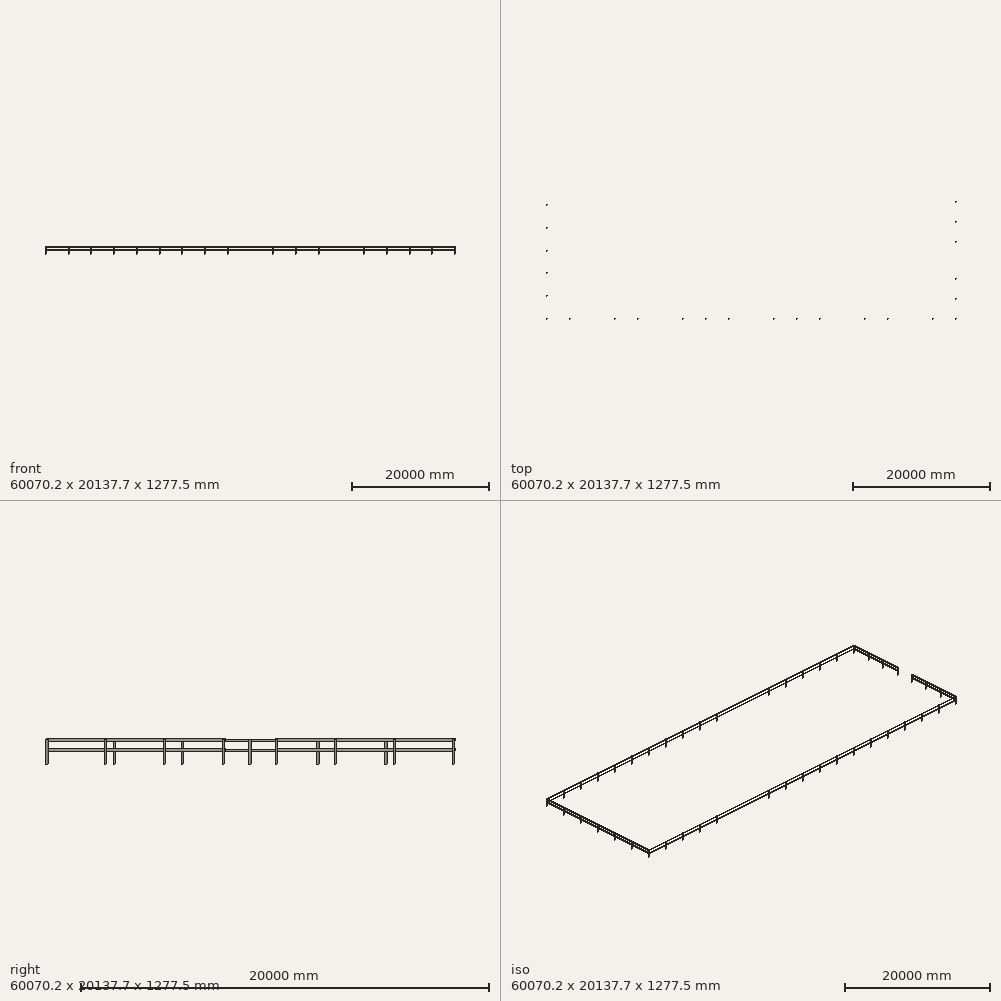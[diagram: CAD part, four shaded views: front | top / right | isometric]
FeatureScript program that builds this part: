
annotation { "Feature Type Name" : "Feature", "Feature Type Description" : "" }
export const myFeature = defineFeature(function(context is Context, id is Id, definition is map)
    precondition{}
    {
        {
            var Q0;
            Q0=qCreatedBy(makeId("Top.planeOp"),FACE);
            var sketch = newSketch(context, id + "F0", { "sketchPlane" : qUnion([Q0])});
            skCircle(sketch, "E0", {"center": v(5.25, 29.78) * mm, "radius": 62.5 * mm});
            skPoint(sketch, "E0.first.point", {"position": v(-49.7, 0) * mm});
            skPoint(sketch, "E0.second.point", {"position": v(41.75, 80.52) * mm});
            skPoint(sketch, "E0.third.point", {"position": v(-50.7, 57.65) * mm});
            skSolve(sketch);
        }
        {
            var Q0;
            Q0=makeQuery(id+"F0.imprint","IMPRINT",FACE,{"disambiguationData":[TD([[makeQuery(id+"F0.imprint","IMPRINT",EDGE,{"derivedFrom":sQuery(id+"F0.wireOp",EDGE,"E0")}),1.0]])]});
            extrude(context, id + "F1", {"entities" : qUnion([Q0]), "depth" : 1250 * mm});
        }
        {
            var Q0;
            Q0=makeQuery(id+"F1.opExtrude","SWEPT_BODY",BODY,{"disambiguationData":[OSD([sQuery(id+"F0.wireOp",EDGE,"E0")])]});
            transform(context, id + "F2", {"entities" : qUnion([Q0]), "transformType" : TransformType.TRANSLATION_3D, "dx" : 3330 * mm, "dy" : 0 * mm, "dz" : 0 * mm, "makeCopy" : true});
        }
        {
            var Q0;
            Q0=makeQuery(id+"F2.opPattern","COPY",BODY,{"derivedFrom":makeQuery(id+"F1.opExtrude","SWEPT_BODY",BODY,{"disambiguationData":[OSD([sQuery(id+"F0.wireOp",EDGE,"E0")])]}),"instanceName":"1"});
            transform(context, id + "F3", {"entities" : qUnion([Q0]), "transformType" : TransformType.TRANSLATION_3D, "dx" : 3330 * mm, "dy" : 0 * mm, "dz" : 0 * mm, "makeCopy" : true});
        }
        {
            var Q0;
            Q0=makeQuery(id+"F3.opPattern","COPY",BODY,{"derivedFrom":makeQuery(id+"F2.opPattern","COPY",BODY,{"derivedFrom":makeQuery(id+"F1.opExtrude","SWEPT_BODY",BODY,{"disambiguationData":[OSD([sQuery(id+"F0.wireOp",EDGE,"E0")])]}),"instanceName":"1"}),"instanceName":"1"});
            transform(context, id + "F4", {"entities" : qUnion([Q0]), "transformType" : TransformType.TRANSLATION_3D, "dx" : 3330 * mm, "dy" : 0 * mm, "dz" : 0 * mm, "makeCopy" : true});
        }
        {
            var Q0;
            Q0=makeQuery(id+"F4.opPattern","COPY",BODY,{"derivedFrom":makeQuery(id+"F3.opPattern","COPY",BODY,{"derivedFrom":makeQuery(id+"F2.opPattern","COPY",BODY,{"derivedFrom":makeQuery(id+"F1.opExtrude","SWEPT_BODY",BODY,{"disambiguationData":[OSD([sQuery(id+"F0.wireOp",EDGE,"E0")])]}),"instanceName":"1"}),"instanceName":"1"}),"instanceName":"1"});
            transform(context, id + "F5", {"entities" : qUnion([Q0]), "transformType" : TransformType.TRANSLATION_3D, "dx" : 3330 * mm, "dy" : 0 * mm, "dz" : 0 * mm, "makeCopy" : true});
        }
        {
            var Q0;
            Q0=makeQuery(id+"F5.opPattern","COPY",BODY,{"derivedFrom":makeQuery(id+"F4.opPattern","COPY",BODY,{"derivedFrom":makeQuery(id+"F3.opPattern","COPY",BODY,{"derivedFrom":makeQuery(id+"F2.opPattern","COPY",BODY,{"derivedFrom":makeQuery(id+"F1.opExtrude","SWEPT_BODY",BODY,{"disambiguationData":[OSD([sQuery(id+"F0.wireOp",EDGE,"E0")])]}),"instanceName":"1"}),"instanceName":"1"}),"instanceName":"1"}),"instanceName":"1"});
            transform(context, id + "F6", {"entities" : qUnion([Q0]), "transformType" : TransformType.TRANSLATION_3D, "dx" : 3330 * mm, "dy" : 0 * mm, "dz" : 0 * mm, "makeCopy" : true});
        }
        {
            var Q0;
            Q0=makeQuery(id+"F6.opPattern","COPY",BODY,{"derivedFrom":makeQuery(id+"F5.opPattern","COPY",BODY,{"derivedFrom":makeQuery(id+"F4.opPattern","COPY",BODY,{"derivedFrom":makeQuery(id+"F3.opPattern","COPY",BODY,{"derivedFrom":makeQuery(id+"F2.opPattern","COPY",BODY,{"derivedFrom":makeQuery(id+"F1.opExtrude","SWEPT_BODY",BODY,{"disambiguationData":[OSD([sQuery(id+"F0.wireOp",EDGE,"E0")])]}),"instanceName":"1"}),"instanceName":"1"}),"instanceName":"1"}),"instanceName":"1"}),"instanceName":"1"});
            transform(context, id + "F7", {"entities" : qUnion([Q0]), "transformType" : TransformType.TRANSLATION_3D, "dx" : 3330 * mm, "dy" : 0 * mm, "dz" : 0 * mm, "makeCopy" : true});
        }
        {
            var Q0;
            Q0=makeQuery(id+"F7.opPattern","COPY",BODY,{"derivedFrom":makeQuery(id+"F6.opPattern","COPY",BODY,{"derivedFrom":makeQuery(id+"F5.opPattern","COPY",BODY,{"derivedFrom":makeQuery(id+"F4.opPattern","COPY",BODY,{"derivedFrom":makeQuery(id+"F3.opPattern","COPY",BODY,{"derivedFrom":makeQuery(id+"F2.opPattern","COPY",BODY,{"derivedFrom":makeQuery(id+"F1.opExtrude","SWEPT_BODY",BODY,{"disambiguationData":[OSD([sQuery(id+"F0.wireOp",EDGE,"E0")])]}),"instanceName":"1"}),"instanceName":"1"}),"instanceName":"1"}),"instanceName":"1"}),"instanceName":"1"}),"instanceName":"1"});
            transform(context, id + "F8", {"entities" : qUnion([Q0]), "transformType" : TransformType.TRANSLATION_3D, "dx" : 3330 * mm, "dy" : 0 * mm, "dz" : 0 * mm, "makeCopy" : true});
        }
        {
            var Q0;
            Q0=makeQuery(id+"F8.opPattern","COPY",BODY,{"derivedFrom":makeQuery(id+"F7.opPattern","COPY",BODY,{"derivedFrom":makeQuery(id+"F6.opPattern","COPY",BODY,{"derivedFrom":makeQuery(id+"F5.opPattern","COPY",BODY,{"derivedFrom":makeQuery(id+"F4.opPattern","COPY",BODY,{"derivedFrom":makeQuery(id+"F3.opPattern","COPY",BODY,{"derivedFrom":makeQuery(id+"F2.opPattern","COPY",BODY,{"derivedFrom":makeQuery(id+"F1.opExtrude","SWEPT_BODY",BODY,{"disambiguationData":[OSD([sQuery(id+"F0.wireOp",EDGE,"E0")])]}),"instanceName":"1"}),"instanceName":"1"}),"instanceName":"1"}),"instanceName":"1"}),"instanceName":"1"}),"instanceName":"1"}),"instanceName":"1"});
            transform(context, id + "F9", {"entities" : qUnion([Q0]), "transformType" : TransformType.TRANSLATION_3D, "dx" : 3330 * mm, "dy" : 0 * mm, "dz" : 0 * mm, "makeCopy" : true});
        }
        {
            var Q0;
            Q0=makeQuery(id+"F9.opPattern","COPY",BODY,{"derivedFrom":makeQuery(id+"F8.opPattern","COPY",BODY,{"derivedFrom":makeQuery(id+"F7.opPattern","COPY",BODY,{"derivedFrom":makeQuery(id+"F6.opPattern","COPY",BODY,{"derivedFrom":makeQuery(id+"F5.opPattern","COPY",BODY,{"derivedFrom":makeQuery(id+"F4.opPattern","COPY",BODY,{"derivedFrom":makeQuery(id+"F3.opPattern","COPY",BODY,{"derivedFrom":makeQuery(id+"F2.opPattern","COPY",BODY,{"derivedFrom":makeQuery(id+"F1.opExtrude","SWEPT_BODY",BODY,{"disambiguationData":[OSD([sQuery(id+"F0.wireOp",EDGE,"E0")])]}),"instanceName":"1"}),"instanceName":"1"}),"instanceName":"1"}),"instanceName":"1"}),"instanceName":"1"}),"instanceName":"1"}),"instanceName":"1"}),"instanceName":"1"});
            transform(context, id + "F10", {"entities" : qUnion([Q0]), "transformType" : TransformType.TRANSLATION_3D, "dx" : 3330 * mm, "dy" : 0 * mm, "dz" : 0 * mm, "makeCopy" : true});
        }
        {
            var Q0;
            Q0=makeQuery(id+"F10.opPattern","COPY",BODY,{"derivedFrom":makeQuery(id+"F9.opPattern","COPY",BODY,{"derivedFrom":makeQuery(id+"F8.opPattern","COPY",BODY,{"derivedFrom":makeQuery(id+"F7.opPattern","COPY",BODY,{"derivedFrom":makeQuery(id+"F6.opPattern","COPY",BODY,{"derivedFrom":makeQuery(id+"F5.opPattern","COPY",BODY,{"derivedFrom":makeQuery(id+"F4.opPattern","COPY",BODY,{"derivedFrom":makeQuery(id+"F3.opPattern","COPY",BODY,{"derivedFrom":makeQuery(id+"F2.opPattern","COPY",BODY,{"derivedFrom":makeQuery(id+"F1.opExtrude","SWEPT_BODY",BODY,{"disambiguationData":[OSD([sQuery(id+"F0.wireOp",EDGE,"E0")])]}),"instanceName":"1"}),"instanceName":"1"}),"instanceName":"1"}),"instanceName":"1"}),"instanceName":"1"}),"instanceName":"1"}),"instanceName":"1"}),"instanceName":"1"}),"instanceName":"1"});
            transform(context, id + "F11", {"entities" : qUnion([Q0]), "transformType" : TransformType.TRANSLATION_3D, "dx" : 3330 * mm, "dy" : 0 * mm, "dz" : 0 * mm, "makeCopy" : true});
        }
        {
            var Q0;
            Q0=makeQuery(id+"F11.opPattern","COPY",BODY,{"derivedFrom":makeQuery(id+"F10.opPattern","COPY",BODY,{"derivedFrom":makeQuery(id+"F9.opPattern","COPY",BODY,{"derivedFrom":makeQuery(id+"F8.opPattern","COPY",BODY,{"derivedFrom":makeQuery(id+"F7.opPattern","COPY",BODY,{"derivedFrom":makeQuery(id+"F6.opPattern","COPY",BODY,{"derivedFrom":makeQuery(id+"F5.opPattern","COPY",BODY,{"derivedFrom":makeQuery(id+"F4.opPattern","COPY",BODY,{"derivedFrom":makeQuery(id+"F3.opPattern","COPY",BODY,{"derivedFrom":makeQuery(id+"F2.opPattern","COPY",BODY,{"derivedFrom":makeQuery(id+"F1.opExtrude","SWEPT_BODY",BODY,{"disambiguationData":[OSD([sQuery(id+"F0.wireOp",EDGE,"E0")])]}),"instanceName":"1"}),"instanceName":"1"}),"instanceName":"1"}),"instanceName":"1"}),"instanceName":"1"}),"instanceName":"1"}),"instanceName":"1"}),"instanceName":"1"}),"instanceName":"1"}),"instanceName":"1"});
            transform(context, id + "F12", {"entities" : qUnion([Q0]), "transformType" : TransformType.TRANSLATION_3D, "dx" : 3330 * mm, "dy" : 0 * mm, "dz" : 0 * mm, "makeCopy" : true});
        }
        {
            var Q0;
            Q0=makeQuery(id+"F12.opPattern","COPY",BODY,{"derivedFrom":makeQuery(id+"F11.opPattern","COPY",BODY,{"derivedFrom":makeQuery(id+"F10.opPattern","COPY",BODY,{"derivedFrom":makeQuery(id+"F9.opPattern","COPY",BODY,{"derivedFrom":makeQuery(id+"F8.opPattern","COPY",BODY,{"derivedFrom":makeQuery(id+"F7.opPattern","COPY",BODY,{"derivedFrom":makeQuery(id+"F6.opPattern","COPY",BODY,{"derivedFrom":makeQuery(id+"F5.opPattern","COPY",BODY,{"derivedFrom":makeQuery(id+"F4.opPattern","COPY",BODY,{"derivedFrom":makeQuery(id+"F3.opPattern","COPY",BODY,{"derivedFrom":makeQuery(id+"F2.opPattern","COPY",BODY,{"derivedFrom":makeQuery(id+"F1.opExtrude","SWEPT_BODY",BODY,{"disambiguationData":[OSD([sQuery(id+"F0.wireOp",EDGE,"E0")])]}),"instanceName":"1"}),"instanceName":"1"}),"instanceName":"1"}),"instanceName":"1"}),"instanceName":"1"}),"instanceName":"1"}),"instanceName":"1"}),"instanceName":"1"}),"instanceName":"1"}),"instanceName":"1"}),"instanceName":"1"});
            transform(context, id + "F13", {"entities" : qUnion([Q0]), "transformType" : TransformType.TRANSLATION_3D, "dx" : 3330 * mm, "dy" : 0 * mm, "dz" : 0 * mm, "makeCopy" : true});
        }
        {
            var Q0;
            Q0=makeQuery(id+"F13.opPattern","COPY",BODY,{"derivedFrom":makeQuery(id+"F12.opPattern","COPY",BODY,{"derivedFrom":makeQuery(id+"F11.opPattern","COPY",BODY,{"derivedFrom":makeQuery(id+"F10.opPattern","COPY",BODY,{"derivedFrom":makeQuery(id+"F9.opPattern","COPY",BODY,{"derivedFrom":makeQuery(id+"F8.opPattern","COPY",BODY,{"derivedFrom":makeQuery(id+"F7.opPattern","COPY",BODY,{"derivedFrom":makeQuery(id+"F6.opPattern","COPY",BODY,{"derivedFrom":makeQuery(id+"F5.opPattern","COPY",BODY,{"derivedFrom":makeQuery(id+"F4.opPattern","COPY",BODY,{"derivedFrom":makeQuery(id+"F3.opPattern","COPY",BODY,{"derivedFrom":makeQuery(id+"F2.opPattern","COPY",BODY,{"derivedFrom":makeQuery(id+"F1.opExtrude","SWEPT_BODY",BODY,{"disambiguationData":[OSD([sQuery(id+"F0.wireOp",EDGE,"E0")])]}),"instanceName":"1"}),"instanceName":"1"}),"instanceName":"1"}),"instanceName":"1"}),"instanceName":"1"}),"instanceName":"1"}),"instanceName":"1"}),"instanceName":"1"}),"instanceName":"1"}),"instanceName":"1"}),"instanceName":"1"}),"instanceName":"1"});
            transform(context, id + "F14", {"entities" : qUnion([Q0]), "transformType" : TransformType.TRANSLATION_3D, "dx" : 3330 * mm, "dy" : 0 * mm, "dz" : 0 * mm, "makeCopy" : true});
        }
        {
            var Q0;
            Q0=makeQuery(id+"F14.opPattern","COPY",BODY,{"derivedFrom":makeQuery(id+"F13.opPattern","COPY",BODY,{"derivedFrom":makeQuery(id+"F12.opPattern","COPY",BODY,{"derivedFrom":makeQuery(id+"F11.opPattern","COPY",BODY,{"derivedFrom":makeQuery(id+"F10.opPattern","COPY",BODY,{"derivedFrom":makeQuery(id+"F9.opPattern","COPY",BODY,{"derivedFrom":makeQuery(id+"F8.opPattern","COPY",BODY,{"derivedFrom":makeQuery(id+"F7.opPattern","COPY",BODY,{"derivedFrom":makeQuery(id+"F6.opPattern","COPY",BODY,{"derivedFrom":makeQuery(id+"F5.opPattern","COPY",BODY,{"derivedFrom":makeQuery(id+"F4.opPattern","COPY",BODY,{"derivedFrom":makeQuery(id+"F3.opPattern","COPY",BODY,{"derivedFrom":makeQuery(id+"F2.opPattern","COPY",BODY,{"derivedFrom":makeQuery(id+"F1.opExtrude","SWEPT_BODY",BODY,{"disambiguationData":[OSD([sQuery(id+"F0.wireOp",EDGE,"E0")])]}),"instanceName":"1"}),"instanceName":"1"}),"instanceName":"1"}),"instanceName":"1"}),"instanceName":"1"}),"instanceName":"1"}),"instanceName":"1"}),"instanceName":"1"}),"instanceName":"1"}),"instanceName":"1"}),"instanceName":"1"}),"instanceName":"1"}),"instanceName":"1"});
            transform(context, id + "F15", {"entities" : qUnion([Q0]), "transformType" : TransformType.TRANSLATION_3D, "dx" : 3330 * mm, "dy" : 0 * mm, "dz" : 0 * mm, "makeCopy" : true});
        }
        {
            var Q0;
            Q0=makeQuery(id+"F15.opPattern","COPY",BODY,{"derivedFrom":makeQuery(id+"F14.opPattern","COPY",BODY,{"derivedFrom":makeQuery(id+"F13.opPattern","COPY",BODY,{"derivedFrom":makeQuery(id+"F12.opPattern","COPY",BODY,{"derivedFrom":makeQuery(id+"F11.opPattern","COPY",BODY,{"derivedFrom":makeQuery(id+"F10.opPattern","COPY",BODY,{"derivedFrom":makeQuery(id+"F9.opPattern","COPY",BODY,{"derivedFrom":makeQuery(id+"F8.opPattern","COPY",BODY,{"derivedFrom":makeQuery(id+"F7.opPattern","COPY",BODY,{"derivedFrom":makeQuery(id+"F6.opPattern","COPY",BODY,{"derivedFrom":makeQuery(id+"F5.opPattern","COPY",BODY,{"derivedFrom":makeQuery(id+"F4.opPattern","COPY",BODY,{"derivedFrom":makeQuery(id+"F3.opPattern","COPY",BODY,{"derivedFrom":makeQuery(id+"F2.opPattern","COPY",BODY,{"derivedFrom":makeQuery(id+"F1.opExtrude","SWEPT_BODY",BODY,{"disambiguationData":[OSD([sQuery(id+"F0.wireOp",EDGE,"E0")])]}),"instanceName":"1"}),"instanceName":"1"}),"instanceName":"1"}),"instanceName":"1"}),"instanceName":"1"}),"instanceName":"1"}),"instanceName":"1"}),"instanceName":"1"}),"instanceName":"1"}),"instanceName":"1"}),"instanceName":"1"}),"instanceName":"1"}),"instanceName":"1"}),"instanceName":"1"});
            transform(context, id + "F16", {"entities" : qUnion([Q0]), "transformType" : TransformType.TRANSLATION_3D, "dx" : 3330 * mm, "dy" : 0 * mm, "dz" : 0 * mm, "makeCopy" : true});
        }
        {
            var Q0;
            Q0=makeQuery(id+"F16.opPattern","COPY",BODY,{"derivedFrom":makeQuery(id+"F15.opPattern","COPY",BODY,{"derivedFrom":makeQuery(id+"F14.opPattern","COPY",BODY,{"derivedFrom":makeQuery(id+"F13.opPattern","COPY",BODY,{"derivedFrom":makeQuery(id+"F12.opPattern","COPY",BODY,{"derivedFrom":makeQuery(id+"F11.opPattern","COPY",BODY,{"derivedFrom":makeQuery(id+"F10.opPattern","COPY",BODY,{"derivedFrom":makeQuery(id+"F9.opPattern","COPY",BODY,{"derivedFrom":makeQuery(id+"F8.opPattern","COPY",BODY,{"derivedFrom":makeQuery(id+"F7.opPattern","COPY",BODY,{"derivedFrom":makeQuery(id+"F6.opPattern","COPY",BODY,{"derivedFrom":makeQuery(id+"F5.opPattern","COPY",BODY,{"derivedFrom":makeQuery(id+"F4.opPattern","COPY",BODY,{"derivedFrom":makeQuery(id+"F3.opPattern","COPY",BODY,{"derivedFrom":makeQuery(id+"F2.opPattern","COPY",BODY,{"derivedFrom":makeQuery(id+"F1.opExtrude","SWEPT_BODY",BODY,{"disambiguationData":[OSD([sQuery(id+"F0.wireOp",EDGE,"E0")])]}),"instanceName":"1"}),"instanceName":"1"}),"instanceName":"1"}),"instanceName":"1"}),"instanceName":"1"}),"instanceName":"1"}),"instanceName":"1"}),"instanceName":"1"}),"instanceName":"1"}),"instanceName":"1"}),"instanceName":"1"}),"instanceName":"1"}),"instanceName":"1"}),"instanceName":"1"}),"instanceName":"1"});
            transform(context, id + "F17", {"entities" : qUnion([Q0]), "transformType" : TransformType.TRANSLATION_3D, "dx" : 3330 * mm, "dy" : 0 * mm, "dz" : 0 * mm, "makeCopy" : true});
        }
        {
            var Q0;
            Q0=makeQuery(id+"F1.opExtrude","SWEPT_BODY",BODY,{"disambiguationData":[OSD([sQuery(id+"F0.wireOp",EDGE,"E0")])]});
            transform(context, id + "F18", {"entities" : qUnion([Q0]), "transformType" : TransformType.TRANSLATION_3D, "dx" : 0 * mm, "dy" : 3330 * mm, "dz" : 0 * mm, "makeCopy" : true});
        }
        {
            var Q0;
            Q0=makeQuery(id+"F18.opPattern","COPY",BODY,{"derivedFrom":makeQuery(id+"F1.opExtrude","SWEPT_BODY",BODY,{"disambiguationData":[OSD([sQuery(id+"F0.wireOp",EDGE,"E0")])]}),"instanceName":"1"});
            transform(context, id + "F19", {"entities" : qUnion([Q0]), "transformType" : TransformType.TRANSLATION_3D, "dx" : 0 * mm, "dy" : 3330 * mm, "dz" : 0 * mm, "makeCopy" : true});
        }
        {
            var Q0;
            Q0=makeQuery(id+"F19.opPattern","COPY",BODY,{"derivedFrom":makeQuery(id+"F18.opPattern","COPY",BODY,{"derivedFrom":makeQuery(id+"F1.opExtrude","SWEPT_BODY",BODY,{"disambiguationData":[OSD([sQuery(id+"F0.wireOp",EDGE,"E0")])]}),"instanceName":"1"}),"instanceName":"1"});
            transform(context, id + "F20", {"entities" : qUnion([Q0]), "transformType" : TransformType.TRANSLATION_3D, "dx" : 0 * mm, "dy" : 3330 * mm, "dz" : 0 * mm, "makeCopy" : true});
        }
        {
            var Q0;
            Q0=makeQuery(id+"F20.opPattern","COPY",BODY,{"derivedFrom":makeQuery(id+"F19.opPattern","COPY",BODY,{"derivedFrom":makeQuery(id+"F18.opPattern","COPY",BODY,{"derivedFrom":makeQuery(id+"F1.opExtrude","SWEPT_BODY",BODY,{"disambiguationData":[OSD([sQuery(id+"F0.wireOp",EDGE,"E0")])]}),"instanceName":"1"}),"instanceName":"1"}),"instanceName":"1"});
            transform(context, id + "F21", {"entities" : qUnion([Q0]), "transformType" : TransformType.TRANSLATION_3D, "dx" : 0 * mm, "dy" : 3330 * mm, "dz" : 0 * mm, "makeCopy" : true});
        }
        {
            var Q0;
            Q0=makeQuery(id+"F21.opPattern","COPY",BODY,{"derivedFrom":makeQuery(id+"F20.opPattern","COPY",BODY,{"derivedFrom":makeQuery(id+"F19.opPattern","COPY",BODY,{"derivedFrom":makeQuery(id+"F18.opPattern","COPY",BODY,{"derivedFrom":makeQuery(id+"F1.opExtrude","SWEPT_BODY",BODY,{"disambiguationData":[OSD([sQuery(id+"F0.wireOp",EDGE,"E0")])]}),"instanceName":"1"}),"instanceName":"1"}),"instanceName":"1"}),"instanceName":"1"});
            transform(context, id + "F22", {"entities" : qUnion([Q0]), "transformType" : TransformType.TRANSLATION_3D, "dx" : 0 * mm, "dy" : 3330 * mm, "dz" : 0 * mm, "makeCopy" : true});
        }
        {
            var Q0;
            Q0=makeQuery(id+"F22.opPattern","COPY",BODY,{"derivedFrom":makeQuery(id+"F21.opPattern","COPY",BODY,{"derivedFrom":makeQuery(id+"F20.opPattern","COPY",BODY,{"derivedFrom":makeQuery(id+"F19.opPattern","COPY",BODY,{"derivedFrom":makeQuery(id+"F18.opPattern","COPY",BODY,{"derivedFrom":makeQuery(id+"F1.opExtrude","SWEPT_BODY",BODY,{"disambiguationData":[OSD([sQuery(id+"F0.wireOp",EDGE,"E0")])]}),"instanceName":"1"}),"instanceName":"1"}),"instanceName":"1"}),"instanceName":"1"}),"instanceName":"1"});
            transform(context, id + "F23", {"entities" : qUnion([Q0]), "transformType" : TransformType.TRANSLATION_3D, "dx" : 0 * mm, "dy" : 3330 * mm, "dz" : 0 * mm, "makeCopy" : true});
        }
        {
            var Q0;
            Q0=makeQuery(id+"F23.opPattern","COPY",BODY,{"derivedFrom":makeQuery(id+"F22.opPattern","COPY",BODY,{"derivedFrom":makeQuery(id+"F21.opPattern","COPY",BODY,{"derivedFrom":makeQuery(id+"F20.opPattern","COPY",BODY,{"derivedFrom":makeQuery(id+"F19.opPattern","COPY",BODY,{"derivedFrom":makeQuery(id+"F18.opPattern","COPY",BODY,{"derivedFrom":makeQuery(id+"F1.opExtrude","SWEPT_BODY",BODY,{"disambiguationData":[OSD([sQuery(id+"F0.wireOp",EDGE,"E0")])]}),"instanceName":"1"}),"instanceName":"1"}),"instanceName":"1"}),"instanceName":"1"}),"instanceName":"1"}),"instanceName":"1"});
            transform(context, id + "F24", {"entities" : qUnion([Q0]), "transformType" : TransformType.TRANSLATION_3D, "dx" : 3330 * mm, "dy" : 0 * mm, "dz" : 0 * mm, "makeCopy" : true});
        }
        {
            var Q0;
            Q0=makeQuery(id+"F24.opPattern","COPY",BODY,{"derivedFrom":makeQuery(id+"F23.opPattern","COPY",BODY,{"derivedFrom":makeQuery(id+"F22.opPattern","COPY",BODY,{"derivedFrom":makeQuery(id+"F21.opPattern","COPY",BODY,{"derivedFrom":makeQuery(id+"F20.opPattern","COPY",BODY,{"derivedFrom":makeQuery(id+"F19.opPattern","COPY",BODY,{"derivedFrom":makeQuery(id+"F18.opPattern","COPY",BODY,{"derivedFrom":makeQuery(id+"F1.opExtrude","SWEPT_BODY",BODY,{"disambiguationData":[OSD([sQuery(id+"F0.wireOp",EDGE,"E0")])]}),"instanceName":"1"}),"instanceName":"1"}),"instanceName":"1"}),"instanceName":"1"}),"instanceName":"1"}),"instanceName":"1"}),"instanceName":"1"});
            transform(context, id + "F25", {"entities" : qUnion([Q0]), "transformType" : TransformType.TRANSLATION_3D, "dx" : 3330 * mm, "dy" : 0 * mm, "dz" : 0 * mm, "makeCopy" : true});
        }
        {
            var Q0;
            Q0=makeQuery(id+"F25.opPattern","COPY",BODY,{"derivedFrom":makeQuery(id+"F24.opPattern","COPY",BODY,{"derivedFrom":makeQuery(id+"F23.opPattern","COPY",BODY,{"derivedFrom":makeQuery(id+"F22.opPattern","COPY",BODY,{"derivedFrom":makeQuery(id+"F21.opPattern","COPY",BODY,{"derivedFrom":makeQuery(id+"F20.opPattern","COPY",BODY,{"derivedFrom":makeQuery(id+"F19.opPattern","COPY",BODY,{"derivedFrom":makeQuery(id+"F18.opPattern","COPY",BODY,{"derivedFrom":makeQuery(id+"F1.opExtrude","SWEPT_BODY",BODY,{"disambiguationData":[OSD([sQuery(id+"F0.wireOp",EDGE,"E0")])]}),"instanceName":"1"}),"instanceName":"1"}),"instanceName":"1"}),"instanceName":"1"}),"instanceName":"1"}),"instanceName":"1"}),"instanceName":"1"}),"instanceName":"1"});
            transform(context, id + "F26", {"entities" : qUnion([Q0]), "transformType" : TransformType.TRANSLATION_3D, "dx" : 3330 * mm, "dy" : 0 * mm, "dz" : 0 * mm, "makeCopy" : true});
        }
        {
            var Q0;
            Q0=makeQuery(id+"F26.opPattern","COPY",BODY,{"derivedFrom":makeQuery(id+"F25.opPattern","COPY",BODY,{"derivedFrom":makeQuery(id+"F24.opPattern","COPY",BODY,{"derivedFrom":makeQuery(id+"F23.opPattern","COPY",BODY,{"derivedFrom":makeQuery(id+"F22.opPattern","COPY",BODY,{"derivedFrom":makeQuery(id+"F21.opPattern","COPY",BODY,{"derivedFrom":makeQuery(id+"F20.opPattern","COPY",BODY,{"derivedFrom":makeQuery(id+"F19.opPattern","COPY",BODY,{"derivedFrom":makeQuery(id+"F18.opPattern","COPY",BODY,{"derivedFrom":makeQuery(id+"F1.opExtrude","SWEPT_BODY",BODY,{"disambiguationData":[OSD([sQuery(id+"F0.wireOp",EDGE,"E0")])]}),"instanceName":"1"}),"instanceName":"1"}),"instanceName":"1"}),"instanceName":"1"}),"instanceName":"1"}),"instanceName":"1"}),"instanceName":"1"}),"instanceName":"1"}),"instanceName":"1"});
            transform(context, id + "F27", {"entities" : qUnion([Q0]), "transformType" : TransformType.TRANSLATION_3D, "dx" : 3330 * mm, "dy" : 0 * mm, "dz" : 0 * mm, "makeCopy" : true});
        }
        {
            var Q0;
            Q0=makeQuery(id+"F27.opPattern","COPY",BODY,{"derivedFrom":makeQuery(id+"F26.opPattern","COPY",BODY,{"derivedFrom":makeQuery(id+"F25.opPattern","COPY",BODY,{"derivedFrom":makeQuery(id+"F24.opPattern","COPY",BODY,{"derivedFrom":makeQuery(id+"F23.opPattern","COPY",BODY,{"derivedFrom":makeQuery(id+"F22.opPattern","COPY",BODY,{"derivedFrom":makeQuery(id+"F21.opPattern","COPY",BODY,{"derivedFrom":makeQuery(id+"F20.opPattern","COPY",BODY,{"derivedFrom":makeQuery(id+"F19.opPattern","COPY",BODY,{"derivedFrom":makeQuery(id+"F18.opPattern","COPY",BODY,{"derivedFrom":makeQuery(id+"F1.opExtrude","SWEPT_BODY",BODY,{"disambiguationData":[OSD([sQuery(id+"F0.wireOp",EDGE,"E0")])]}),"instanceName":"1"}),"instanceName":"1"}),"instanceName":"1"}),"instanceName":"1"}),"instanceName":"1"}),"instanceName":"1"}),"instanceName":"1"}),"instanceName":"1"}),"instanceName":"1"}),"instanceName":"1"});
            transform(context, id + "F28", {"entities" : qUnion([Q0]), "transformType" : TransformType.TRANSLATION_3D, "dx" : 3330 * mm, "dy" : 0 * mm, "dz" : 0 * mm, "makeCopy" : true});
        }
        {
            var Q0;
            Q0=makeQuery(id+"F28.opPattern","COPY",BODY,{"derivedFrom":makeQuery(id+"F27.opPattern","COPY",BODY,{"derivedFrom":makeQuery(id+"F26.opPattern","COPY",BODY,{"derivedFrom":makeQuery(id+"F25.opPattern","COPY",BODY,{"derivedFrom":makeQuery(id+"F24.opPattern","COPY",BODY,{"derivedFrom":makeQuery(id+"F23.opPattern","COPY",BODY,{"derivedFrom":makeQuery(id+"F22.opPattern","COPY",BODY,{"derivedFrom":makeQuery(id+"F21.opPattern","COPY",BODY,{"derivedFrom":makeQuery(id+"F20.opPattern","COPY",BODY,{"derivedFrom":makeQuery(id+"F19.opPattern","COPY",BODY,{"derivedFrom":makeQuery(id+"F18.opPattern","COPY",BODY,{"derivedFrom":makeQuery(id+"F1.opExtrude","SWEPT_BODY",BODY,{"disambiguationData":[OSD([sQuery(id+"F0.wireOp",EDGE,"E0")])]}),"instanceName":"1"}),"instanceName":"1"}),"instanceName":"1"}),"instanceName":"1"}),"instanceName":"1"}),"instanceName":"1"}),"instanceName":"1"}),"instanceName":"1"}),"instanceName":"1"}),"instanceName":"1"}),"instanceName":"1"});
            transform(context, id + "F29", {"entities" : qUnion([Q0]), "transformType" : TransformType.TRANSLATION_3D, "dx" : 3330 * mm, "dy" : 0 * mm, "dz" : 0 * mm, "makeCopy" : true});
        }
        {
            var Q0;
            Q0=makeQuery(id+"F29.opPattern","COPY",BODY,{"derivedFrom":makeQuery(id+"F28.opPattern","COPY",BODY,{"derivedFrom":makeQuery(id+"F27.opPattern","COPY",BODY,{"derivedFrom":makeQuery(id+"F26.opPattern","COPY",BODY,{"derivedFrom":makeQuery(id+"F25.opPattern","COPY",BODY,{"derivedFrom":makeQuery(id+"F24.opPattern","COPY",BODY,{"derivedFrom":makeQuery(id+"F23.opPattern","COPY",BODY,{"derivedFrom":makeQuery(id+"F22.opPattern","COPY",BODY,{"derivedFrom":makeQuery(id+"F21.opPattern","COPY",BODY,{"derivedFrom":makeQuery(id+"F20.opPattern","COPY",BODY,{"derivedFrom":makeQuery(id+"F19.opPattern","COPY",BODY,{"derivedFrom":makeQuery(id+"F18.opPattern","COPY",BODY,{"derivedFrom":makeQuery(id+"F1.opExtrude","SWEPT_BODY",BODY,{"disambiguationData":[OSD([sQuery(id+"F0.wireOp",EDGE,"E0")])]}),"instanceName":"1"}),"instanceName":"1"}),"instanceName":"1"}),"instanceName":"1"}),"instanceName":"1"}),"instanceName":"1"}),"instanceName":"1"}),"instanceName":"1"}),"instanceName":"1"}),"instanceName":"1"}),"instanceName":"1"}),"instanceName":"1"});
            transform(context, id + "F30", {"entities" : qUnion([Q0]), "transformType" : TransformType.TRANSLATION_3D, "dx" : 3330 * mm, "dy" : 0 * mm, "dz" : 0 * mm, "makeCopy" : true});
        }
        {
            var Q0;
            Q0=makeQuery(id+"F30.opPattern","COPY",BODY,{"derivedFrom":makeQuery(id+"F29.opPattern","COPY",BODY,{"derivedFrom":makeQuery(id+"F28.opPattern","COPY",BODY,{"derivedFrom":makeQuery(id+"F27.opPattern","COPY",BODY,{"derivedFrom":makeQuery(id+"F26.opPattern","COPY",BODY,{"derivedFrom":makeQuery(id+"F25.opPattern","COPY",BODY,{"derivedFrom":makeQuery(id+"F24.opPattern","COPY",BODY,{"derivedFrom":makeQuery(id+"F23.opPattern","COPY",BODY,{"derivedFrom":makeQuery(id+"F22.opPattern","COPY",BODY,{"derivedFrom":makeQuery(id+"F21.opPattern","COPY",BODY,{"derivedFrom":makeQuery(id+"F20.opPattern","COPY",BODY,{"derivedFrom":makeQuery(id+"F19.opPattern","COPY",BODY,{"derivedFrom":makeQuery(id+"F18.opPattern","COPY",BODY,{"derivedFrom":makeQuery(id+"F1.opExtrude","SWEPT_BODY",BODY,{"disambiguationData":[OSD([sQuery(id+"F0.wireOp",EDGE,"E0")])]}),"instanceName":"1"}),"instanceName":"1"}),"instanceName":"1"}),"instanceName":"1"}),"instanceName":"1"}),"instanceName":"1"}),"instanceName":"1"}),"instanceName":"1"}),"instanceName":"1"}),"instanceName":"1"}),"instanceName":"1"}),"instanceName":"1"}),"instanceName":"1"});
            transform(context, id + "F31", {"entities" : qUnion([Q0]), "transformType" : TransformType.TRANSLATION_3D, "dx" : 3330 * mm, "dy" : 0 * mm, "dz" : 0 * mm, "makeCopy" : true});
        }
        {
            var Q0;
            Q0=makeQuery(id+"F31.opPattern","COPY",BODY,{"derivedFrom":makeQuery(id+"F30.opPattern","COPY",BODY,{"derivedFrom":makeQuery(id+"F29.opPattern","COPY",BODY,{"derivedFrom":makeQuery(id+"F28.opPattern","COPY",BODY,{"derivedFrom":makeQuery(id+"F27.opPattern","COPY",BODY,{"derivedFrom":makeQuery(id+"F26.opPattern","COPY",BODY,{"derivedFrom":makeQuery(id+"F25.opPattern","COPY",BODY,{"derivedFrom":makeQuery(id+"F24.opPattern","COPY",BODY,{"derivedFrom":makeQuery(id+"F23.opPattern","COPY",BODY,{"derivedFrom":makeQuery(id+"F22.opPattern","COPY",BODY,{"derivedFrom":makeQuery(id+"F21.opPattern","COPY",BODY,{"derivedFrom":makeQuery(id+"F20.opPattern","COPY",BODY,{"derivedFrom":makeQuery(id+"F19.opPattern","COPY",BODY,{"derivedFrom":makeQuery(id+"F18.opPattern","COPY",BODY,{"derivedFrom":makeQuery(id+"F1.opExtrude","SWEPT_BODY",BODY,{"disambiguationData":[OSD([sQuery(id+"F0.wireOp",EDGE,"E0")])]}),"instanceName":"1"}),"instanceName":"1"}),"instanceName":"1"}),"instanceName":"1"}),"instanceName":"1"}),"instanceName":"1"}),"instanceName":"1"}),"instanceName":"1"}),"instanceName":"1"}),"instanceName":"1"}),"instanceName":"1"}),"instanceName":"1"}),"instanceName":"1"}),"instanceName":"1"});
            transform(context, id + "F32", {"entities" : qUnion([Q0]), "transformType" : TransformType.TRANSLATION_3D, "dx" : 3330 * mm, "dy" : 0 * mm, "dz" : 0 * mm, "makeCopy" : true});
        }
        {
            var Q0;
            Q0=makeQuery(id+"F32.opPattern","COPY",BODY,{"derivedFrom":makeQuery(id+"F31.opPattern","COPY",BODY,{"derivedFrom":makeQuery(id+"F30.opPattern","COPY",BODY,{"derivedFrom":makeQuery(id+"F29.opPattern","COPY",BODY,{"derivedFrom":makeQuery(id+"F28.opPattern","COPY",BODY,{"derivedFrom":makeQuery(id+"F27.opPattern","COPY",BODY,{"derivedFrom":makeQuery(id+"F26.opPattern","COPY",BODY,{"derivedFrom":makeQuery(id+"F25.opPattern","COPY",BODY,{"derivedFrom":makeQuery(id+"F24.opPattern","COPY",BODY,{"derivedFrom":makeQuery(id+"F23.opPattern","COPY",BODY,{"derivedFrom":makeQuery(id+"F22.opPattern","COPY",BODY,{"derivedFrom":makeQuery(id+"F21.opPattern","COPY",BODY,{"derivedFrom":makeQuery(id+"F20.opPattern","COPY",BODY,{"derivedFrom":makeQuery(id+"F19.opPattern","COPY",BODY,{"derivedFrom":makeQuery(id+"F18.opPattern","COPY",BODY,{"derivedFrom":makeQuery(id+"F1.opExtrude","SWEPT_BODY",BODY,{"disambiguationData":[OSD([sQuery(id+"F0.wireOp",EDGE,"E0")])]}),"instanceName":"1"}),"instanceName":"1"}),"instanceName":"1"}),"instanceName":"1"}),"instanceName":"1"}),"instanceName":"1"}),"instanceName":"1"}),"instanceName":"1"}),"instanceName":"1"}),"instanceName":"1"}),"instanceName":"1"}),"instanceName":"1"}),"instanceName":"1"}),"instanceName":"1"}),"instanceName":"1"});
            transform(context, id + "F33", {"entities" : qUnion([Q0]), "transformType" : TransformType.TRANSLATION_3D, "dx" : 3330 * mm, "dy" : 0 * mm, "dz" : 0 * mm, "makeCopy" : true});
        }
        {
            var Q0;
            Q0=makeQuery(id+"F33.opPattern","COPY",BODY,{"derivedFrom":makeQuery(id+"F32.opPattern","COPY",BODY,{"derivedFrom":makeQuery(id+"F31.opPattern","COPY",BODY,{"derivedFrom":makeQuery(id+"F30.opPattern","COPY",BODY,{"derivedFrom":makeQuery(id+"F29.opPattern","COPY",BODY,{"derivedFrom":makeQuery(id+"F28.opPattern","COPY",BODY,{"derivedFrom":makeQuery(id+"F27.opPattern","COPY",BODY,{"derivedFrom":makeQuery(id+"F26.opPattern","COPY",BODY,{"derivedFrom":makeQuery(id+"F25.opPattern","COPY",BODY,{"derivedFrom":makeQuery(id+"F24.opPattern","COPY",BODY,{"derivedFrom":makeQuery(id+"F23.opPattern","COPY",BODY,{"derivedFrom":makeQuery(id+"F22.opPattern","COPY",BODY,{"derivedFrom":makeQuery(id+"F21.opPattern","COPY",BODY,{"derivedFrom":makeQuery(id+"F20.opPattern","COPY",BODY,{"derivedFrom":makeQuery(id+"F19.opPattern","COPY",BODY,{"derivedFrom":makeQuery(id+"F18.opPattern","COPY",BODY,{"derivedFrom":makeQuery(id+"F1.opExtrude","SWEPT_BODY",BODY,{"disambiguationData":[OSD([sQuery(id+"F0.wireOp",EDGE,"E0")])]}),"instanceName":"1"}),"instanceName":"1"}),"instanceName":"1"}),"instanceName":"1"}),"instanceName":"1"}),"instanceName":"1"}),"instanceName":"1"}),"instanceName":"1"}),"instanceName":"1"}),"instanceName":"1"}),"instanceName":"1"}),"instanceName":"1"}),"instanceName":"1"}),"instanceName":"1"}),"instanceName":"1"}),"instanceName":"1"});
            transform(context, id + "F34", {"entities" : qUnion([Q0]), "transformType" : TransformType.TRANSLATION_3D, "dx" : 3330 * mm, "dy" : 0 * mm, "dz" : 0 * mm, "makeCopy" : true});
        }
        {
            var Q0;
            Q0=makeQuery(id+"F34.opPattern","COPY",BODY,{"derivedFrom":makeQuery(id+"F33.opPattern","COPY",BODY,{"derivedFrom":makeQuery(id+"F32.opPattern","COPY",BODY,{"derivedFrom":makeQuery(id+"F31.opPattern","COPY",BODY,{"derivedFrom":makeQuery(id+"F30.opPattern","COPY",BODY,{"derivedFrom":makeQuery(id+"F29.opPattern","COPY",BODY,{"derivedFrom":makeQuery(id+"F28.opPattern","COPY",BODY,{"derivedFrom":makeQuery(id+"F27.opPattern","COPY",BODY,{"derivedFrom":makeQuery(id+"F26.opPattern","COPY",BODY,{"derivedFrom":makeQuery(id+"F25.opPattern","COPY",BODY,{"derivedFrom":makeQuery(id+"F24.opPattern","COPY",BODY,{"derivedFrom":makeQuery(id+"F23.opPattern","COPY",BODY,{"derivedFrom":makeQuery(id+"F22.opPattern","COPY",BODY,{"derivedFrom":makeQuery(id+"F21.opPattern","COPY",BODY,{"derivedFrom":makeQuery(id+"F20.opPattern","COPY",BODY,{"derivedFrom":makeQuery(id+"F19.opPattern","COPY",BODY,{"derivedFrom":makeQuery(id+"F18.opPattern","COPY",BODY,{"derivedFrom":makeQuery(id+"F1.opExtrude","SWEPT_BODY",BODY,{"disambiguationData":[OSD([sQuery(id+"F0.wireOp",EDGE,"E0")])]}),"instanceName":"1"}),"instanceName":"1"}),"instanceName":"1"}),"instanceName":"1"}),"instanceName":"1"}),"instanceName":"1"}),"instanceName":"1"}),"instanceName":"1"}),"instanceName":"1"}),"instanceName":"1"}),"instanceName":"1"}),"instanceName":"1"}),"instanceName":"1"}),"instanceName":"1"}),"instanceName":"1"}),"instanceName":"1"}),"instanceName":"1"});
            transform(context, id + "F35", {"entities" : qUnion([Q0]), "transformType" : TransformType.TRANSLATION_3D, "dx" : 3330 * mm, "dy" : 0 * mm, "dz" : 0 * mm, "makeCopy" : true});
        }
        {
            var Q0;
            Q0=makeQuery(id+"F35.opPattern","COPY",BODY,{"derivedFrom":makeQuery(id+"F34.opPattern","COPY",BODY,{"derivedFrom":makeQuery(id+"F33.opPattern","COPY",BODY,{"derivedFrom":makeQuery(id+"F32.opPattern","COPY",BODY,{"derivedFrom":makeQuery(id+"F31.opPattern","COPY",BODY,{"derivedFrom":makeQuery(id+"F30.opPattern","COPY",BODY,{"derivedFrom":makeQuery(id+"F29.opPattern","COPY",BODY,{"derivedFrom":makeQuery(id+"F28.opPattern","COPY",BODY,{"derivedFrom":makeQuery(id+"F27.opPattern","COPY",BODY,{"derivedFrom":makeQuery(id+"F26.opPattern","COPY",BODY,{"derivedFrom":makeQuery(id+"F25.opPattern","COPY",BODY,{"derivedFrom":makeQuery(id+"F24.opPattern","COPY",BODY,{"derivedFrom":makeQuery(id+"F23.opPattern","COPY",BODY,{"derivedFrom":makeQuery(id+"F22.opPattern","COPY",BODY,{"derivedFrom":makeQuery(id+"F21.opPattern","COPY",BODY,{"derivedFrom":makeQuery(id+"F20.opPattern","COPY",BODY,{"derivedFrom":makeQuery(id+"F19.opPattern","COPY",BODY,{"derivedFrom":makeQuery(id+"F18.opPattern","COPY",BODY,{"derivedFrom":makeQuery(id+"F1.opExtrude","SWEPT_BODY",BODY,{"disambiguationData":[OSD([sQuery(id+"F0.wireOp",EDGE,"E0")])]}),"instanceName":"1"}),"instanceName":"1"}),"instanceName":"1"}),"instanceName":"1"}),"instanceName":"1"}),"instanceName":"1"}),"instanceName":"1"}),"instanceName":"1"}),"instanceName":"1"}),"instanceName":"1"}),"instanceName":"1"}),"instanceName":"1"}),"instanceName":"1"}),"instanceName":"1"}),"instanceName":"1"}),"instanceName":"1"}),"instanceName":"1"}),"instanceName":"1"});
            transform(context, id + "F36", {"entities" : qUnion([Q0]), "transformType" : TransformType.TRANSLATION_3D, "dx" : 3330 * mm, "dy" : 0 * mm, "dz" : 0 * mm, "makeCopy" : true});
        }
        {
            var Q0;
            Q0=makeQuery(id+"F36.opPattern","COPY",BODY,{"derivedFrom":makeQuery(id+"F35.opPattern","COPY",BODY,{"derivedFrom":makeQuery(id+"F34.opPattern","COPY",BODY,{"derivedFrom":makeQuery(id+"F33.opPattern","COPY",BODY,{"derivedFrom":makeQuery(id+"F32.opPattern","COPY",BODY,{"derivedFrom":makeQuery(id+"F31.opPattern","COPY",BODY,{"derivedFrom":makeQuery(id+"F30.opPattern","COPY",BODY,{"derivedFrom":makeQuery(id+"F29.opPattern","COPY",BODY,{"derivedFrom":makeQuery(id+"F28.opPattern","COPY",BODY,{"derivedFrom":makeQuery(id+"F27.opPattern","COPY",BODY,{"derivedFrom":makeQuery(id+"F26.opPattern","COPY",BODY,{"derivedFrom":makeQuery(id+"F25.opPattern","COPY",BODY,{"derivedFrom":makeQuery(id+"F24.opPattern","COPY",BODY,{"derivedFrom":makeQuery(id+"F23.opPattern","COPY",BODY,{"derivedFrom":makeQuery(id+"F22.opPattern","COPY",BODY,{"derivedFrom":makeQuery(id+"F21.opPattern","COPY",BODY,{"derivedFrom":makeQuery(id+"F20.opPattern","COPY",BODY,{"derivedFrom":makeQuery(id+"F19.opPattern","COPY",BODY,{"derivedFrom":makeQuery(id+"F18.opPattern","COPY",BODY,{"derivedFrom":makeQuery(id+"F1.opExtrude","SWEPT_BODY",BODY,{"disambiguationData":[OSD([sQuery(id+"F0.wireOp",EDGE,"E0")])]}),"instanceName":"1"}),"instanceName":"1"}),"instanceName":"1"}),"instanceName":"1"}),"instanceName":"1"}),"instanceName":"1"}),"instanceName":"1"}),"instanceName":"1"}),"instanceName":"1"}),"instanceName":"1"}),"instanceName":"1"}),"instanceName":"1"}),"instanceName":"1"}),"instanceName":"1"}),"instanceName":"1"}),"instanceName":"1"}),"instanceName":"1"}),"instanceName":"1"}),"instanceName":"1"});
            transform(context, id + "F37", {"entities" : qUnion([Q0]), "transformType" : TransformType.TRANSLATION_3D, "dx" : 3330 * mm, "dy" : 0 * mm, "dz" : 0 * mm, "makeCopy" : true});
        }
        {
            var Q0;
            Q0=makeQuery(id+"F37.opPattern","COPY",BODY,{"derivedFrom":makeQuery(id+"F36.opPattern","COPY",BODY,{"derivedFrom":makeQuery(id+"F35.opPattern","COPY",BODY,{"derivedFrom":makeQuery(id+"F34.opPattern","COPY",BODY,{"derivedFrom":makeQuery(id+"F33.opPattern","COPY",BODY,{"derivedFrom":makeQuery(id+"F32.opPattern","COPY",BODY,{"derivedFrom":makeQuery(id+"F31.opPattern","COPY",BODY,{"derivedFrom":makeQuery(id+"F30.opPattern","COPY",BODY,{"derivedFrom":makeQuery(id+"F29.opPattern","COPY",BODY,{"derivedFrom":makeQuery(id+"F28.opPattern","COPY",BODY,{"derivedFrom":makeQuery(id+"F27.opPattern","COPY",BODY,{"derivedFrom":makeQuery(id+"F26.opPattern","COPY",BODY,{"derivedFrom":makeQuery(id+"F25.opPattern","COPY",BODY,{"derivedFrom":makeQuery(id+"F24.opPattern","COPY",BODY,{"derivedFrom":makeQuery(id+"F23.opPattern","COPY",BODY,{"derivedFrom":makeQuery(id+"F22.opPattern","COPY",BODY,{"derivedFrom":makeQuery(id+"F21.opPattern","COPY",BODY,{"derivedFrom":makeQuery(id+"F20.opPattern","COPY",BODY,{"derivedFrom":makeQuery(id+"F19.opPattern","COPY",BODY,{"derivedFrom":makeQuery(id+"F18.opPattern","COPY",BODY,{"derivedFrom":makeQuery(id+"F1.opExtrude","SWEPT_BODY",BODY,{"disambiguationData":[OSD([sQuery(id+"F0.wireOp",EDGE,"E0")])]}),"instanceName":"1"}),"instanceName":"1"}),"instanceName":"1"}),"instanceName":"1"}),"instanceName":"1"}),"instanceName":"1"}),"instanceName":"1"}),"instanceName":"1"}),"instanceName":"1"}),"instanceName":"1"}),"instanceName":"1"}),"instanceName":"1"}),"instanceName":"1"}),"instanceName":"1"}),"instanceName":"1"}),"instanceName":"1"}),"instanceName":"1"}),"instanceName":"1"}),"instanceName":"1"}),"instanceName":"1"});
            transform(context, id + "F38", {"entities" : qUnion([Q0]), "transformType" : TransformType.TRANSLATION_3D, "dx" : 3330 * mm, "dy" : 0 * mm, "dz" : 0 * mm, "makeCopy" : true});
        }
        {
            var Q0;
            Q0=makeQuery(id+"F38.opPattern","COPY",BODY,{"derivedFrom":makeQuery(id+"F37.opPattern","COPY",BODY,{"derivedFrom":makeQuery(id+"F36.opPattern","COPY",BODY,{"derivedFrom":makeQuery(id+"F35.opPattern","COPY",BODY,{"derivedFrom":makeQuery(id+"F34.opPattern","COPY",BODY,{"derivedFrom":makeQuery(id+"F33.opPattern","COPY",BODY,{"derivedFrom":makeQuery(id+"F32.opPattern","COPY",BODY,{"derivedFrom":makeQuery(id+"F31.opPattern","COPY",BODY,{"derivedFrom":makeQuery(id+"F30.opPattern","COPY",BODY,{"derivedFrom":makeQuery(id+"F29.opPattern","COPY",BODY,{"derivedFrom":makeQuery(id+"F28.opPattern","COPY",BODY,{"derivedFrom":makeQuery(id+"F27.opPattern","COPY",BODY,{"derivedFrom":makeQuery(id+"F26.opPattern","COPY",BODY,{"derivedFrom":makeQuery(id+"F25.opPattern","COPY",BODY,{"derivedFrom":makeQuery(id+"F24.opPattern","COPY",BODY,{"derivedFrom":makeQuery(id+"F23.opPattern","COPY",BODY,{"derivedFrom":makeQuery(id+"F22.opPattern","COPY",BODY,{"derivedFrom":makeQuery(id+"F21.opPattern","COPY",BODY,{"derivedFrom":makeQuery(id+"F20.opPattern","COPY",BODY,{"derivedFrom":makeQuery(id+"F19.opPattern","COPY",BODY,{"derivedFrom":makeQuery(id+"F18.opPattern","COPY",BODY,{"derivedFrom":makeQuery(id+"F1.opExtrude","SWEPT_BODY",BODY,{"disambiguationData":[OSD([sQuery(id+"F0.wireOp",EDGE,"E0")])]}),"instanceName":"1"}),"instanceName":"1"}),"instanceName":"1"}),"instanceName":"1"}),"instanceName":"1"}),"instanceName":"1"}),"instanceName":"1"}),"instanceName":"1"}),"instanceName":"1"}),"instanceName":"1"}),"instanceName":"1"}),"instanceName":"1"}),"instanceName":"1"}),"instanceName":"1"}),"instanceName":"1"}),"instanceName":"1"}),"instanceName":"1"}),"instanceName":"1"}),"instanceName":"1"}),"instanceName":"1"}),"instanceName":"1"});
            transform(context, id + "F39", {"entities" : qUnion([Q0]), "transformType" : TransformType.TRANSLATION_3D, "dx" : 0 * mm, "dy" : -3330 * mm, "dz" : 0 * mm, "makeCopy" : true});
        }
        {
            var Q0;
            Q0=makeQuery(id+"F39.opPattern","COPY",BODY,{"derivedFrom":makeQuery(id+"F38.opPattern","COPY",BODY,{"derivedFrom":makeQuery(id+"F37.opPattern","COPY",BODY,{"derivedFrom":makeQuery(id+"F36.opPattern","COPY",BODY,{"derivedFrom":makeQuery(id+"F35.opPattern","COPY",BODY,{"derivedFrom":makeQuery(id+"F34.opPattern","COPY",BODY,{"derivedFrom":makeQuery(id+"F33.opPattern","COPY",BODY,{"derivedFrom":makeQuery(id+"F32.opPattern","COPY",BODY,{"derivedFrom":makeQuery(id+"F31.opPattern","COPY",BODY,{"derivedFrom":makeQuery(id+"F30.opPattern","COPY",BODY,{"derivedFrom":makeQuery(id+"F29.opPattern","COPY",BODY,{"derivedFrom":makeQuery(id+"F28.opPattern","COPY",BODY,{"derivedFrom":makeQuery(id+"F27.opPattern","COPY",BODY,{"derivedFrom":makeQuery(id+"F26.opPattern","COPY",BODY,{"derivedFrom":makeQuery(id+"F25.opPattern","COPY",BODY,{"derivedFrom":makeQuery(id+"F24.opPattern","COPY",BODY,{"derivedFrom":makeQuery(id+"F23.opPattern","COPY",BODY,{"derivedFrom":makeQuery(id+"F22.opPattern","COPY",BODY,{"derivedFrom":makeQuery(id+"F21.opPattern","COPY",BODY,{"derivedFrom":makeQuery(id+"F20.opPattern","COPY",BODY,{"derivedFrom":makeQuery(id+"F19.opPattern","COPY",BODY,{"derivedFrom":makeQuery(id+"F18.opPattern","COPY",BODY,{"derivedFrom":makeQuery(id+"F1.opExtrude","SWEPT_BODY",BODY,{"disambiguationData":[OSD([sQuery(id+"F0.wireOp",EDGE,"E0")])]}),"instanceName":"1"}),"instanceName":"1"}),"instanceName":"1"}),"instanceName":"1"}),"instanceName":"1"}),"instanceName":"1"}),"instanceName":"1"}),"instanceName":"1"}),"instanceName":"1"}),"instanceName":"1"}),"instanceName":"1"}),"instanceName":"1"}),"instanceName":"1"}),"instanceName":"1"}),"instanceName":"1"}),"instanceName":"1"}),"instanceName":"1"}),"instanceName":"1"}),"instanceName":"1"}),"instanceName":"1"}),"instanceName":"1"}),"instanceName":"1"});
            deleteBodies(context, id + "F40", {"entities" : qUnion([Q0])});
        }
        {
            var Q0;
            Q0=makeQuery(id+"F38.opPattern","COPY",BODY,{"derivedFrom":makeQuery(id+"F37.opPattern","COPY",BODY,{"derivedFrom":makeQuery(id+"F36.opPattern","COPY",BODY,{"derivedFrom":makeQuery(id+"F35.opPattern","COPY",BODY,{"derivedFrom":makeQuery(id+"F34.opPattern","COPY",BODY,{"derivedFrom":makeQuery(id+"F33.opPattern","COPY",BODY,{"derivedFrom":makeQuery(id+"F32.opPattern","COPY",BODY,{"derivedFrom":makeQuery(id+"F31.opPattern","COPY",BODY,{"derivedFrom":makeQuery(id+"F30.opPattern","COPY",BODY,{"derivedFrom":makeQuery(id+"F29.opPattern","COPY",BODY,{"derivedFrom":makeQuery(id+"F28.opPattern","COPY",BODY,{"derivedFrom":makeQuery(id+"F27.opPattern","COPY",BODY,{"derivedFrom":makeQuery(id+"F26.opPattern","COPY",BODY,{"derivedFrom":makeQuery(id+"F25.opPattern","COPY",BODY,{"derivedFrom":makeQuery(id+"F24.opPattern","COPY",BODY,{"derivedFrom":makeQuery(id+"F23.opPattern","COPY",BODY,{"derivedFrom":makeQuery(id+"F22.opPattern","COPY",BODY,{"derivedFrom":makeQuery(id+"F21.opPattern","COPY",BODY,{"derivedFrom":makeQuery(id+"F20.opPattern","COPY",BODY,{"derivedFrom":makeQuery(id+"F19.opPattern","COPY",BODY,{"derivedFrom":makeQuery(id+"F18.opPattern","COPY",BODY,{"derivedFrom":makeQuery(id+"F1.opExtrude","SWEPT_BODY",BODY,{"disambiguationData":[OSD([sQuery(id+"F0.wireOp",EDGE,"E0")])]}),"instanceName":"1"}),"instanceName":"1"}),"instanceName":"1"}),"instanceName":"1"}),"instanceName":"1"}),"instanceName":"1"}),"instanceName":"1"}),"instanceName":"1"}),"instanceName":"1"}),"instanceName":"1"}),"instanceName":"1"}),"instanceName":"1"}),"instanceName":"1"}),"instanceName":"1"}),"instanceName":"1"}),"instanceName":"1"}),"instanceName":"1"}),"instanceName":"1"}),"instanceName":"1"}),"instanceName":"1"}),"instanceName":"1"});
            transform(context, id + "F41", {"entities" : qUnion([Q0]), "transformType" : TransformType.TRANSLATION_3D, "dx" : 3330 * mm, "dy" : 0 * mm, "dz" : 0 * mm, "makeCopy" : true});
        }
        {
            var Q0;
            Q0=makeQuery(id+"F41.opPattern","COPY",BODY,{"derivedFrom":makeQuery(id+"F38.opPattern","COPY",BODY,{"derivedFrom":makeQuery(id+"F37.opPattern","COPY",BODY,{"derivedFrom":makeQuery(id+"F36.opPattern","COPY",BODY,{"derivedFrom":makeQuery(id+"F35.opPattern","COPY",BODY,{"derivedFrom":makeQuery(id+"F34.opPattern","COPY",BODY,{"derivedFrom":makeQuery(id+"F33.opPattern","COPY",BODY,{"derivedFrom":makeQuery(id+"F32.opPattern","COPY",BODY,{"derivedFrom":makeQuery(id+"F31.opPattern","COPY",BODY,{"derivedFrom":makeQuery(id+"F30.opPattern","COPY",BODY,{"derivedFrom":makeQuery(id+"F29.opPattern","COPY",BODY,{"derivedFrom":makeQuery(id+"F28.opPattern","COPY",BODY,{"derivedFrom":makeQuery(id+"F27.opPattern","COPY",BODY,{"derivedFrom":makeQuery(id+"F26.opPattern","COPY",BODY,{"derivedFrom":makeQuery(id+"F25.opPattern","COPY",BODY,{"derivedFrom":makeQuery(id+"F24.opPattern","COPY",BODY,{"derivedFrom":makeQuery(id+"F23.opPattern","COPY",BODY,{"derivedFrom":makeQuery(id+"F22.opPattern","COPY",BODY,{"derivedFrom":makeQuery(id+"F21.opPattern","COPY",BODY,{"derivedFrom":makeQuery(id+"F20.opPattern","COPY",BODY,{"derivedFrom":makeQuery(id+"F19.opPattern","COPY",BODY,{"derivedFrom":makeQuery(id+"F18.opPattern","COPY",BODY,{"derivedFrom":makeQuery(id+"F1.opExtrude","SWEPT_BODY",BODY,{"disambiguationData":[OSD([sQuery(id+"F0.wireOp",EDGE,"E0")])]}),"instanceName":"1"}),"instanceName":"1"}),"instanceName":"1"}),"instanceName":"1"}),"instanceName":"1"}),"instanceName":"1"}),"instanceName":"1"}),"instanceName":"1"}),"instanceName":"1"}),"instanceName":"1"}),"instanceName":"1"}),"instanceName":"1"}),"instanceName":"1"}),"instanceName":"1"}),"instanceName":"1"}),"instanceName":"1"}),"instanceName":"1"}),"instanceName":"1"}),"instanceName":"1"}),"instanceName":"1"}),"instanceName":"1"}),"instanceName":"1"});
            transform(context, id + "F42", {"entities" : qUnion([Q0]), "transformType" : TransformType.TRANSLATION_3D, "dx" : 0 * mm, "dy" : -3330 * mm, "dz" : 0 * mm, "makeCopy" : true});
        }
        {
            var Q0;
            Q0=makeQuery(id+"F42.opPattern","COPY",BODY,{"derivedFrom":makeQuery(id+"F41.opPattern","COPY",BODY,{"derivedFrom":makeQuery(id+"F38.opPattern","COPY",BODY,{"derivedFrom":makeQuery(id+"F37.opPattern","COPY",BODY,{"derivedFrom":makeQuery(id+"F36.opPattern","COPY",BODY,{"derivedFrom":makeQuery(id+"F35.opPattern","COPY",BODY,{"derivedFrom":makeQuery(id+"F34.opPattern","COPY",BODY,{"derivedFrom":makeQuery(id+"F33.opPattern","COPY",BODY,{"derivedFrom":makeQuery(id+"F32.opPattern","COPY",BODY,{"derivedFrom":makeQuery(id+"F31.opPattern","COPY",BODY,{"derivedFrom":makeQuery(id+"F30.opPattern","COPY",BODY,{"derivedFrom":makeQuery(id+"F29.opPattern","COPY",BODY,{"derivedFrom":makeQuery(id+"F28.opPattern","COPY",BODY,{"derivedFrom":makeQuery(id+"F27.opPattern","COPY",BODY,{"derivedFrom":makeQuery(id+"F26.opPattern","COPY",BODY,{"derivedFrom":makeQuery(id+"F25.opPattern","COPY",BODY,{"derivedFrom":makeQuery(id+"F24.opPattern","COPY",BODY,{"derivedFrom":makeQuery(id+"F23.opPattern","COPY",BODY,{"derivedFrom":makeQuery(id+"F22.opPattern","COPY",BODY,{"derivedFrom":makeQuery(id+"F21.opPattern","COPY",BODY,{"derivedFrom":makeQuery(id+"F20.opPattern","COPY",BODY,{"derivedFrom":makeQuery(id+"F19.opPattern","COPY",BODY,{"derivedFrom":makeQuery(id+"F18.opPattern","COPY",BODY,{"derivedFrom":makeQuery(id+"F1.opExtrude","SWEPT_BODY",BODY,{"disambiguationData":[OSD([sQuery(id+"F0.wireOp",EDGE,"E0")])]}),"instanceName":"1"}),"instanceName":"1"}),"instanceName":"1"}),"instanceName":"1"}),"instanceName":"1"}),"instanceName":"1"}),"instanceName":"1"}),"instanceName":"1"}),"instanceName":"1"}),"instanceName":"1"}),"instanceName":"1"}),"instanceName":"1"}),"instanceName":"1"}),"instanceName":"1"}),"instanceName":"1"}),"instanceName":"1"}),"instanceName":"1"}),"instanceName":"1"}),"instanceName":"1"}),"instanceName":"1"}),"instanceName":"1"}),"instanceName":"1"}),"instanceName":"1"});
            transform(context, id + "F43", {"entities" : qUnion([Q0]), "transformType" : TransformType.TRANSLATION_3D, "dx" : 0 * mm, "dy" : -3330 * mm, "dz" : 0 * mm, "makeCopy" : true});
        }
        {
            var Q0;
            Q0=makeQuery(id+"F43.opPattern","COPY",BODY,{"derivedFrom":makeQuery(id+"F42.opPattern","COPY",BODY,{"derivedFrom":makeQuery(id+"F41.opPattern","COPY",BODY,{"derivedFrom":makeQuery(id+"F38.opPattern","COPY",BODY,{"derivedFrom":makeQuery(id+"F37.opPattern","COPY",BODY,{"derivedFrom":makeQuery(id+"F36.opPattern","COPY",BODY,{"derivedFrom":makeQuery(id+"F35.opPattern","COPY",BODY,{"derivedFrom":makeQuery(id+"F34.opPattern","COPY",BODY,{"derivedFrom":makeQuery(id+"F33.opPattern","COPY",BODY,{"derivedFrom":makeQuery(id+"F32.opPattern","COPY",BODY,{"derivedFrom":makeQuery(id+"F31.opPattern","COPY",BODY,{"derivedFrom":makeQuery(id+"F30.opPattern","COPY",BODY,{"derivedFrom":makeQuery(id+"F29.opPattern","COPY",BODY,{"derivedFrom":makeQuery(id+"F28.opPattern","COPY",BODY,{"derivedFrom":makeQuery(id+"F27.opPattern","COPY",BODY,{"derivedFrom":makeQuery(id+"F26.opPattern","COPY",BODY,{"derivedFrom":makeQuery(id+"F25.opPattern","COPY",BODY,{"derivedFrom":makeQuery(id+"F24.opPattern","COPY",BODY,{"derivedFrom":makeQuery(id+"F23.opPattern","COPY",BODY,{"derivedFrom":makeQuery(id+"F22.opPattern","COPY",BODY,{"derivedFrom":makeQuery(id+"F21.opPattern","COPY",BODY,{"derivedFrom":makeQuery(id+"F20.opPattern","COPY",BODY,{"derivedFrom":makeQuery(id+"F19.opPattern","COPY",BODY,{"derivedFrom":makeQuery(id+"F18.opPattern","COPY",BODY,{"derivedFrom":makeQuery(id+"F1.opExtrude","SWEPT_BODY",BODY,{"disambiguationData":[OSD([sQuery(id+"F0.wireOp",EDGE,"E0")])]}),"instanceName":"1"}),"instanceName":"1"}),"instanceName":"1"}),"instanceName":"1"}),"instanceName":"1"}),"instanceName":"1"}),"instanceName":"1"}),"instanceName":"1"}),"instanceName":"1"}),"instanceName":"1"}),"instanceName":"1"}),"instanceName":"1"}),"instanceName":"1"}),"instanceName":"1"}),"instanceName":"1"}),"instanceName":"1"}),"instanceName":"1"}),"instanceName":"1"}),"instanceName":"1"}),"instanceName":"1"}),"instanceName":"1"}),"instanceName":"1"}),"instanceName":"1"}),"instanceName":"1"});
            transform(context, id + "F44", {"entities" : qUnion([Q0]), "transformType" : TransformType.TRANSLATION_3D, "dx" : 0 * mm, "dy" : -3330 * mm, "dz" : 0 * mm, "makeCopy" : true});
        }
        {
            var Q0;
            Q0=makeQuery(id+"F44.opPattern","COPY",BODY,{"derivedFrom":makeQuery(id+"F43.opPattern","COPY",BODY,{"derivedFrom":makeQuery(id+"F42.opPattern","COPY",BODY,{"derivedFrom":makeQuery(id+"F41.opPattern","COPY",BODY,{"derivedFrom":makeQuery(id+"F38.opPattern","COPY",BODY,{"derivedFrom":makeQuery(id+"F37.opPattern","COPY",BODY,{"derivedFrom":makeQuery(id+"F36.opPattern","COPY",BODY,{"derivedFrom":makeQuery(id+"F35.opPattern","COPY",BODY,{"derivedFrom":makeQuery(id+"F34.opPattern","COPY",BODY,{"derivedFrom":makeQuery(id+"F33.opPattern","COPY",BODY,{"derivedFrom":makeQuery(id+"F32.opPattern","COPY",BODY,{"derivedFrom":makeQuery(id+"F31.opPattern","COPY",BODY,{"derivedFrom":makeQuery(id+"F30.opPattern","COPY",BODY,{"derivedFrom":makeQuery(id+"F29.opPattern","COPY",BODY,{"derivedFrom":makeQuery(id+"F28.opPattern","COPY",BODY,{"derivedFrom":makeQuery(id+"F27.opPattern","COPY",BODY,{"derivedFrom":makeQuery(id+"F26.opPattern","COPY",BODY,{"derivedFrom":makeQuery(id+"F25.opPattern","COPY",BODY,{"derivedFrom":makeQuery(id+"F24.opPattern","COPY",BODY,{"derivedFrom":makeQuery(id+"F23.opPattern","COPY",BODY,{"derivedFrom":makeQuery(id+"F22.opPattern","COPY",BODY,{"derivedFrom":makeQuery(id+"F21.opPattern","COPY",BODY,{"derivedFrom":makeQuery(id+"F20.opPattern","COPY",BODY,{"derivedFrom":makeQuery(id+"F19.opPattern","COPY",BODY,{"derivedFrom":makeQuery(id+"F18.opPattern","COPY",BODY,{"derivedFrom":makeQuery(id+"F1.opExtrude","SWEPT_BODY",BODY,{"disambiguationData":[OSD([sQuery(id+"F0.wireOp",EDGE,"E0")])]}),"instanceName":"1"}),"instanceName":"1"}),"instanceName":"1"}),"instanceName":"1"}),"instanceName":"1"}),"instanceName":"1"}),"instanceName":"1"}),"instanceName":"1"}),"instanceName":"1"}),"instanceName":"1"}),"instanceName":"1"}),"instanceName":"1"}),"instanceName":"1"}),"instanceName":"1"}),"instanceName":"1"}),"instanceName":"1"}),"instanceName":"1"}),"instanceName":"1"}),"instanceName":"1"}),"instanceName":"1"}),"instanceName":"1"}),"instanceName":"1"}),"instanceName":"1"}),"instanceName":"1"}),"instanceName":"1"});
            transform(context, id + "F45", {"entities" : qUnion([Q0]), "transformType" : TransformType.TRANSLATION_3D, "dx" : 0 * mm, "dy" : -3330 * mm, "dz" : 0 * mm, "makeCopy" : true});
        }
        {
            var Q0;
            Q0=makeQuery(id+"F45.opPattern","COPY",BODY,{"derivedFrom":makeQuery(id+"F44.opPattern","COPY",BODY,{"derivedFrom":makeQuery(id+"F43.opPattern","COPY",BODY,{"derivedFrom":makeQuery(id+"F42.opPattern","COPY",BODY,{"derivedFrom":makeQuery(id+"F41.opPattern","COPY",BODY,{"derivedFrom":makeQuery(id+"F38.opPattern","COPY",BODY,{"derivedFrom":makeQuery(id+"F37.opPattern","COPY",BODY,{"derivedFrom":makeQuery(id+"F36.opPattern","COPY",BODY,{"derivedFrom":makeQuery(id+"F35.opPattern","COPY",BODY,{"derivedFrom":makeQuery(id+"F34.opPattern","COPY",BODY,{"derivedFrom":makeQuery(id+"F33.opPattern","COPY",BODY,{"derivedFrom":makeQuery(id+"F32.opPattern","COPY",BODY,{"derivedFrom":makeQuery(id+"F31.opPattern","COPY",BODY,{"derivedFrom":makeQuery(id+"F30.opPattern","COPY",BODY,{"derivedFrom":makeQuery(id+"F29.opPattern","COPY",BODY,{"derivedFrom":makeQuery(id+"F28.opPattern","COPY",BODY,{"derivedFrom":makeQuery(id+"F27.opPattern","COPY",BODY,{"derivedFrom":makeQuery(id+"F26.opPattern","COPY",BODY,{"derivedFrom":makeQuery(id+"F25.opPattern","COPY",BODY,{"derivedFrom":makeQuery(id+"F24.opPattern","COPY",BODY,{"derivedFrom":makeQuery(id+"F23.opPattern","COPY",BODY,{"derivedFrom":makeQuery(id+"F22.opPattern","COPY",BODY,{"derivedFrom":makeQuery(id+"F21.opPattern","COPY",BODY,{"derivedFrom":makeQuery(id+"F20.opPattern","COPY",BODY,{"derivedFrom":makeQuery(id+"F19.opPattern","COPY",BODY,{"derivedFrom":makeQuery(id+"F18.opPattern","COPY",BODY,{"derivedFrom":makeQuery(id+"F1.opExtrude","SWEPT_BODY",BODY,{"disambiguationData":[OSD([sQuery(id+"F0.wireOp",EDGE,"E0")])]}),"instanceName":"1"}),"instanceName":"1"}),"instanceName":"1"}),"instanceName":"1"}),"instanceName":"1"}),"instanceName":"1"}),"instanceName":"1"}),"instanceName":"1"}),"instanceName":"1"}),"instanceName":"1"}),"instanceName":"1"}),"instanceName":"1"}),"instanceName":"1"}),"instanceName":"1"}),"instanceName":"1"}),"instanceName":"1"}),"instanceName":"1"}),"instanceName":"1"}),"instanceName":"1"}),"instanceName":"1"}),"instanceName":"1"}),"instanceName":"1"}),"instanceName":"1"}),"instanceName":"1"}),"instanceName":"1"}),"instanceName":"1"});
            transform(context, id + "F46", {"entities" : qUnion([Q0]), "transformType" : TransformType.TRANSLATION_3D, "dx" : 0 * mm, "dy" : -3330 * mm, "dz" : 0 * mm, "makeCopy" : true});
        }
        {
            var Q0;
            Q0=makeQuery(id+"F46.opPattern","COPY",BODY,{"derivedFrom":makeQuery(id+"F45.opPattern","COPY",BODY,{"derivedFrom":makeQuery(id+"F44.opPattern","COPY",BODY,{"derivedFrom":makeQuery(id+"F43.opPattern","COPY",BODY,{"derivedFrom":makeQuery(id+"F42.opPattern","COPY",BODY,{"derivedFrom":makeQuery(id+"F41.opPattern","COPY",BODY,{"derivedFrom":makeQuery(id+"F38.opPattern","COPY",BODY,{"derivedFrom":makeQuery(id+"F37.opPattern","COPY",BODY,{"derivedFrom":makeQuery(id+"F36.opPattern","COPY",BODY,{"derivedFrom":makeQuery(id+"F35.opPattern","COPY",BODY,{"derivedFrom":makeQuery(id+"F34.opPattern","COPY",BODY,{"derivedFrom":makeQuery(id+"F33.opPattern","COPY",BODY,{"derivedFrom":makeQuery(id+"F32.opPattern","COPY",BODY,{"derivedFrom":makeQuery(id+"F31.opPattern","COPY",BODY,{"derivedFrom":makeQuery(id+"F30.opPattern","COPY",BODY,{"derivedFrom":makeQuery(id+"F29.opPattern","COPY",BODY,{"derivedFrom":makeQuery(id+"F28.opPattern","COPY",BODY,{"derivedFrom":makeQuery(id+"F27.opPattern","COPY",BODY,{"derivedFrom":makeQuery(id+"F26.opPattern","COPY",BODY,{"derivedFrom":makeQuery(id+"F25.opPattern","COPY",BODY,{"derivedFrom":makeQuery(id+"F24.opPattern","COPY",BODY,{"derivedFrom":makeQuery(id+"F23.opPattern","COPY",BODY,{"derivedFrom":makeQuery(id+"F22.opPattern","COPY",BODY,{"derivedFrom":makeQuery(id+"F21.opPattern","COPY",BODY,{"derivedFrom":makeQuery(id+"F20.opPattern","COPY",BODY,{"derivedFrom":makeQuery(id+"F19.opPattern","COPY",BODY,{"derivedFrom":makeQuery(id+"F18.opPattern","COPY",BODY,{"derivedFrom":makeQuery(id+"F1.opExtrude","SWEPT_BODY",BODY,{"disambiguationData":[OSD([sQuery(id+"F0.wireOp",EDGE,"E0")])]}),"instanceName":"1"}),"instanceName":"1"}),"instanceName":"1"}),"instanceName":"1"}),"instanceName":"1"}),"instanceName":"1"}),"instanceName":"1"}),"instanceName":"1"}),"instanceName":"1"}),"instanceName":"1"}),"instanceName":"1"}),"instanceName":"1"}),"instanceName":"1"}),"instanceName":"1"}),"instanceName":"1"}),"instanceName":"1"}),"instanceName":"1"}),"instanceName":"1"}),"instanceName":"1"}),"instanceName":"1"}),"instanceName":"1"}),"instanceName":"1"}),"instanceName":"1"}),"instanceName":"1"}),"instanceName":"1"}),"instanceName":"1"}),"instanceName":"1"});
            deleteBodies(context, id + "F47", {"entities" : qUnion([Q0])});
        }
        {
            var Q0;
            Q0=makeQuery(id+"F45.opPattern","COPY",BODY,{"derivedFrom":makeQuery(id+"F44.opPattern","COPY",BODY,{"derivedFrom":makeQuery(id+"F43.opPattern","COPY",BODY,{"derivedFrom":makeQuery(id+"F42.opPattern","COPY",BODY,{"derivedFrom":makeQuery(id+"F41.opPattern","COPY",BODY,{"derivedFrom":makeQuery(id+"F38.opPattern","COPY",BODY,{"derivedFrom":makeQuery(id+"F37.opPattern","COPY",BODY,{"derivedFrom":makeQuery(id+"F36.opPattern","COPY",BODY,{"derivedFrom":makeQuery(id+"F35.opPattern","COPY",BODY,{"derivedFrom":makeQuery(id+"F34.opPattern","COPY",BODY,{"derivedFrom":makeQuery(id+"F33.opPattern","COPY",BODY,{"derivedFrom":makeQuery(id+"F32.opPattern","COPY",BODY,{"derivedFrom":makeQuery(id+"F31.opPattern","COPY",BODY,{"derivedFrom":makeQuery(id+"F30.opPattern","COPY",BODY,{"derivedFrom":makeQuery(id+"F29.opPattern","COPY",BODY,{"derivedFrom":makeQuery(id+"F28.opPattern","COPY",BODY,{"derivedFrom":makeQuery(id+"F27.opPattern","COPY",BODY,{"derivedFrom":makeQuery(id+"F26.opPattern","COPY",BODY,{"derivedFrom":makeQuery(id+"F25.opPattern","COPY",BODY,{"derivedFrom":makeQuery(id+"F24.opPattern","COPY",BODY,{"derivedFrom":makeQuery(id+"F23.opPattern","COPY",BODY,{"derivedFrom":makeQuery(id+"F22.opPattern","COPY",BODY,{"derivedFrom":makeQuery(id+"F21.opPattern","COPY",BODY,{"derivedFrom":makeQuery(id+"F20.opPattern","COPY",BODY,{"derivedFrom":makeQuery(id+"F19.opPattern","COPY",BODY,{"derivedFrom":makeQuery(id+"F18.opPattern","COPY",BODY,{"derivedFrom":makeQuery(id+"F1.opExtrude","SWEPT_BODY",BODY,{"disambiguationData":[OSD([sQuery(id+"F0.wireOp",EDGE,"E0")])]}),"instanceName":"1"}),"instanceName":"1"}),"instanceName":"1"}),"instanceName":"1"}),"instanceName":"1"}),"instanceName":"1"}),"instanceName":"1"}),"instanceName":"1"}),"instanceName":"1"}),"instanceName":"1"}),"instanceName":"1"}),"instanceName":"1"}),"instanceName":"1"}),"instanceName":"1"}),"instanceName":"1"}),"instanceName":"1"}),"instanceName":"1"}),"instanceName":"1"}),"instanceName":"1"}),"instanceName":"1"}),"instanceName":"1"}),"instanceName":"1"}),"instanceName":"1"}),"instanceName":"1"}),"instanceName":"1"}),"instanceName":"1"});
            deleteBodies(context, id + "F48", {"entities" : qUnion([Q0])});
        }
        {
            var Q0;
            Q0=makeQuery(id+"F42.opPattern","COPY",BODY,{"derivedFrom":makeQuery(id+"F41.opPattern","COPY",BODY,{"derivedFrom":makeQuery(id+"F38.opPattern","COPY",BODY,{"derivedFrom":makeQuery(id+"F37.opPattern","COPY",BODY,{"derivedFrom":makeQuery(id+"F36.opPattern","COPY",BODY,{"derivedFrom":makeQuery(id+"F35.opPattern","COPY",BODY,{"derivedFrom":makeQuery(id+"F34.opPattern","COPY",BODY,{"derivedFrom":makeQuery(id+"F33.opPattern","COPY",BODY,{"derivedFrom":makeQuery(id+"F32.opPattern","COPY",BODY,{"derivedFrom":makeQuery(id+"F31.opPattern","COPY",BODY,{"derivedFrom":makeQuery(id+"F30.opPattern","COPY",BODY,{"derivedFrom":makeQuery(id+"F29.opPattern","COPY",BODY,{"derivedFrom":makeQuery(id+"F28.opPattern","COPY",BODY,{"derivedFrom":makeQuery(id+"F27.opPattern","COPY",BODY,{"derivedFrom":makeQuery(id+"F26.opPattern","COPY",BODY,{"derivedFrom":makeQuery(id+"F25.opPattern","COPY",BODY,{"derivedFrom":makeQuery(id+"F24.opPattern","COPY",BODY,{"derivedFrom":makeQuery(id+"F23.opPattern","COPY",BODY,{"derivedFrom":makeQuery(id+"F22.opPattern","COPY",BODY,{"derivedFrom":makeQuery(id+"F21.opPattern","COPY",BODY,{"derivedFrom":makeQuery(id+"F20.opPattern","COPY",BODY,{"derivedFrom":makeQuery(id+"F19.opPattern","COPY",BODY,{"derivedFrom":makeQuery(id+"F18.opPattern","COPY",BODY,{"derivedFrom":makeQuery(id+"F1.opExtrude","SWEPT_BODY",BODY,{"disambiguationData":[OSD([sQuery(id+"F0.wireOp",EDGE,"E0")])]}),"instanceName":"1"}),"instanceName":"1"}),"instanceName":"1"}),"instanceName":"1"}),"instanceName":"1"}),"instanceName":"1"}),"instanceName":"1"}),"instanceName":"1"}),"instanceName":"1"}),"instanceName":"1"}),"instanceName":"1"}),"instanceName":"1"}),"instanceName":"1"}),"instanceName":"1"}),"instanceName":"1"}),"instanceName":"1"}),"instanceName":"1"}),"instanceName":"1"}),"instanceName":"1"}),"instanceName":"1"}),"instanceName":"1"}),"instanceName":"1"}),"instanceName":"1"});
            var Q1;
            Q1=makeQuery(id+"F43.opPattern","COPY",BODY,{"derivedFrom":makeQuery(id+"F42.opPattern","COPY",BODY,{"derivedFrom":makeQuery(id+"F41.opPattern","COPY",BODY,{"derivedFrom":makeQuery(id+"F38.opPattern","COPY",BODY,{"derivedFrom":makeQuery(id+"F37.opPattern","COPY",BODY,{"derivedFrom":makeQuery(id+"F36.opPattern","COPY",BODY,{"derivedFrom":makeQuery(id+"F35.opPattern","COPY",BODY,{"derivedFrom":makeQuery(id+"F34.opPattern","COPY",BODY,{"derivedFrom":makeQuery(id+"F33.opPattern","COPY",BODY,{"derivedFrom":makeQuery(id+"F32.opPattern","COPY",BODY,{"derivedFrom":makeQuery(id+"F31.opPattern","COPY",BODY,{"derivedFrom":makeQuery(id+"F30.opPattern","COPY",BODY,{"derivedFrom":makeQuery(id+"F29.opPattern","COPY",BODY,{"derivedFrom":makeQuery(id+"F28.opPattern","COPY",BODY,{"derivedFrom":makeQuery(id+"F27.opPattern","COPY",BODY,{"derivedFrom":makeQuery(id+"F26.opPattern","COPY",BODY,{"derivedFrom":makeQuery(id+"F25.opPattern","COPY",BODY,{"derivedFrom":makeQuery(id+"F24.opPattern","COPY",BODY,{"derivedFrom":makeQuery(id+"F23.opPattern","COPY",BODY,{"derivedFrom":makeQuery(id+"F22.opPattern","COPY",BODY,{"derivedFrom":makeQuery(id+"F21.opPattern","COPY",BODY,{"derivedFrom":makeQuery(id+"F20.opPattern","COPY",BODY,{"derivedFrom":makeQuery(id+"F19.opPattern","COPY",BODY,{"derivedFrom":makeQuery(id+"F18.opPattern","COPY",BODY,{"derivedFrom":makeQuery(id+"F1.opExtrude","SWEPT_BODY",BODY,{"disambiguationData":[OSD([sQuery(id+"F0.wireOp",EDGE,"E0")])]}),"instanceName":"1"}),"instanceName":"1"}),"instanceName":"1"}),"instanceName":"1"}),"instanceName":"1"}),"instanceName":"1"}),"instanceName":"1"}),"instanceName":"1"}),"instanceName":"1"}),"instanceName":"1"}),"instanceName":"1"}),"instanceName":"1"}),"instanceName":"1"}),"instanceName":"1"}),"instanceName":"1"}),"instanceName":"1"}),"instanceName":"1"}),"instanceName":"1"}),"instanceName":"1"}),"instanceName":"1"}),"instanceName":"1"}),"instanceName":"1"}),"instanceName":"1"}),"instanceName":"1"});
            var Q2;
            Q2=makeQuery(id+"F44.opPattern","COPY",BODY,{"derivedFrom":makeQuery(id+"F43.opPattern","COPY",BODY,{"derivedFrom":makeQuery(id+"F42.opPattern","COPY",BODY,{"derivedFrom":makeQuery(id+"F41.opPattern","COPY",BODY,{"derivedFrom":makeQuery(id+"F38.opPattern","COPY",BODY,{"derivedFrom":makeQuery(id+"F37.opPattern","COPY",BODY,{"derivedFrom":makeQuery(id+"F36.opPattern","COPY",BODY,{"derivedFrom":makeQuery(id+"F35.opPattern","COPY",BODY,{"derivedFrom":makeQuery(id+"F34.opPattern","COPY",BODY,{"derivedFrom":makeQuery(id+"F33.opPattern","COPY",BODY,{"derivedFrom":makeQuery(id+"F32.opPattern","COPY",BODY,{"derivedFrom":makeQuery(id+"F31.opPattern","COPY",BODY,{"derivedFrom":makeQuery(id+"F30.opPattern","COPY",BODY,{"derivedFrom":makeQuery(id+"F29.opPattern","COPY",BODY,{"derivedFrom":makeQuery(id+"F28.opPattern","COPY",BODY,{"derivedFrom":makeQuery(id+"F27.opPattern","COPY",BODY,{"derivedFrom":makeQuery(id+"F26.opPattern","COPY",BODY,{"derivedFrom":makeQuery(id+"F25.opPattern","COPY",BODY,{"derivedFrom":makeQuery(id+"F24.opPattern","COPY",BODY,{"derivedFrom":makeQuery(id+"F23.opPattern","COPY",BODY,{"derivedFrom":makeQuery(id+"F22.opPattern","COPY",BODY,{"derivedFrom":makeQuery(id+"F21.opPattern","COPY",BODY,{"derivedFrom":makeQuery(id+"F20.opPattern","COPY",BODY,{"derivedFrom":makeQuery(id+"F19.opPattern","COPY",BODY,{"derivedFrom":makeQuery(id+"F18.opPattern","COPY",BODY,{"derivedFrom":makeQuery(id+"F1.opExtrude","SWEPT_BODY",BODY,{"disambiguationData":[OSD([sQuery(id+"F0.wireOp",EDGE,"E0")])]}),"instanceName":"1"}),"instanceName":"1"}),"instanceName":"1"}),"instanceName":"1"}),"instanceName":"1"}),"instanceName":"1"}),"instanceName":"1"}),"instanceName":"1"}),"instanceName":"1"}),"instanceName":"1"}),"instanceName":"1"}),"instanceName":"1"}),"instanceName":"1"}),"instanceName":"1"}),"instanceName":"1"}),"instanceName":"1"}),"instanceName":"1"}),"instanceName":"1"}),"instanceName":"1"}),"instanceName":"1"}),"instanceName":"1"}),"instanceName":"1"}),"instanceName":"1"}),"instanceName":"1"}),"instanceName":"1"});
            deleteBodies(context, id + "F49", {"entities" : qUnion([Q0, Q1, Q2])});
        }
        {
            var Q0;
            Q0=makeQuery(id+"F41.opPattern","COPY",BODY,{"derivedFrom":makeQuery(id+"F38.opPattern","COPY",BODY,{"derivedFrom":makeQuery(id+"F37.opPattern","COPY",BODY,{"derivedFrom":makeQuery(id+"F36.opPattern","COPY",BODY,{"derivedFrom":makeQuery(id+"F35.opPattern","COPY",BODY,{"derivedFrom":makeQuery(id+"F34.opPattern","COPY",BODY,{"derivedFrom":makeQuery(id+"F33.opPattern","COPY",BODY,{"derivedFrom":makeQuery(id+"F32.opPattern","COPY",BODY,{"derivedFrom":makeQuery(id+"F31.opPattern","COPY",BODY,{"derivedFrom":makeQuery(id+"F30.opPattern","COPY",BODY,{"derivedFrom":makeQuery(id+"F29.opPattern","COPY",BODY,{"derivedFrom":makeQuery(id+"F28.opPattern","COPY",BODY,{"derivedFrom":makeQuery(id+"F27.opPattern","COPY",BODY,{"derivedFrom":makeQuery(id+"F26.opPattern","COPY",BODY,{"derivedFrom":makeQuery(id+"F25.opPattern","COPY",BODY,{"derivedFrom":makeQuery(id+"F24.opPattern","COPY",BODY,{"derivedFrom":makeQuery(id+"F23.opPattern","COPY",BODY,{"derivedFrom":makeQuery(id+"F22.opPattern","COPY",BODY,{"derivedFrom":makeQuery(id+"F21.opPattern","COPY",BODY,{"derivedFrom":makeQuery(id+"F20.opPattern","COPY",BODY,{"derivedFrom":makeQuery(id+"F19.opPattern","COPY",BODY,{"derivedFrom":makeQuery(id+"F18.opPattern","COPY",BODY,{"derivedFrom":makeQuery(id+"F1.opExtrude","SWEPT_BODY",BODY,{"disambiguationData":[OSD([sQuery(id+"F0.wireOp",EDGE,"E0")])]}),"instanceName":"1"}),"instanceName":"1"}),"instanceName":"1"}),"instanceName":"1"}),"instanceName":"1"}),"instanceName":"1"}),"instanceName":"1"}),"instanceName":"1"}),"instanceName":"1"}),"instanceName":"1"}),"instanceName":"1"}),"instanceName":"1"}),"instanceName":"1"}),"instanceName":"1"}),"instanceName":"1"}),"instanceName":"1"}),"instanceName":"1"}),"instanceName":"1"}),"instanceName":"1"}),"instanceName":"1"}),"instanceName":"1"}),"instanceName":"1"});
            transform(context, id + "F50", {"entities" : qUnion([Q0]), "transformType" : TransformType.TRANSLATION_3D, "dx" : 0 * mm, "dy" : -3500 * mm, "dz" : 0 * mm, "makeCopy" : true});
        }
        {
            var Q0;
            Q0=makeQuery(id+"F50.opPattern","COPY",BODY,{"derivedFrom":makeQuery(id+"F41.opPattern","COPY",BODY,{"derivedFrom":makeQuery(id+"F38.opPattern","COPY",BODY,{"derivedFrom":makeQuery(id+"F37.opPattern","COPY",BODY,{"derivedFrom":makeQuery(id+"F36.opPattern","COPY",BODY,{"derivedFrom":makeQuery(id+"F35.opPattern","COPY",BODY,{"derivedFrom":makeQuery(id+"F34.opPattern","COPY",BODY,{"derivedFrom":makeQuery(id+"F33.opPattern","COPY",BODY,{"derivedFrom":makeQuery(id+"F32.opPattern","COPY",BODY,{"derivedFrom":makeQuery(id+"F31.opPattern","COPY",BODY,{"derivedFrom":makeQuery(id+"F30.opPattern","COPY",BODY,{"derivedFrom":makeQuery(id+"F29.opPattern","COPY",BODY,{"derivedFrom":makeQuery(id+"F28.opPattern","COPY",BODY,{"derivedFrom":makeQuery(id+"F27.opPattern","COPY",BODY,{"derivedFrom":makeQuery(id+"F26.opPattern","COPY",BODY,{"derivedFrom":makeQuery(id+"F25.opPattern","COPY",BODY,{"derivedFrom":makeQuery(id+"F24.opPattern","COPY",BODY,{"derivedFrom":makeQuery(id+"F23.opPattern","COPY",BODY,{"derivedFrom":makeQuery(id+"F22.opPattern","COPY",BODY,{"derivedFrom":makeQuery(id+"F21.opPattern","COPY",BODY,{"derivedFrom":makeQuery(id+"F20.opPattern","COPY",BODY,{"derivedFrom":makeQuery(id+"F19.opPattern","COPY",BODY,{"derivedFrom":makeQuery(id+"F18.opPattern","COPY",BODY,{"derivedFrom":makeQuery(id+"F1.opExtrude","SWEPT_BODY",BODY,{"disambiguationData":[OSD([sQuery(id+"F0.wireOp",EDGE,"E0")])]}),"instanceName":"1"}),"instanceName":"1"}),"instanceName":"1"}),"instanceName":"1"}),"instanceName":"1"}),"instanceName":"1"}),"instanceName":"1"}),"instanceName":"1"}),"instanceName":"1"}),"instanceName":"1"}),"instanceName":"1"}),"instanceName":"1"}),"instanceName":"1"}),"instanceName":"1"}),"instanceName":"1"}),"instanceName":"1"}),"instanceName":"1"}),"instanceName":"1"}),"instanceName":"1"}),"instanceName":"1"}),"instanceName":"1"}),"instanceName":"1"}),"instanceName":"1"});
            transform(context, id + "F51", {"entities" : qUnion([Q0]), "transformType" : TransformType.TRANSLATION_3D, "dx" : 0 * mm, "dy" : -3500 * mm, "dz" : 0 * mm, "makeCopy" : true});
        }
        {
            var Q0;
            Q0=makeQuery(id+"F51.opPattern","COPY",BODY,{"derivedFrom":makeQuery(id+"F50.opPattern","COPY",BODY,{"derivedFrom":makeQuery(id+"F41.opPattern","COPY",BODY,{"derivedFrom":makeQuery(id+"F38.opPattern","COPY",BODY,{"derivedFrom":makeQuery(id+"F37.opPattern","COPY",BODY,{"derivedFrom":makeQuery(id+"F36.opPattern","COPY",BODY,{"derivedFrom":makeQuery(id+"F35.opPattern","COPY",BODY,{"derivedFrom":makeQuery(id+"F34.opPattern","COPY",BODY,{"derivedFrom":makeQuery(id+"F33.opPattern","COPY",BODY,{"derivedFrom":makeQuery(id+"F32.opPattern","COPY",BODY,{"derivedFrom":makeQuery(id+"F31.opPattern","COPY",BODY,{"derivedFrom":makeQuery(id+"F30.opPattern","COPY",BODY,{"derivedFrom":makeQuery(id+"F29.opPattern","COPY",BODY,{"derivedFrom":makeQuery(id+"F28.opPattern","COPY",BODY,{"derivedFrom":makeQuery(id+"F27.opPattern","COPY",BODY,{"derivedFrom":makeQuery(id+"F26.opPattern","COPY",BODY,{"derivedFrom":makeQuery(id+"F25.opPattern","COPY",BODY,{"derivedFrom":makeQuery(id+"F24.opPattern","COPY",BODY,{"derivedFrom":makeQuery(id+"F23.opPattern","COPY",BODY,{"derivedFrom":makeQuery(id+"F22.opPattern","COPY",BODY,{"derivedFrom":makeQuery(id+"F21.opPattern","COPY",BODY,{"derivedFrom":makeQuery(id+"F20.opPattern","COPY",BODY,{"derivedFrom":makeQuery(id+"F19.opPattern","COPY",BODY,{"derivedFrom":makeQuery(id+"F18.opPattern","COPY",BODY,{"derivedFrom":makeQuery(id+"F1.opExtrude","SWEPT_BODY",BODY,{"disambiguationData":[OSD([sQuery(id+"F0.wireOp",EDGE,"E0")])]}),"instanceName":"1"}),"instanceName":"1"}),"instanceName":"1"}),"instanceName":"1"}),"instanceName":"1"}),"instanceName":"1"}),"instanceName":"1"}),"instanceName":"1"}),"instanceName":"1"}),"instanceName":"1"}),"instanceName":"1"}),"instanceName":"1"}),"instanceName":"1"}),"instanceName":"1"}),"instanceName":"1"}),"instanceName":"1"}),"instanceName":"1"}),"instanceName":"1"}),"instanceName":"1"}),"instanceName":"1"}),"instanceName":"1"}),"instanceName":"1"}),"instanceName":"1"}),"instanceName":"1"});
            transform(context, id + "F52", {"entities" : qUnion([Q0]), "transformType" : TransformType.TRANSLATION_3D, "dx" : 0 * mm, "dy" : -3000 * mm, "dz" : 0 * mm, "makeCopy" : true});
        }
        {
            var Q0;
            Q0=makeQuery(id+"F52.opPattern","COPY",BODY,{"derivedFrom":makeQuery(id+"F51.opPattern","COPY",BODY,{"derivedFrom":makeQuery(id+"F50.opPattern","COPY",BODY,{"derivedFrom":makeQuery(id+"F41.opPattern","COPY",BODY,{"derivedFrom":makeQuery(id+"F38.opPattern","COPY",BODY,{"derivedFrom":makeQuery(id+"F37.opPattern","COPY",BODY,{"derivedFrom":makeQuery(id+"F36.opPattern","COPY",BODY,{"derivedFrom":makeQuery(id+"F35.opPattern","COPY",BODY,{"derivedFrom":makeQuery(id+"F34.opPattern","COPY",BODY,{"derivedFrom":makeQuery(id+"F33.opPattern","COPY",BODY,{"derivedFrom":makeQuery(id+"F32.opPattern","COPY",BODY,{"derivedFrom":makeQuery(id+"F31.opPattern","COPY",BODY,{"derivedFrom":makeQuery(id+"F30.opPattern","COPY",BODY,{"derivedFrom":makeQuery(id+"F29.opPattern","COPY",BODY,{"derivedFrom":makeQuery(id+"F28.opPattern","COPY",BODY,{"derivedFrom":makeQuery(id+"F27.opPattern","COPY",BODY,{"derivedFrom":makeQuery(id+"F26.opPattern","COPY",BODY,{"derivedFrom":makeQuery(id+"F25.opPattern","COPY",BODY,{"derivedFrom":makeQuery(id+"F24.opPattern","COPY",BODY,{"derivedFrom":makeQuery(id+"F23.opPattern","COPY",BODY,{"derivedFrom":makeQuery(id+"F22.opPattern","COPY",BODY,{"derivedFrom":makeQuery(id+"F21.opPattern","COPY",BODY,{"derivedFrom":makeQuery(id+"F20.opPattern","COPY",BODY,{"derivedFrom":makeQuery(id+"F19.opPattern","COPY",BODY,{"derivedFrom":makeQuery(id+"F18.opPattern","COPY",BODY,{"derivedFrom":makeQuery(id+"F1.opExtrude","SWEPT_BODY",BODY,{"disambiguationData":[OSD([sQuery(id+"F0.wireOp",EDGE,"E0")])]}),"instanceName":"1"}),"instanceName":"1"}),"instanceName":"1"}),"instanceName":"1"}),"instanceName":"1"}),"instanceName":"1"}),"instanceName":"1"}),"instanceName":"1"}),"instanceName":"1"}),"instanceName":"1"}),"instanceName":"1"}),"instanceName":"1"}),"instanceName":"1"}),"instanceName":"1"}),"instanceName":"1"}),"instanceName":"1"}),"instanceName":"1"}),"instanceName":"1"}),"instanceName":"1"}),"instanceName":"1"}),"instanceName":"1"}),"instanceName":"1"}),"instanceName":"1"}),"instanceName":"1"}),"instanceName":"1"});
            transform(context, id + "F53", {"entities" : qUnion([Q0]), "transformType" : TransformType.TRANSLATION_3D, "dx" : 0 * mm, "dy" : -3500 * mm, "dz" : 0 * mm, "makeCopy" : true});
        }
        {
            var Q0;
            Q0=makeQuery(id+"F53.opPattern","COPY",BODY,{"derivedFrom":makeQuery(id+"F52.opPattern","COPY",BODY,{"derivedFrom":makeQuery(id+"F51.opPattern","COPY",BODY,{"derivedFrom":makeQuery(id+"F50.opPattern","COPY",BODY,{"derivedFrom":makeQuery(id+"F41.opPattern","COPY",BODY,{"derivedFrom":makeQuery(id+"F38.opPattern","COPY",BODY,{"derivedFrom":makeQuery(id+"F37.opPattern","COPY",BODY,{"derivedFrom":makeQuery(id+"F36.opPattern","COPY",BODY,{"derivedFrom":makeQuery(id+"F35.opPattern","COPY",BODY,{"derivedFrom":makeQuery(id+"F34.opPattern","COPY",BODY,{"derivedFrom":makeQuery(id+"F33.opPattern","COPY",BODY,{"derivedFrom":makeQuery(id+"F32.opPattern","COPY",BODY,{"derivedFrom":makeQuery(id+"F31.opPattern","COPY",BODY,{"derivedFrom":makeQuery(id+"F30.opPattern","COPY",BODY,{"derivedFrom":makeQuery(id+"F29.opPattern","COPY",BODY,{"derivedFrom":makeQuery(id+"F28.opPattern","COPY",BODY,{"derivedFrom":makeQuery(id+"F27.opPattern","COPY",BODY,{"derivedFrom":makeQuery(id+"F26.opPattern","COPY",BODY,{"derivedFrom":makeQuery(id+"F25.opPattern","COPY",BODY,{"derivedFrom":makeQuery(id+"F24.opPattern","COPY",BODY,{"derivedFrom":makeQuery(id+"F23.opPattern","COPY",BODY,{"derivedFrom":makeQuery(id+"F22.opPattern","COPY",BODY,{"derivedFrom":makeQuery(id+"F21.opPattern","COPY",BODY,{"derivedFrom":makeQuery(id+"F20.opPattern","COPY",BODY,{"derivedFrom":makeQuery(id+"F19.opPattern","COPY",BODY,{"derivedFrom":makeQuery(id+"F18.opPattern","COPY",BODY,{"derivedFrom":makeQuery(id+"F1.opExtrude","SWEPT_BODY",BODY,{"disambiguationData":[OSD([sQuery(id+"F0.wireOp",EDGE,"E0")])]}),"instanceName":"1"}),"instanceName":"1"}),"instanceName":"1"}),"instanceName":"1"}),"instanceName":"1"}),"instanceName":"1"}),"instanceName":"1"}),"instanceName":"1"}),"instanceName":"1"}),"instanceName":"1"}),"instanceName":"1"}),"instanceName":"1"}),"instanceName":"1"}),"instanceName":"1"}),"instanceName":"1"}),"instanceName":"1"}),"instanceName":"1"}),"instanceName":"1"}),"instanceName":"1"}),"instanceName":"1"}),"instanceName":"1"}),"instanceName":"1"}),"instanceName":"1"}),"instanceName":"1"}),"instanceName":"1"}),"instanceName":"1"});
            transform(context, id + "F54", {"entities" : qUnion([Q0]), "transformType" : TransformType.TRANSLATION_3D, "dx" : 0 * mm, "dy" : -3500 * mm, "dz" : 0 * mm, "makeCopy" : true});
        }
        {
            var Q0;
            Q0=makeQuery(id+"F54.opPattern","COPY",BODY,{"derivedFrom":makeQuery(id+"F53.opPattern","COPY",BODY,{"derivedFrom":makeQuery(id+"F52.opPattern","COPY",BODY,{"derivedFrom":makeQuery(id+"F51.opPattern","COPY",BODY,{"derivedFrom":makeQuery(id+"F50.opPattern","COPY",BODY,{"derivedFrom":makeQuery(id+"F41.opPattern","COPY",BODY,{"derivedFrom":makeQuery(id+"F38.opPattern","COPY",BODY,{"derivedFrom":makeQuery(id+"F37.opPattern","COPY",BODY,{"derivedFrom":makeQuery(id+"F36.opPattern","COPY",BODY,{"derivedFrom":makeQuery(id+"F35.opPattern","COPY",BODY,{"derivedFrom":makeQuery(id+"F34.opPattern","COPY",BODY,{"derivedFrom":makeQuery(id+"F33.opPattern","COPY",BODY,{"derivedFrom":makeQuery(id+"F32.opPattern","COPY",BODY,{"derivedFrom":makeQuery(id+"F31.opPattern","COPY",BODY,{"derivedFrom":makeQuery(id+"F30.opPattern","COPY",BODY,{"derivedFrom":makeQuery(id+"F29.opPattern","COPY",BODY,{"derivedFrom":makeQuery(id+"F28.opPattern","COPY",BODY,{"derivedFrom":makeQuery(id+"F27.opPattern","COPY",BODY,{"derivedFrom":makeQuery(id+"F26.opPattern","COPY",BODY,{"derivedFrom":makeQuery(id+"F25.opPattern","COPY",BODY,{"derivedFrom":makeQuery(id+"F24.opPattern","COPY",BODY,{"derivedFrom":makeQuery(id+"F23.opPattern","COPY",BODY,{"derivedFrom":makeQuery(id+"F22.opPattern","COPY",BODY,{"derivedFrom":makeQuery(id+"F21.opPattern","COPY",BODY,{"derivedFrom":makeQuery(id+"F20.opPattern","COPY",BODY,{"derivedFrom":makeQuery(id+"F19.opPattern","COPY",BODY,{"derivedFrom":makeQuery(id+"F18.opPattern","COPY",BODY,{"derivedFrom":makeQuery(id+"F1.opExtrude","SWEPT_BODY",BODY,{"disambiguationData":[OSD([sQuery(id+"F0.wireOp",EDGE,"E0")])]}),"instanceName":"1"}),"instanceName":"1"}),"instanceName":"1"}),"instanceName":"1"}),"instanceName":"1"}),"instanceName":"1"}),"instanceName":"1"}),"instanceName":"1"}),"instanceName":"1"}),"instanceName":"1"}),"instanceName":"1"}),"instanceName":"1"}),"instanceName":"1"}),"instanceName":"1"}),"instanceName":"1"}),"instanceName":"1"}),"instanceName":"1"}),"instanceName":"1"}),"instanceName":"1"}),"instanceName":"1"}),"instanceName":"1"}),"instanceName":"1"}),"instanceName":"1"}),"instanceName":"1"}),"instanceName":"1"}),"instanceName":"1"}),"instanceName":"1"});
            var Q1;
            Q1=makeQuery(id+"F50.opPattern","COPY",BODY,{"derivedFrom":makeQuery(id+"F41.opPattern","COPY",BODY,{"derivedFrom":makeQuery(id+"F38.opPattern","COPY",BODY,{"derivedFrom":makeQuery(id+"F37.opPattern","COPY",BODY,{"derivedFrom":makeQuery(id+"F36.opPattern","COPY",BODY,{"derivedFrom":makeQuery(id+"F35.opPattern","COPY",BODY,{"derivedFrom":makeQuery(id+"F34.opPattern","COPY",BODY,{"derivedFrom":makeQuery(id+"F33.opPattern","COPY",BODY,{"derivedFrom":makeQuery(id+"F32.opPattern","COPY",BODY,{"derivedFrom":makeQuery(id+"F31.opPattern","COPY",BODY,{"derivedFrom":makeQuery(id+"F30.opPattern","COPY",BODY,{"derivedFrom":makeQuery(id+"F29.opPattern","COPY",BODY,{"derivedFrom":makeQuery(id+"F28.opPattern","COPY",BODY,{"derivedFrom":makeQuery(id+"F27.opPattern","COPY",BODY,{"derivedFrom":makeQuery(id+"F26.opPattern","COPY",BODY,{"derivedFrom":makeQuery(id+"F25.opPattern","COPY",BODY,{"derivedFrom":makeQuery(id+"F24.opPattern","COPY",BODY,{"derivedFrom":makeQuery(id+"F23.opPattern","COPY",BODY,{"derivedFrom":makeQuery(id+"F22.opPattern","COPY",BODY,{"derivedFrom":makeQuery(id+"F21.opPattern","COPY",BODY,{"derivedFrom":makeQuery(id+"F20.opPattern","COPY",BODY,{"derivedFrom":makeQuery(id+"F19.opPattern","COPY",BODY,{"derivedFrom":makeQuery(id+"F18.opPattern","COPY",BODY,{"derivedFrom":makeQuery(id+"F1.opExtrude","SWEPT_BODY",BODY,{"disambiguationData":[OSD([sQuery(id+"F0.wireOp",EDGE,"E0")])]}),"instanceName":"1"}),"instanceName":"1"}),"instanceName":"1"}),"instanceName":"1"}),"instanceName":"1"}),"instanceName":"1"}),"instanceName":"1"}),"instanceName":"1"}),"instanceName":"1"}),"instanceName":"1"}),"instanceName":"1"}),"instanceName":"1"}),"instanceName":"1"}),"instanceName":"1"}),"instanceName":"1"}),"instanceName":"1"}),"instanceName":"1"}),"instanceName":"1"}),"instanceName":"1"}),"instanceName":"1"}),"instanceName":"1"}),"instanceName":"1"}),"instanceName":"1"});
            var Q2;
            Q2=makeQuery(id+"F51.opPattern","COPY",BODY,{"derivedFrom":makeQuery(id+"F50.opPattern","COPY",BODY,{"derivedFrom":makeQuery(id+"F41.opPattern","COPY",BODY,{"derivedFrom":makeQuery(id+"F38.opPattern","COPY",BODY,{"derivedFrom":makeQuery(id+"F37.opPattern","COPY",BODY,{"derivedFrom":makeQuery(id+"F36.opPattern","COPY",BODY,{"derivedFrom":makeQuery(id+"F35.opPattern","COPY",BODY,{"derivedFrom":makeQuery(id+"F34.opPattern","COPY",BODY,{"derivedFrom":makeQuery(id+"F33.opPattern","COPY",BODY,{"derivedFrom":makeQuery(id+"F32.opPattern","COPY",BODY,{"derivedFrom":makeQuery(id+"F31.opPattern","COPY",BODY,{"derivedFrom":makeQuery(id+"F30.opPattern","COPY",BODY,{"derivedFrom":makeQuery(id+"F29.opPattern","COPY",BODY,{"derivedFrom":makeQuery(id+"F28.opPattern","COPY",BODY,{"derivedFrom":makeQuery(id+"F27.opPattern","COPY",BODY,{"derivedFrom":makeQuery(id+"F26.opPattern","COPY",BODY,{"derivedFrom":makeQuery(id+"F25.opPattern","COPY",BODY,{"derivedFrom":makeQuery(id+"F24.opPattern","COPY",BODY,{"derivedFrom":makeQuery(id+"F23.opPattern","COPY",BODY,{"derivedFrom":makeQuery(id+"F22.opPattern","COPY",BODY,{"derivedFrom":makeQuery(id+"F21.opPattern","COPY",BODY,{"derivedFrom":makeQuery(id+"F20.opPattern","COPY",BODY,{"derivedFrom":makeQuery(id+"F19.opPattern","COPY",BODY,{"derivedFrom":makeQuery(id+"F18.opPattern","COPY",BODY,{"derivedFrom":makeQuery(id+"F1.opExtrude","SWEPT_BODY",BODY,{"disambiguationData":[OSD([sQuery(id+"F0.wireOp",EDGE,"E0")])]}),"instanceName":"1"}),"instanceName":"1"}),"instanceName":"1"}),"instanceName":"1"}),"instanceName":"1"}),"instanceName":"1"}),"instanceName":"1"}),"instanceName":"1"}),"instanceName":"1"}),"instanceName":"1"}),"instanceName":"1"}),"instanceName":"1"}),"instanceName":"1"}),"instanceName":"1"}),"instanceName":"1"}),"instanceName":"1"}),"instanceName":"1"}),"instanceName":"1"}),"instanceName":"1"}),"instanceName":"1"}),"instanceName":"1"}),"instanceName":"1"}),"instanceName":"1"}),"instanceName":"1"});
            var Q3;
            Q3=makeQuery(id+"F52.opPattern","COPY",BODY,{"derivedFrom":makeQuery(id+"F51.opPattern","COPY",BODY,{"derivedFrom":makeQuery(id+"F50.opPattern","COPY",BODY,{"derivedFrom":makeQuery(id+"F41.opPattern","COPY",BODY,{"derivedFrom":makeQuery(id+"F38.opPattern","COPY",BODY,{"derivedFrom":makeQuery(id+"F37.opPattern","COPY",BODY,{"derivedFrom":makeQuery(id+"F36.opPattern","COPY",BODY,{"derivedFrom":makeQuery(id+"F35.opPattern","COPY",BODY,{"derivedFrom":makeQuery(id+"F34.opPattern","COPY",BODY,{"derivedFrom":makeQuery(id+"F33.opPattern","COPY",BODY,{"derivedFrom":makeQuery(id+"F32.opPattern","COPY",BODY,{"derivedFrom":makeQuery(id+"F31.opPattern","COPY",BODY,{"derivedFrom":makeQuery(id+"F30.opPattern","COPY",BODY,{"derivedFrom":makeQuery(id+"F29.opPattern","COPY",BODY,{"derivedFrom":makeQuery(id+"F28.opPattern","COPY",BODY,{"derivedFrom":makeQuery(id+"F27.opPattern","COPY",BODY,{"derivedFrom":makeQuery(id+"F26.opPattern","COPY",BODY,{"derivedFrom":makeQuery(id+"F25.opPattern","COPY",BODY,{"derivedFrom":makeQuery(id+"F24.opPattern","COPY",BODY,{"derivedFrom":makeQuery(id+"F23.opPattern","COPY",BODY,{"derivedFrom":makeQuery(id+"F22.opPattern","COPY",BODY,{"derivedFrom":makeQuery(id+"F21.opPattern","COPY",BODY,{"derivedFrom":makeQuery(id+"F20.opPattern","COPY",BODY,{"derivedFrom":makeQuery(id+"F19.opPattern","COPY",BODY,{"derivedFrom":makeQuery(id+"F18.opPattern","COPY",BODY,{"derivedFrom":makeQuery(id+"F1.opExtrude","SWEPT_BODY",BODY,{"disambiguationData":[OSD([sQuery(id+"F0.wireOp",EDGE,"E0")])]}),"instanceName":"1"}),"instanceName":"1"}),"instanceName":"1"}),"instanceName":"1"}),"instanceName":"1"}),"instanceName":"1"}),"instanceName":"1"}),"instanceName":"1"}),"instanceName":"1"}),"instanceName":"1"}),"instanceName":"1"}),"instanceName":"1"}),"instanceName":"1"}),"instanceName":"1"}),"instanceName":"1"}),"instanceName":"1"}),"instanceName":"1"}),"instanceName":"1"}),"instanceName":"1"}),"instanceName":"1"}),"instanceName":"1"}),"instanceName":"1"}),"instanceName":"1"}),"instanceName":"1"}),"instanceName":"1"});
            var Q4;
            Q4=makeQuery(id+"F53.opPattern","COPY",BODY,{"derivedFrom":makeQuery(id+"F52.opPattern","COPY",BODY,{"derivedFrom":makeQuery(id+"F51.opPattern","COPY",BODY,{"derivedFrom":makeQuery(id+"F50.opPattern","COPY",BODY,{"derivedFrom":makeQuery(id+"F41.opPattern","COPY",BODY,{"derivedFrom":makeQuery(id+"F38.opPattern","COPY",BODY,{"derivedFrom":makeQuery(id+"F37.opPattern","COPY",BODY,{"derivedFrom":makeQuery(id+"F36.opPattern","COPY",BODY,{"derivedFrom":makeQuery(id+"F35.opPattern","COPY",BODY,{"derivedFrom":makeQuery(id+"F34.opPattern","COPY",BODY,{"derivedFrom":makeQuery(id+"F33.opPattern","COPY",BODY,{"derivedFrom":makeQuery(id+"F32.opPattern","COPY",BODY,{"derivedFrom":makeQuery(id+"F31.opPattern","COPY",BODY,{"derivedFrom":makeQuery(id+"F30.opPattern","COPY",BODY,{"derivedFrom":makeQuery(id+"F29.opPattern","COPY",BODY,{"derivedFrom":makeQuery(id+"F28.opPattern","COPY",BODY,{"derivedFrom":makeQuery(id+"F27.opPattern","COPY",BODY,{"derivedFrom":makeQuery(id+"F26.opPattern","COPY",BODY,{"derivedFrom":makeQuery(id+"F25.opPattern","COPY",BODY,{"derivedFrom":makeQuery(id+"F24.opPattern","COPY",BODY,{"derivedFrom":makeQuery(id+"F23.opPattern","COPY",BODY,{"derivedFrom":makeQuery(id+"F22.opPattern","COPY",BODY,{"derivedFrom":makeQuery(id+"F21.opPattern","COPY",BODY,{"derivedFrom":makeQuery(id+"F20.opPattern","COPY",BODY,{"derivedFrom":makeQuery(id+"F19.opPattern","COPY",BODY,{"derivedFrom":makeQuery(id+"F18.opPattern","COPY",BODY,{"derivedFrom":makeQuery(id+"F1.opExtrude","SWEPT_BODY",BODY,{"disambiguationData":[OSD([sQuery(id+"F0.wireOp",EDGE,"E0")])]}),"instanceName":"1"}),"instanceName":"1"}),"instanceName":"1"}),"instanceName":"1"}),"instanceName":"1"}),"instanceName":"1"}),"instanceName":"1"}),"instanceName":"1"}),"instanceName":"1"}),"instanceName":"1"}),"instanceName":"1"}),"instanceName":"1"}),"instanceName":"1"}),"instanceName":"1"}),"instanceName":"1"}),"instanceName":"1"}),"instanceName":"1"}),"instanceName":"1"}),"instanceName":"1"}),"instanceName":"1"}),"instanceName":"1"}),"instanceName":"1"}),"instanceName":"1"}),"instanceName":"1"}),"instanceName":"1"}),"instanceName":"1"});
            deleteBodies(context, id + "F55", {"entities" : qUnion([Q0, Q1, Q2, Q3, Q4])});
        }
        {
            var Q0;
            Q0=makeQuery(id+"F41.opPattern","COPY",BODY,{"derivedFrom":makeQuery(id+"F38.opPattern","COPY",BODY,{"derivedFrom":makeQuery(id+"F37.opPattern","COPY",BODY,{"derivedFrom":makeQuery(id+"F36.opPattern","COPY",BODY,{"derivedFrom":makeQuery(id+"F35.opPattern","COPY",BODY,{"derivedFrom":makeQuery(id+"F34.opPattern","COPY",BODY,{"derivedFrom":makeQuery(id+"F33.opPattern","COPY",BODY,{"derivedFrom":makeQuery(id+"F32.opPattern","COPY",BODY,{"derivedFrom":makeQuery(id+"F31.opPattern","COPY",BODY,{"derivedFrom":makeQuery(id+"F30.opPattern","COPY",BODY,{"derivedFrom":makeQuery(id+"F29.opPattern","COPY",BODY,{"derivedFrom":makeQuery(id+"F28.opPattern","COPY",BODY,{"derivedFrom":makeQuery(id+"F27.opPattern","COPY",BODY,{"derivedFrom":makeQuery(id+"F26.opPattern","COPY",BODY,{"derivedFrom":makeQuery(id+"F25.opPattern","COPY",BODY,{"derivedFrom":makeQuery(id+"F24.opPattern","COPY",BODY,{"derivedFrom":makeQuery(id+"F23.opPattern","COPY",BODY,{"derivedFrom":makeQuery(id+"F22.opPattern","COPY",BODY,{"derivedFrom":makeQuery(id+"F21.opPattern","COPY",BODY,{"derivedFrom":makeQuery(id+"F20.opPattern","COPY",BODY,{"derivedFrom":makeQuery(id+"F19.opPattern","COPY",BODY,{"derivedFrom":makeQuery(id+"F18.opPattern","COPY",BODY,{"derivedFrom":makeQuery(id+"F1.opExtrude","SWEPT_BODY",BODY,{"disambiguationData":[OSD([sQuery(id+"F0.wireOp",EDGE,"E0")])]}),"instanceName":"1"}),"instanceName":"1"}),"instanceName":"1"}),"instanceName":"1"}),"instanceName":"1"}),"instanceName":"1"}),"instanceName":"1"}),"instanceName":"1"}),"instanceName":"1"}),"instanceName":"1"}),"instanceName":"1"}),"instanceName":"1"}),"instanceName":"1"}),"instanceName":"1"}),"instanceName":"1"}),"instanceName":"1"}),"instanceName":"1"}),"instanceName":"1"}),"instanceName":"1"}),"instanceName":"1"}),"instanceName":"1"}),"instanceName":"1"});
            transform(context, id + "F56", {"entities" : qUnion([Q0]), "transformType" : TransformType.TRANSLATION_3D, "dx" : 0 * mm, "dy" : -2897 * mm, "dz" : 0 * mm, "makeCopy" : true});
        }
        {
            var Q0;
            Q0=makeQuery(id+"F56.opPattern","COPY",BODY,{"derivedFrom":makeQuery(id+"F41.opPattern","COPY",BODY,{"derivedFrom":makeQuery(id+"F38.opPattern","COPY",BODY,{"derivedFrom":makeQuery(id+"F37.opPattern","COPY",BODY,{"derivedFrom":makeQuery(id+"F36.opPattern","COPY",BODY,{"derivedFrom":makeQuery(id+"F35.opPattern","COPY",BODY,{"derivedFrom":makeQuery(id+"F34.opPattern","COPY",BODY,{"derivedFrom":makeQuery(id+"F33.opPattern","COPY",BODY,{"derivedFrom":makeQuery(id+"F32.opPattern","COPY",BODY,{"derivedFrom":makeQuery(id+"F31.opPattern","COPY",BODY,{"derivedFrom":makeQuery(id+"F30.opPattern","COPY",BODY,{"derivedFrom":makeQuery(id+"F29.opPattern","COPY",BODY,{"derivedFrom":makeQuery(id+"F28.opPattern","COPY",BODY,{"derivedFrom":makeQuery(id+"F27.opPattern","COPY",BODY,{"derivedFrom":makeQuery(id+"F26.opPattern","COPY",BODY,{"derivedFrom":makeQuery(id+"F25.opPattern","COPY",BODY,{"derivedFrom":makeQuery(id+"F24.opPattern","COPY",BODY,{"derivedFrom":makeQuery(id+"F23.opPattern","COPY",BODY,{"derivedFrom":makeQuery(id+"F22.opPattern","COPY",BODY,{"derivedFrom":makeQuery(id+"F21.opPattern","COPY",BODY,{"derivedFrom":makeQuery(id+"F20.opPattern","COPY",BODY,{"derivedFrom":makeQuery(id+"F19.opPattern","COPY",BODY,{"derivedFrom":makeQuery(id+"F18.opPattern","COPY",BODY,{"derivedFrom":makeQuery(id+"F1.opExtrude","SWEPT_BODY",BODY,{"disambiguationData":[OSD([sQuery(id+"F0.wireOp",EDGE,"E0")])]}),"instanceName":"1"}),"instanceName":"1"}),"instanceName":"1"}),"instanceName":"1"}),"instanceName":"1"}),"instanceName":"1"}),"instanceName":"1"}),"instanceName":"1"}),"instanceName":"1"}),"instanceName":"1"}),"instanceName":"1"}),"instanceName":"1"}),"instanceName":"1"}),"instanceName":"1"}),"instanceName":"1"}),"instanceName":"1"}),"instanceName":"1"}),"instanceName":"1"}),"instanceName":"1"}),"instanceName":"1"}),"instanceName":"1"}),"instanceName":"1"}),"instanceName":"1"});
            transform(context, id + "F57", {"entities" : qUnion([Q0]), "transformType" : TransformType.TRANSLATION_3D, "dx" : 0 * mm, "dy" : -2897 * mm, "dz" : 0 * mm, "makeCopy" : true});
        }
        {
            var Q0;
            Q0=makeQuery(id+"F57.opPattern","COPY",BODY,{"derivedFrom":makeQuery(id+"F56.opPattern","COPY",BODY,{"derivedFrom":makeQuery(id+"F41.opPattern","COPY",BODY,{"derivedFrom":makeQuery(id+"F38.opPattern","COPY",BODY,{"derivedFrom":makeQuery(id+"F37.opPattern","COPY",BODY,{"derivedFrom":makeQuery(id+"F36.opPattern","COPY",BODY,{"derivedFrom":makeQuery(id+"F35.opPattern","COPY",BODY,{"derivedFrom":makeQuery(id+"F34.opPattern","COPY",BODY,{"derivedFrom":makeQuery(id+"F33.opPattern","COPY",BODY,{"derivedFrom":makeQuery(id+"F32.opPattern","COPY",BODY,{"derivedFrom":makeQuery(id+"F31.opPattern","COPY",BODY,{"derivedFrom":makeQuery(id+"F30.opPattern","COPY",BODY,{"derivedFrom":makeQuery(id+"F29.opPattern","COPY",BODY,{"derivedFrom":makeQuery(id+"F28.opPattern","COPY",BODY,{"derivedFrom":makeQuery(id+"F27.opPattern","COPY",BODY,{"derivedFrom":makeQuery(id+"F26.opPattern","COPY",BODY,{"derivedFrom":makeQuery(id+"F25.opPattern","COPY",BODY,{"derivedFrom":makeQuery(id+"F24.opPattern","COPY",BODY,{"derivedFrom":makeQuery(id+"F23.opPattern","COPY",BODY,{"derivedFrom":makeQuery(id+"F22.opPattern","COPY",BODY,{"derivedFrom":makeQuery(id+"F21.opPattern","COPY",BODY,{"derivedFrom":makeQuery(id+"F20.opPattern","COPY",BODY,{"derivedFrom":makeQuery(id+"F19.opPattern","COPY",BODY,{"derivedFrom":makeQuery(id+"F18.opPattern","COPY",BODY,{"derivedFrom":makeQuery(id+"F1.opExtrude","SWEPT_BODY",BODY,{"disambiguationData":[OSD([sQuery(id+"F0.wireOp",EDGE,"E0")])]}),"instanceName":"1"}),"instanceName":"1"}),"instanceName":"1"}),"instanceName":"1"}),"instanceName":"1"}),"instanceName":"1"}),"instanceName":"1"}),"instanceName":"1"}),"instanceName":"1"}),"instanceName":"1"}),"instanceName":"1"}),"instanceName":"1"}),"instanceName":"1"}),"instanceName":"1"}),"instanceName":"1"}),"instanceName":"1"}),"instanceName":"1"}),"instanceName":"1"}),"instanceName":"1"}),"instanceName":"1"}),"instanceName":"1"}),"instanceName":"1"}),"instanceName":"1"}),"instanceName":"1"});
            transform(context, id + "F58", {"entities" : qUnion([Q0]), "transformType" : TransformType.TRANSLATION_3D, "dx" : 0 * mm, "dy" : -2897 * mm, "dz" : 0 * mm, "makeCopy" : true});
        }
        {
            var Q0;
            Q0=makeQuery(id+"F58.opPattern","COPY",BODY,{"derivedFrom":makeQuery(id+"F57.opPattern","COPY",BODY,{"derivedFrom":makeQuery(id+"F56.opPattern","COPY",BODY,{"derivedFrom":makeQuery(id+"F41.opPattern","COPY",BODY,{"derivedFrom":makeQuery(id+"F38.opPattern","COPY",BODY,{"derivedFrom":makeQuery(id+"F37.opPattern","COPY",BODY,{"derivedFrom":makeQuery(id+"F36.opPattern","COPY",BODY,{"derivedFrom":makeQuery(id+"F35.opPattern","COPY",BODY,{"derivedFrom":makeQuery(id+"F34.opPattern","COPY",BODY,{"derivedFrom":makeQuery(id+"F33.opPattern","COPY",BODY,{"derivedFrom":makeQuery(id+"F32.opPattern","COPY",BODY,{"derivedFrom":makeQuery(id+"F31.opPattern","COPY",BODY,{"derivedFrom":makeQuery(id+"F30.opPattern","COPY",BODY,{"derivedFrom":makeQuery(id+"F29.opPattern","COPY",BODY,{"derivedFrom":makeQuery(id+"F28.opPattern","COPY",BODY,{"derivedFrom":makeQuery(id+"F27.opPattern","COPY",BODY,{"derivedFrom":makeQuery(id+"F26.opPattern","COPY",BODY,{"derivedFrom":makeQuery(id+"F25.opPattern","COPY",BODY,{"derivedFrom":makeQuery(id+"F24.opPattern","COPY",BODY,{"derivedFrom":makeQuery(id+"F23.opPattern","COPY",BODY,{"derivedFrom":makeQuery(id+"F22.opPattern","COPY",BODY,{"derivedFrom":makeQuery(id+"F21.opPattern","COPY",BODY,{"derivedFrom":makeQuery(id+"F20.opPattern","COPY",BODY,{"derivedFrom":makeQuery(id+"F19.opPattern","COPY",BODY,{"derivedFrom":makeQuery(id+"F18.opPattern","COPY",BODY,{"derivedFrom":makeQuery(id+"F1.opExtrude","SWEPT_BODY",BODY,{"disambiguationData":[OSD([sQuery(id+"F0.wireOp",EDGE,"E0")])]}),"instanceName":"1"}),"instanceName":"1"}),"instanceName":"1"}),"instanceName":"1"}),"instanceName":"1"}),"instanceName":"1"}),"instanceName":"1"}),"instanceName":"1"}),"instanceName":"1"}),"instanceName":"1"}),"instanceName":"1"}),"instanceName":"1"}),"instanceName":"1"}),"instanceName":"1"}),"instanceName":"1"}),"instanceName":"1"}),"instanceName":"1"}),"instanceName":"1"}),"instanceName":"1"}),"instanceName":"1"}),"instanceName":"1"}),"instanceName":"1"}),"instanceName":"1"}),"instanceName":"1"}),"instanceName":"1"});
            transform(context, id + "F59", {"entities" : qUnion([Q0]), "transformType" : TransformType.TRANSLATION_3D, "dx" : 0 * mm, "dy" : -2897 * mm, "dz" : 0 * mm, "makeCopy" : true});
        }
        {
            var Q0;
            Q0=makeQuery(id+"F59.opPattern","COPY",BODY,{"derivedFrom":makeQuery(id+"F58.opPattern","COPY",BODY,{"derivedFrom":makeQuery(id+"F57.opPattern","COPY",BODY,{"derivedFrom":makeQuery(id+"F56.opPattern","COPY",BODY,{"derivedFrom":makeQuery(id+"F41.opPattern","COPY",BODY,{"derivedFrom":makeQuery(id+"F38.opPattern","COPY",BODY,{"derivedFrom":makeQuery(id+"F37.opPattern","COPY",BODY,{"derivedFrom":makeQuery(id+"F36.opPattern","COPY",BODY,{"derivedFrom":makeQuery(id+"F35.opPattern","COPY",BODY,{"derivedFrom":makeQuery(id+"F34.opPattern","COPY",BODY,{"derivedFrom":makeQuery(id+"F33.opPattern","COPY",BODY,{"derivedFrom":makeQuery(id+"F32.opPattern","COPY",BODY,{"derivedFrom":makeQuery(id+"F31.opPattern","COPY",BODY,{"derivedFrom":makeQuery(id+"F30.opPattern","COPY",BODY,{"derivedFrom":makeQuery(id+"F29.opPattern","COPY",BODY,{"derivedFrom":makeQuery(id+"F28.opPattern","COPY",BODY,{"derivedFrom":makeQuery(id+"F27.opPattern","COPY",BODY,{"derivedFrom":makeQuery(id+"F26.opPattern","COPY",BODY,{"derivedFrom":makeQuery(id+"F25.opPattern","COPY",BODY,{"derivedFrom":makeQuery(id+"F24.opPattern","COPY",BODY,{"derivedFrom":makeQuery(id+"F23.opPattern","COPY",BODY,{"derivedFrom":makeQuery(id+"F22.opPattern","COPY",BODY,{"derivedFrom":makeQuery(id+"F21.opPattern","COPY",BODY,{"derivedFrom":makeQuery(id+"F20.opPattern","COPY",BODY,{"derivedFrom":makeQuery(id+"F19.opPattern","COPY",BODY,{"derivedFrom":makeQuery(id+"F18.opPattern","COPY",BODY,{"derivedFrom":makeQuery(id+"F1.opExtrude","SWEPT_BODY",BODY,{"disambiguationData":[OSD([sQuery(id+"F0.wireOp",EDGE,"E0")])]}),"instanceName":"1"}),"instanceName":"1"}),"instanceName":"1"}),"instanceName":"1"}),"instanceName":"1"}),"instanceName":"1"}),"instanceName":"1"}),"instanceName":"1"}),"instanceName":"1"}),"instanceName":"1"}),"instanceName":"1"}),"instanceName":"1"}),"instanceName":"1"}),"instanceName":"1"}),"instanceName":"1"}),"instanceName":"1"}),"instanceName":"1"}),"instanceName":"1"}),"instanceName":"1"}),"instanceName":"1"}),"instanceName":"1"}),"instanceName":"1"}),"instanceName":"1"}),"instanceName":"1"}),"instanceName":"1"}),"instanceName":"1"});
            deleteBodies(context, id + "F60", {"entities" : qUnion([Q0])});
        }
        {
            var Q0;
            Q0=makeQuery(id+"F58.opPattern","COPY",BODY,{"derivedFrom":makeQuery(id+"F57.opPattern","COPY",BODY,{"derivedFrom":makeQuery(id+"F56.opPattern","COPY",BODY,{"derivedFrom":makeQuery(id+"F41.opPattern","COPY",BODY,{"derivedFrom":makeQuery(id+"F38.opPattern","COPY",BODY,{"derivedFrom":makeQuery(id+"F37.opPattern","COPY",BODY,{"derivedFrom":makeQuery(id+"F36.opPattern","COPY",BODY,{"derivedFrom":makeQuery(id+"F35.opPattern","COPY",BODY,{"derivedFrom":makeQuery(id+"F34.opPattern","COPY",BODY,{"derivedFrom":makeQuery(id+"F33.opPattern","COPY",BODY,{"derivedFrom":makeQuery(id+"F32.opPattern","COPY",BODY,{"derivedFrom":makeQuery(id+"F31.opPattern","COPY",BODY,{"derivedFrom":makeQuery(id+"F30.opPattern","COPY",BODY,{"derivedFrom":makeQuery(id+"F29.opPattern","COPY",BODY,{"derivedFrom":makeQuery(id+"F28.opPattern","COPY",BODY,{"derivedFrom":makeQuery(id+"F27.opPattern","COPY",BODY,{"derivedFrom":makeQuery(id+"F26.opPattern","COPY",BODY,{"derivedFrom":makeQuery(id+"F25.opPattern","COPY",BODY,{"derivedFrom":makeQuery(id+"F24.opPattern","COPY",BODY,{"derivedFrom":makeQuery(id+"F23.opPattern","COPY",BODY,{"derivedFrom":makeQuery(id+"F22.opPattern","COPY",BODY,{"derivedFrom":makeQuery(id+"F21.opPattern","COPY",BODY,{"derivedFrom":makeQuery(id+"F20.opPattern","COPY",BODY,{"derivedFrom":makeQuery(id+"F19.opPattern","COPY",BODY,{"derivedFrom":makeQuery(id+"F18.opPattern","COPY",BODY,{"derivedFrom":makeQuery(id+"F1.opExtrude","SWEPT_BODY",BODY,{"disambiguationData":[OSD([sQuery(id+"F0.wireOp",EDGE,"E0")])]}),"instanceName":"1"}),"instanceName":"1"}),"instanceName":"1"}),"instanceName":"1"}),"instanceName":"1"}),"instanceName":"1"}),"instanceName":"1"}),"instanceName":"1"}),"instanceName":"1"}),"instanceName":"1"}),"instanceName":"1"}),"instanceName":"1"}),"instanceName":"1"}),"instanceName":"1"}),"instanceName":"1"}),"instanceName":"1"}),"instanceName":"1"}),"instanceName":"1"}),"instanceName":"1"}),"instanceName":"1"}),"instanceName":"1"}),"instanceName":"1"}),"instanceName":"1"}),"instanceName":"1"}),"instanceName":"1"});
            transform(context, id + "F61", {"entities" : qUnion([Q0]), "transformType" : TransformType.TRANSLATION_3D, "dx" : -2600 * mm, "dy" : 0 * mm, "dz" : 0 * mm, "makeCopy" : true});
        }
        {
            var Q0;
            Q0=makeQuery(id+"F61.opPattern","COPY",BODY,{"derivedFrom":makeQuery(id+"F58.opPattern","COPY",BODY,{"derivedFrom":makeQuery(id+"F57.opPattern","COPY",BODY,{"derivedFrom":makeQuery(id+"F56.opPattern","COPY",BODY,{"derivedFrom":makeQuery(id+"F41.opPattern","COPY",BODY,{"derivedFrom":makeQuery(id+"F38.opPattern","COPY",BODY,{"derivedFrom":makeQuery(id+"F37.opPattern","COPY",BODY,{"derivedFrom":makeQuery(id+"F36.opPattern","COPY",BODY,{"derivedFrom":makeQuery(id+"F35.opPattern","COPY",BODY,{"derivedFrom":makeQuery(id+"F34.opPattern","COPY",BODY,{"derivedFrom":makeQuery(id+"F33.opPattern","COPY",BODY,{"derivedFrom":makeQuery(id+"F32.opPattern","COPY",BODY,{"derivedFrom":makeQuery(id+"F31.opPattern","COPY",BODY,{"derivedFrom":makeQuery(id+"F30.opPattern","COPY",BODY,{"derivedFrom":makeQuery(id+"F29.opPattern","COPY",BODY,{"derivedFrom":makeQuery(id+"F28.opPattern","COPY",BODY,{"derivedFrom":makeQuery(id+"F27.opPattern","COPY",BODY,{"derivedFrom":makeQuery(id+"F26.opPattern","COPY",BODY,{"derivedFrom":makeQuery(id+"F25.opPattern","COPY",BODY,{"derivedFrom":makeQuery(id+"F24.opPattern","COPY",BODY,{"derivedFrom":makeQuery(id+"F23.opPattern","COPY",BODY,{"derivedFrom":makeQuery(id+"F22.opPattern","COPY",BODY,{"derivedFrom":makeQuery(id+"F21.opPattern","COPY",BODY,{"derivedFrom":makeQuery(id+"F20.opPattern","COPY",BODY,{"derivedFrom":makeQuery(id+"F19.opPattern","COPY",BODY,{"derivedFrom":makeQuery(id+"F18.opPattern","COPY",BODY,{"derivedFrom":makeQuery(id+"F1.opExtrude","SWEPT_BODY",BODY,{"disambiguationData":[OSD([sQuery(id+"F0.wireOp",EDGE,"E0")])]}),"instanceName":"1"}),"instanceName":"1"}),"instanceName":"1"}),"instanceName":"1"}),"instanceName":"1"}),"instanceName":"1"}),"instanceName":"1"}),"instanceName":"1"}),"instanceName":"1"}),"instanceName":"1"}),"instanceName":"1"}),"instanceName":"1"}),"instanceName":"1"}),"instanceName":"1"}),"instanceName":"1"}),"instanceName":"1"}),"instanceName":"1"}),"instanceName":"1"}),"instanceName":"1"}),"instanceName":"1"}),"instanceName":"1"}),"instanceName":"1"}),"instanceName":"1"}),"instanceName":"1"}),"instanceName":"1"}),"instanceName":"1"});
            deleteBodies(context, id + "F62", {"entities" : qUnion([Q0])});
        }
        {
            var Q0;
            Q0=makeQuery(id+"F58.opPattern","COPY",BODY,{"derivedFrom":makeQuery(id+"F57.opPattern","COPY",BODY,{"derivedFrom":makeQuery(id+"F56.opPattern","COPY",BODY,{"derivedFrom":makeQuery(id+"F41.opPattern","COPY",BODY,{"derivedFrom":makeQuery(id+"F38.opPattern","COPY",BODY,{"derivedFrom":makeQuery(id+"F37.opPattern","COPY",BODY,{"derivedFrom":makeQuery(id+"F36.opPattern","COPY",BODY,{"derivedFrom":makeQuery(id+"F35.opPattern","COPY",BODY,{"derivedFrom":makeQuery(id+"F34.opPattern","COPY",BODY,{"derivedFrom":makeQuery(id+"F33.opPattern","COPY",BODY,{"derivedFrom":makeQuery(id+"F32.opPattern","COPY",BODY,{"derivedFrom":makeQuery(id+"F31.opPattern","COPY",BODY,{"derivedFrom":makeQuery(id+"F30.opPattern","COPY",BODY,{"derivedFrom":makeQuery(id+"F29.opPattern","COPY",BODY,{"derivedFrom":makeQuery(id+"F28.opPattern","COPY",BODY,{"derivedFrom":makeQuery(id+"F27.opPattern","COPY",BODY,{"derivedFrom":makeQuery(id+"F26.opPattern","COPY",BODY,{"derivedFrom":makeQuery(id+"F25.opPattern","COPY",BODY,{"derivedFrom":makeQuery(id+"F24.opPattern","COPY",BODY,{"derivedFrom":makeQuery(id+"F23.opPattern","COPY",BODY,{"derivedFrom":makeQuery(id+"F22.opPattern","COPY",BODY,{"derivedFrom":makeQuery(id+"F21.opPattern","COPY",BODY,{"derivedFrom":makeQuery(id+"F20.opPattern","COPY",BODY,{"derivedFrom":makeQuery(id+"F19.opPattern","COPY",BODY,{"derivedFrom":makeQuery(id+"F18.opPattern","COPY",BODY,{"derivedFrom":makeQuery(id+"F1.opExtrude","SWEPT_BODY",BODY,{"disambiguationData":[OSD([sQuery(id+"F0.wireOp",EDGE,"E0")])]}),"instanceName":"1"}),"instanceName":"1"}),"instanceName":"1"}),"instanceName":"1"}),"instanceName":"1"}),"instanceName":"1"}),"instanceName":"1"}),"instanceName":"1"}),"instanceName":"1"}),"instanceName":"1"}),"instanceName":"1"}),"instanceName":"1"}),"instanceName":"1"}),"instanceName":"1"}),"instanceName":"1"}),"instanceName":"1"}),"instanceName":"1"}),"instanceName":"1"}),"instanceName":"1"}),"instanceName":"1"}),"instanceName":"1"}),"instanceName":"1"}),"instanceName":"1"}),"instanceName":"1"}),"instanceName":"1"});
            transform(context, id + "F63", {"entities" : qUnion([Q0]), "transformType" : TransformType.TRANSLATION_3D, "dx" : 0 * mm, "dy" : -2600 * mm, "dz" : 0 * mm, "makeCopy" : true});
        }
        {
            var Q0;
            Q0=makeQuery(id+"F63.opPattern","COPY",BODY,{"derivedFrom":makeQuery(id+"F58.opPattern","COPY",BODY,{"derivedFrom":makeQuery(id+"F57.opPattern","COPY",BODY,{"derivedFrom":makeQuery(id+"F56.opPattern","COPY",BODY,{"derivedFrom":makeQuery(id+"F41.opPattern","COPY",BODY,{"derivedFrom":makeQuery(id+"F38.opPattern","COPY",BODY,{"derivedFrom":makeQuery(id+"F37.opPattern","COPY",BODY,{"derivedFrom":makeQuery(id+"F36.opPattern","COPY",BODY,{"derivedFrom":makeQuery(id+"F35.opPattern","COPY",BODY,{"derivedFrom":makeQuery(id+"F34.opPattern","COPY",BODY,{"derivedFrom":makeQuery(id+"F33.opPattern","COPY",BODY,{"derivedFrom":makeQuery(id+"F32.opPattern","COPY",BODY,{"derivedFrom":makeQuery(id+"F31.opPattern","COPY",BODY,{"derivedFrom":makeQuery(id+"F30.opPattern","COPY",BODY,{"derivedFrom":makeQuery(id+"F29.opPattern","COPY",BODY,{"derivedFrom":makeQuery(id+"F28.opPattern","COPY",BODY,{"derivedFrom":makeQuery(id+"F27.opPattern","COPY",BODY,{"derivedFrom":makeQuery(id+"F26.opPattern","COPY",BODY,{"derivedFrom":makeQuery(id+"F25.opPattern","COPY",BODY,{"derivedFrom":makeQuery(id+"F24.opPattern","COPY",BODY,{"derivedFrom":makeQuery(id+"F23.opPattern","COPY",BODY,{"derivedFrom":makeQuery(id+"F22.opPattern","COPY",BODY,{"derivedFrom":makeQuery(id+"F21.opPattern","COPY",BODY,{"derivedFrom":makeQuery(id+"F20.opPattern","COPY",BODY,{"derivedFrom":makeQuery(id+"F19.opPattern","COPY",BODY,{"derivedFrom":makeQuery(id+"F18.opPattern","COPY",BODY,{"derivedFrom":makeQuery(id+"F1.opExtrude","SWEPT_BODY",BODY,{"disambiguationData":[OSD([sQuery(id+"F0.wireOp",EDGE,"E0")])]}),"instanceName":"1"}),"instanceName":"1"}),"instanceName":"1"}),"instanceName":"1"}),"instanceName":"1"}),"instanceName":"1"}),"instanceName":"1"}),"instanceName":"1"}),"instanceName":"1"}),"instanceName":"1"}),"instanceName":"1"}),"instanceName":"1"}),"instanceName":"1"}),"instanceName":"1"}),"instanceName":"1"}),"instanceName":"1"}),"instanceName":"1"}),"instanceName":"1"}),"instanceName":"1"}),"instanceName":"1"}),"instanceName":"1"}),"instanceName":"1"}),"instanceName":"1"}),"instanceName":"1"}),"instanceName":"1"}),"instanceName":"1"});
            transform(context, id + "F64", {"entities" : qUnion([Q0]), "transformType" : TransformType.TRANSLATION_3D, "dx" : 0 * mm, "dy" : -2897 * mm, "dz" : 0 * mm, "makeCopy" : true});
        }
        {
            var Q0;
            Q0=makeQuery(id+"F64.opPattern","COPY",BODY,{"derivedFrom":makeQuery(id+"F63.opPattern","COPY",BODY,{"derivedFrom":makeQuery(id+"F58.opPattern","COPY",BODY,{"derivedFrom":makeQuery(id+"F57.opPattern","COPY",BODY,{"derivedFrom":makeQuery(id+"F56.opPattern","COPY",BODY,{"derivedFrom":makeQuery(id+"F41.opPattern","COPY",BODY,{"derivedFrom":makeQuery(id+"F38.opPattern","COPY",BODY,{"derivedFrom":makeQuery(id+"F37.opPattern","COPY",BODY,{"derivedFrom":makeQuery(id+"F36.opPattern","COPY",BODY,{"derivedFrom":makeQuery(id+"F35.opPattern","COPY",BODY,{"derivedFrom":makeQuery(id+"F34.opPattern","COPY",BODY,{"derivedFrom":makeQuery(id+"F33.opPattern","COPY",BODY,{"derivedFrom":makeQuery(id+"F32.opPattern","COPY",BODY,{"derivedFrom":makeQuery(id+"F31.opPattern","COPY",BODY,{"derivedFrom":makeQuery(id+"F30.opPattern","COPY",BODY,{"derivedFrom":makeQuery(id+"F29.opPattern","COPY",BODY,{"derivedFrom":makeQuery(id+"F28.opPattern","COPY",BODY,{"derivedFrom":makeQuery(id+"F27.opPattern","COPY",BODY,{"derivedFrom":makeQuery(id+"F26.opPattern","COPY",BODY,{"derivedFrom":makeQuery(id+"F25.opPattern","COPY",BODY,{"derivedFrom":makeQuery(id+"F24.opPattern","COPY",BODY,{"derivedFrom":makeQuery(id+"F23.opPattern","COPY",BODY,{"derivedFrom":makeQuery(id+"F22.opPattern","COPY",BODY,{"derivedFrom":makeQuery(id+"F21.opPattern","COPY",BODY,{"derivedFrom":makeQuery(id+"F20.opPattern","COPY",BODY,{"derivedFrom":makeQuery(id+"F19.opPattern","COPY",BODY,{"derivedFrom":makeQuery(id+"F18.opPattern","COPY",BODY,{"derivedFrom":makeQuery(id+"F1.opExtrude","SWEPT_BODY",BODY,{"disambiguationData":[OSD([sQuery(id+"F0.wireOp",EDGE,"E0")])]}),"instanceName":"1"}),"instanceName":"1"}),"instanceName":"1"}),"instanceName":"1"}),"instanceName":"1"}),"instanceName":"1"}),"instanceName":"1"}),"instanceName":"1"}),"instanceName":"1"}),"instanceName":"1"}),"instanceName":"1"}),"instanceName":"1"}),"instanceName":"1"}),"instanceName":"1"}),"instanceName":"1"}),"instanceName":"1"}),"instanceName":"1"}),"instanceName":"1"}),"instanceName":"1"}),"instanceName":"1"}),"instanceName":"1"}),"instanceName":"1"}),"instanceName":"1"}),"instanceName":"1"}),"instanceName":"1"}),"instanceName":"1"}),"instanceName":"1"});
            transform(context, id + "F65", {"entities" : qUnion([Q0]), "transformType" : TransformType.TRANSLATION_3D, "dx" : 0 * mm, "dy" : -2897 * mm, "dz" : 0 * mm, "makeCopy" : true});
        }
        {
            var Q0;
            Q0=qCreatedBy(makeId("Front.planeOp"),FACE);
            var sketch = newSketch(context, id + "F66", { "sketchPlane" : qUnion([Q0])});
            skLineSegment(sketch, "E1.bottom", {"start": v(-62.41, 1250.16) * mm, "end": v(59877.59, 1250.16) * mm});
            skLineSegment(sketch, "E1.top", {"start": v(-62.41, 1133.64) * mm, "end": v(59877.59, 1133.64) * mm});
            skLineSegment(sketch, "E1.left", {"start": v(-62.41, 1250.16) * mm, "end": v(-62.41, 1133.64) * mm});
            skLineSegment(sketch, "E1.right", {"start": v(59877.59, 1250.16) * mm, "end": v(59877.59, 1133.64) * mm});
            skSolve(sketch);
        }
        {
            var Q0;
            Q0=makeQuery(id+"F57.opPattern","COPY",BODY,{"derivedFrom":makeQuery(id+"F56.opPattern","COPY",BODY,{"derivedFrom":makeQuery(id+"F41.opPattern","COPY",BODY,{"derivedFrom":makeQuery(id+"F38.opPattern","COPY",BODY,{"derivedFrom":makeQuery(id+"F37.opPattern","COPY",BODY,{"derivedFrom":makeQuery(id+"F36.opPattern","COPY",BODY,{"derivedFrom":makeQuery(id+"F35.opPattern","COPY",BODY,{"derivedFrom":makeQuery(id+"F34.opPattern","COPY",BODY,{"derivedFrom":makeQuery(id+"F33.opPattern","COPY",BODY,{"derivedFrom":makeQuery(id+"F32.opPattern","COPY",BODY,{"derivedFrom":makeQuery(id+"F31.opPattern","COPY",BODY,{"derivedFrom":makeQuery(id+"F30.opPattern","COPY",BODY,{"derivedFrom":makeQuery(id+"F29.opPattern","COPY",BODY,{"derivedFrom":makeQuery(id+"F28.opPattern","COPY",BODY,{"derivedFrom":makeQuery(id+"F27.opPattern","COPY",BODY,{"derivedFrom":makeQuery(id+"F26.opPattern","COPY",BODY,{"derivedFrom":makeQuery(id+"F25.opPattern","COPY",BODY,{"derivedFrom":makeQuery(id+"F24.opPattern","COPY",BODY,{"derivedFrom":makeQuery(id+"F23.opPattern","COPY",BODY,{"derivedFrom":makeQuery(id+"F22.opPattern","COPY",BODY,{"derivedFrom":makeQuery(id+"F21.opPattern","COPY",BODY,{"derivedFrom":makeQuery(id+"F20.opPattern","COPY",BODY,{"derivedFrom":makeQuery(id+"F19.opPattern","COPY",BODY,{"derivedFrom":makeQuery(id+"F18.opPattern","COPY",BODY,{"derivedFrom":makeQuery(id+"F1.opExtrude","SWEPT_BODY",BODY,{"disambiguationData":[OSD([sQuery(id+"F0.wireOp",EDGE,"E0")])]}),"instanceName":"1"}),"instanceName":"1"}),"instanceName":"1"}),"instanceName":"1"}),"instanceName":"1"}),"instanceName":"1"}),"instanceName":"1"}),"instanceName":"1"}),"instanceName":"1"}),"instanceName":"1"}),"instanceName":"1"}),"instanceName":"1"}),"instanceName":"1"}),"instanceName":"1"}),"instanceName":"1"}),"instanceName":"1"}),"instanceName":"1"}),"instanceName":"1"}),"instanceName":"1"}),"instanceName":"1"}),"instanceName":"1"}),"instanceName":"1"}),"instanceName":"1"}),"instanceName":"1"});
            transform(context, id + "F67", {"entities" : qUnion([Q0]), "transformType" : TransformType.TRANSLATION_3D, "dx" : 6660 * mm, "dy" : 0 * mm, "dz" : 0 * mm, "makeCopy" : true});
        }
        {
            var Q0;
            Q0=makeQuery(id+"F56.opPattern","COPY",BODY,{"derivedFrom":makeQuery(id+"F41.opPattern","COPY",BODY,{"derivedFrom":makeQuery(id+"F38.opPattern","COPY",BODY,{"derivedFrom":makeQuery(id+"F37.opPattern","COPY",BODY,{"derivedFrom":makeQuery(id+"F36.opPattern","COPY",BODY,{"derivedFrom":makeQuery(id+"F35.opPattern","COPY",BODY,{"derivedFrom":makeQuery(id+"F34.opPattern","COPY",BODY,{"derivedFrom":makeQuery(id+"F33.opPattern","COPY",BODY,{"derivedFrom":makeQuery(id+"F32.opPattern","COPY",BODY,{"derivedFrom":makeQuery(id+"F31.opPattern","COPY",BODY,{"derivedFrom":makeQuery(id+"F30.opPattern","COPY",BODY,{"derivedFrom":makeQuery(id+"F29.opPattern","COPY",BODY,{"derivedFrom":makeQuery(id+"F28.opPattern","COPY",BODY,{"derivedFrom":makeQuery(id+"F27.opPattern","COPY",BODY,{"derivedFrom":makeQuery(id+"F26.opPattern","COPY",BODY,{"derivedFrom":makeQuery(id+"F25.opPattern","COPY",BODY,{"derivedFrom":makeQuery(id+"F24.opPattern","COPY",BODY,{"derivedFrom":makeQuery(id+"F23.opPattern","COPY",BODY,{"derivedFrom":makeQuery(id+"F22.opPattern","COPY",BODY,{"derivedFrom":makeQuery(id+"F21.opPattern","COPY",BODY,{"derivedFrom":makeQuery(id+"F20.opPattern","COPY",BODY,{"derivedFrom":makeQuery(id+"F19.opPattern","COPY",BODY,{"derivedFrom":makeQuery(id+"F18.opPattern","COPY",BODY,{"derivedFrom":makeQuery(id+"F1.opExtrude","SWEPT_BODY",BODY,{"disambiguationData":[OSD([sQuery(id+"F0.wireOp",EDGE,"E0")])]}),"instanceName":"1"}),"instanceName":"1"}),"instanceName":"1"}),"instanceName":"1"}),"instanceName":"1"}),"instanceName":"1"}),"instanceName":"1"}),"instanceName":"1"}),"instanceName":"1"}),"instanceName":"1"}),"instanceName":"1"}),"instanceName":"1"}),"instanceName":"1"}),"instanceName":"1"}),"instanceName":"1"}),"instanceName":"1"}),"instanceName":"1"}),"instanceName":"1"}),"instanceName":"1"}),"instanceName":"1"}),"instanceName":"1"}),"instanceName":"1"}),"instanceName":"1"});
            transform(context, id + "F68", {"entities" : qUnion([Q0]), "transformType" : TransformType.TRANSLATION_3D, "dx" : 6660 * mm, "dy" : 0 * mm, "dz" : 0 * mm, "makeCopy" : true});
        }
        {
            var Q0;
            Q0=makeQuery(id+"F63.opPattern","COPY",BODY,{"derivedFrom":makeQuery(id+"F58.opPattern","COPY",BODY,{"derivedFrom":makeQuery(id+"F57.opPattern","COPY",BODY,{"derivedFrom":makeQuery(id+"F56.opPattern","COPY",BODY,{"derivedFrom":makeQuery(id+"F41.opPattern","COPY",BODY,{"derivedFrom":makeQuery(id+"F38.opPattern","COPY",BODY,{"derivedFrom":makeQuery(id+"F37.opPattern","COPY",BODY,{"derivedFrom":makeQuery(id+"F36.opPattern","COPY",BODY,{"derivedFrom":makeQuery(id+"F35.opPattern","COPY",BODY,{"derivedFrom":makeQuery(id+"F34.opPattern","COPY",BODY,{"derivedFrom":makeQuery(id+"F33.opPattern","COPY",BODY,{"derivedFrom":makeQuery(id+"F32.opPattern","COPY",BODY,{"derivedFrom":makeQuery(id+"F31.opPattern","COPY",BODY,{"derivedFrom":makeQuery(id+"F30.opPattern","COPY",BODY,{"derivedFrom":makeQuery(id+"F29.opPattern","COPY",BODY,{"derivedFrom":makeQuery(id+"F28.opPattern","COPY",BODY,{"derivedFrom":makeQuery(id+"F27.opPattern","COPY",BODY,{"derivedFrom":makeQuery(id+"F26.opPattern","COPY",BODY,{"derivedFrom":makeQuery(id+"F25.opPattern","COPY",BODY,{"derivedFrom":makeQuery(id+"F24.opPattern","COPY",BODY,{"derivedFrom":makeQuery(id+"F23.opPattern","COPY",BODY,{"derivedFrom":makeQuery(id+"F22.opPattern","COPY",BODY,{"derivedFrom":makeQuery(id+"F21.opPattern","COPY",BODY,{"derivedFrom":makeQuery(id+"F20.opPattern","COPY",BODY,{"derivedFrom":makeQuery(id+"F19.opPattern","COPY",BODY,{"derivedFrom":makeQuery(id+"F18.opPattern","COPY",BODY,{"derivedFrom":makeQuery(id+"F1.opExtrude","SWEPT_BODY",BODY,{"disambiguationData":[OSD([sQuery(id+"F0.wireOp",EDGE,"E0")])]}),"instanceName":"1"}),"instanceName":"1"}),"instanceName":"1"}),"instanceName":"1"}),"instanceName":"1"}),"instanceName":"1"}),"instanceName":"1"}),"instanceName":"1"}),"instanceName":"1"}),"instanceName":"1"}),"instanceName":"1"}),"instanceName":"1"}),"instanceName":"1"}),"instanceName":"1"}),"instanceName":"1"}),"instanceName":"1"}),"instanceName":"1"}),"instanceName":"1"}),"instanceName":"1"}),"instanceName":"1"}),"instanceName":"1"}),"instanceName":"1"}),"instanceName":"1"}),"instanceName":"1"}),"instanceName":"1"}),"instanceName":"1"});
            transform(context, id + "F69", {"entities" : qUnion([Q0]), "transformType" : TransformType.TRANSLATION_3D, "dx" : 6660 * mm, "dy" : 0 * mm, "dz" : 0 * mm, "makeCopy" : true});
        }
        {
            var Q0;
            Q0=makeQuery(id+"F58.opPattern","COPY",BODY,{"derivedFrom":makeQuery(id+"F57.opPattern","COPY",BODY,{"derivedFrom":makeQuery(id+"F56.opPattern","COPY",BODY,{"derivedFrom":makeQuery(id+"F41.opPattern","COPY",BODY,{"derivedFrom":makeQuery(id+"F38.opPattern","COPY",BODY,{"derivedFrom":makeQuery(id+"F37.opPattern","COPY",BODY,{"derivedFrom":makeQuery(id+"F36.opPattern","COPY",BODY,{"derivedFrom":makeQuery(id+"F35.opPattern","COPY",BODY,{"derivedFrom":makeQuery(id+"F34.opPattern","COPY",BODY,{"derivedFrom":makeQuery(id+"F33.opPattern","COPY",BODY,{"derivedFrom":makeQuery(id+"F32.opPattern","COPY",BODY,{"derivedFrom":makeQuery(id+"F31.opPattern","COPY",BODY,{"derivedFrom":makeQuery(id+"F30.opPattern","COPY",BODY,{"derivedFrom":makeQuery(id+"F29.opPattern","COPY",BODY,{"derivedFrom":makeQuery(id+"F28.opPattern","COPY",BODY,{"derivedFrom":makeQuery(id+"F27.opPattern","COPY",BODY,{"derivedFrom":makeQuery(id+"F26.opPattern","COPY",BODY,{"derivedFrom":makeQuery(id+"F25.opPattern","COPY",BODY,{"derivedFrom":makeQuery(id+"F24.opPattern","COPY",BODY,{"derivedFrom":makeQuery(id+"F23.opPattern","COPY",BODY,{"derivedFrom":makeQuery(id+"F22.opPattern","COPY",BODY,{"derivedFrom":makeQuery(id+"F21.opPattern","COPY",BODY,{"derivedFrom":makeQuery(id+"F20.opPattern","COPY",BODY,{"derivedFrom":makeQuery(id+"F19.opPattern","COPY",BODY,{"derivedFrom":makeQuery(id+"F18.opPattern","COPY",BODY,{"derivedFrom":makeQuery(id+"F1.opExtrude","SWEPT_BODY",BODY,{"disambiguationData":[OSD([sQuery(id+"F0.wireOp",EDGE,"E0")])]}),"instanceName":"1"}),"instanceName":"1"}),"instanceName":"1"}),"instanceName":"1"}),"instanceName":"1"}),"instanceName":"1"}),"instanceName":"1"}),"instanceName":"1"}),"instanceName":"1"}),"instanceName":"1"}),"instanceName":"1"}),"instanceName":"1"}),"instanceName":"1"}),"instanceName":"1"}),"instanceName":"1"}),"instanceName":"1"}),"instanceName":"1"}),"instanceName":"1"}),"instanceName":"1"}),"instanceName":"1"}),"instanceName":"1"}),"instanceName":"1"}),"instanceName":"1"}),"instanceName":"1"}),"instanceName":"1"});
            transform(context, id + "F70", {"entities" : qUnion([Q0]), "transformType" : TransformType.TRANSLATION_3D, "dx" : 6660 * mm, "dy" : 0 * mm, "dz" : 0 * mm, "makeCopy" : true});
        }
        {
            var Q0;
            Q0=makeQuery(id+"F64.opPattern","COPY",BODY,{"derivedFrom":makeQuery(id+"F63.opPattern","COPY",BODY,{"derivedFrom":makeQuery(id+"F58.opPattern","COPY",BODY,{"derivedFrom":makeQuery(id+"F57.opPattern","COPY",BODY,{"derivedFrom":makeQuery(id+"F56.opPattern","COPY",BODY,{"derivedFrom":makeQuery(id+"F41.opPattern","COPY",BODY,{"derivedFrom":makeQuery(id+"F38.opPattern","COPY",BODY,{"derivedFrom":makeQuery(id+"F37.opPattern","COPY",BODY,{"derivedFrom":makeQuery(id+"F36.opPattern","COPY",BODY,{"derivedFrom":makeQuery(id+"F35.opPattern","COPY",BODY,{"derivedFrom":makeQuery(id+"F34.opPattern","COPY",BODY,{"derivedFrom":makeQuery(id+"F33.opPattern","COPY",BODY,{"derivedFrom":makeQuery(id+"F32.opPattern","COPY",BODY,{"derivedFrom":makeQuery(id+"F31.opPattern","COPY",BODY,{"derivedFrom":makeQuery(id+"F30.opPattern","COPY",BODY,{"derivedFrom":makeQuery(id+"F29.opPattern","COPY",BODY,{"derivedFrom":makeQuery(id+"F28.opPattern","COPY",BODY,{"derivedFrom":makeQuery(id+"F27.opPattern","COPY",BODY,{"derivedFrom":makeQuery(id+"F26.opPattern","COPY",BODY,{"derivedFrom":makeQuery(id+"F25.opPattern","COPY",BODY,{"derivedFrom":makeQuery(id+"F24.opPattern","COPY",BODY,{"derivedFrom":makeQuery(id+"F23.opPattern","COPY",BODY,{"derivedFrom":makeQuery(id+"F22.opPattern","COPY",BODY,{"derivedFrom":makeQuery(id+"F21.opPattern","COPY",BODY,{"derivedFrom":makeQuery(id+"F20.opPattern","COPY",BODY,{"derivedFrom":makeQuery(id+"F19.opPattern","COPY",BODY,{"derivedFrom":makeQuery(id+"F18.opPattern","COPY",BODY,{"derivedFrom":makeQuery(id+"F1.opExtrude","SWEPT_BODY",BODY,{"disambiguationData":[OSD([sQuery(id+"F0.wireOp",EDGE,"E0")])]}),"instanceName":"1"}),"instanceName":"1"}),"instanceName":"1"}),"instanceName":"1"}),"instanceName":"1"}),"instanceName":"1"}),"instanceName":"1"}),"instanceName":"1"}),"instanceName":"1"}),"instanceName":"1"}),"instanceName":"1"}),"instanceName":"1"}),"instanceName":"1"}),"instanceName":"1"}),"instanceName":"1"}),"instanceName":"1"}),"instanceName":"1"}),"instanceName":"1"}),"instanceName":"1"}),"instanceName":"1"}),"instanceName":"1"}),"instanceName":"1"}),"instanceName":"1"}),"instanceName":"1"}),"instanceName":"1"}),"instanceName":"1"}),"instanceName":"1"});
            transform(context, id + "F71", {"entities" : qUnion([Q0]), "transformType" : TransformType.TRANSLATION_3D, "dx" : 6660 * mm, "dy" : 0 * mm, "dz" : 0 * mm, "makeCopy" : true});
        }
        {
            var Q0;
            Q0=makeQuery(id+"F65.opPattern","COPY",BODY,{"derivedFrom":makeQuery(id+"F64.opPattern","COPY",BODY,{"derivedFrom":makeQuery(id+"F63.opPattern","COPY",BODY,{"derivedFrom":makeQuery(id+"F58.opPattern","COPY",BODY,{"derivedFrom":makeQuery(id+"F57.opPattern","COPY",BODY,{"derivedFrom":makeQuery(id+"F56.opPattern","COPY",BODY,{"derivedFrom":makeQuery(id+"F41.opPattern","COPY",BODY,{"derivedFrom":makeQuery(id+"F38.opPattern","COPY",BODY,{"derivedFrom":makeQuery(id+"F37.opPattern","COPY",BODY,{"derivedFrom":makeQuery(id+"F36.opPattern","COPY",BODY,{"derivedFrom":makeQuery(id+"F35.opPattern","COPY",BODY,{"derivedFrom":makeQuery(id+"F34.opPattern","COPY",BODY,{"derivedFrom":makeQuery(id+"F33.opPattern","COPY",BODY,{"derivedFrom":makeQuery(id+"F32.opPattern","COPY",BODY,{"derivedFrom":makeQuery(id+"F31.opPattern","COPY",BODY,{"derivedFrom":makeQuery(id+"F30.opPattern","COPY",BODY,{"derivedFrom":makeQuery(id+"F29.opPattern","COPY",BODY,{"derivedFrom":makeQuery(id+"F28.opPattern","COPY",BODY,{"derivedFrom":makeQuery(id+"F27.opPattern","COPY",BODY,{"derivedFrom":makeQuery(id+"F26.opPattern","COPY",BODY,{"derivedFrom":makeQuery(id+"F25.opPattern","COPY",BODY,{"derivedFrom":makeQuery(id+"F24.opPattern","COPY",BODY,{"derivedFrom":makeQuery(id+"F23.opPattern","COPY",BODY,{"derivedFrom":makeQuery(id+"F22.opPattern","COPY",BODY,{"derivedFrom":makeQuery(id+"F21.opPattern","COPY",BODY,{"derivedFrom":makeQuery(id+"F20.opPattern","COPY",BODY,{"derivedFrom":makeQuery(id+"F19.opPattern","COPY",BODY,{"derivedFrom":makeQuery(id+"F18.opPattern","COPY",BODY,{"derivedFrom":makeQuery(id+"F1.opExtrude","SWEPT_BODY",BODY,{"disambiguationData":[OSD([sQuery(id+"F0.wireOp",EDGE,"E0")])]}),"instanceName":"1"}),"instanceName":"1"}),"instanceName":"1"}),"instanceName":"1"}),"instanceName":"1"}),"instanceName":"1"}),"instanceName":"1"}),"instanceName":"1"}),"instanceName":"1"}),"instanceName":"1"}),"instanceName":"1"}),"instanceName":"1"}),"instanceName":"1"}),"instanceName":"1"}),"instanceName":"1"}),"instanceName":"1"}),"instanceName":"1"}),"instanceName":"1"}),"instanceName":"1"}),"instanceName":"1"}),"instanceName":"1"}),"instanceName":"1"}),"instanceName":"1"}),"instanceName":"1"}),"instanceName":"1"}),"instanceName":"1"}),"instanceName":"1"}),"instanceName":"1"});
            transform(context, id + "F72", {"entities" : qUnion([Q0]), "transformType" : TransformType.TRANSLATION_3D, "dx" : 6660 * mm, "dy" : 0 * mm, "dz" : 0 * mm, "makeCopy" : true});
        }
        {
            var Q0;
            Q0=makeQuery(id+"F17.opPattern","COPY",BODY,{"derivedFrom":makeQuery(id+"F16.opPattern","COPY",BODY,{"derivedFrom":makeQuery(id+"F15.opPattern","COPY",BODY,{"derivedFrom":makeQuery(id+"F14.opPattern","COPY",BODY,{"derivedFrom":makeQuery(id+"F13.opPattern","COPY",BODY,{"derivedFrom":makeQuery(id+"F12.opPattern","COPY",BODY,{"derivedFrom":makeQuery(id+"F11.opPattern","COPY",BODY,{"derivedFrom":makeQuery(id+"F10.opPattern","COPY",BODY,{"derivedFrom":makeQuery(id+"F9.opPattern","COPY",BODY,{"derivedFrom":makeQuery(id+"F8.opPattern","COPY",BODY,{"derivedFrom":makeQuery(id+"F7.opPattern","COPY",BODY,{"derivedFrom":makeQuery(id+"F6.opPattern","COPY",BODY,{"derivedFrom":makeQuery(id+"F5.opPattern","COPY",BODY,{"derivedFrom":makeQuery(id+"F4.opPattern","COPY",BODY,{"derivedFrom":makeQuery(id+"F3.opPattern","COPY",BODY,{"derivedFrom":makeQuery(id+"F2.opPattern","COPY",BODY,{"derivedFrom":makeQuery(id+"F1.opExtrude","SWEPT_BODY",BODY,{"disambiguationData":[OSD([sQuery(id+"F0.wireOp",EDGE,"E0")])]}),"instanceName":"1"}),"instanceName":"1"}),"instanceName":"1"}),"instanceName":"1"}),"instanceName":"1"}),"instanceName":"1"}),"instanceName":"1"}),"instanceName":"1"}),"instanceName":"1"}),"instanceName":"1"}),"instanceName":"1"}),"instanceName":"1"}),"instanceName":"1"}),"instanceName":"1"}),"instanceName":"1"}),"instanceName":"1"});
            transform(context, id + "F73", {"entities" : qUnion([Q0]), "transformType" : TransformType.TRANSLATION_3D, "dx" : 3330 * mm, "dy" : 0 * mm, "dz" : 0 * mm, "makeCopy" : true});
        }
        {
            var Q0;
            Q0=makeQuery(id+"F73.opPattern","COPY",BODY,{"derivedFrom":makeQuery(id+"F17.opPattern","COPY",BODY,{"derivedFrom":makeQuery(id+"F16.opPattern","COPY",BODY,{"derivedFrom":makeQuery(id+"F15.opPattern","COPY",BODY,{"derivedFrom":makeQuery(id+"F14.opPattern","COPY",BODY,{"derivedFrom":makeQuery(id+"F13.opPattern","COPY",BODY,{"derivedFrom":makeQuery(id+"F12.opPattern","COPY",BODY,{"derivedFrom":makeQuery(id+"F11.opPattern","COPY",BODY,{"derivedFrom":makeQuery(id+"F10.opPattern","COPY",BODY,{"derivedFrom":makeQuery(id+"F9.opPattern","COPY",BODY,{"derivedFrom":makeQuery(id+"F8.opPattern","COPY",BODY,{"derivedFrom":makeQuery(id+"F7.opPattern","COPY",BODY,{"derivedFrom":makeQuery(id+"F6.opPattern","COPY",BODY,{"derivedFrom":makeQuery(id+"F5.opPattern","COPY",BODY,{"derivedFrom":makeQuery(id+"F4.opPattern","COPY",BODY,{"derivedFrom":makeQuery(id+"F3.opPattern","COPY",BODY,{"derivedFrom":makeQuery(id+"F2.opPattern","COPY",BODY,{"derivedFrom":makeQuery(id+"F1.opExtrude","SWEPT_BODY",BODY,{"disambiguationData":[OSD([sQuery(id+"F0.wireOp",EDGE,"E0")])]}),"instanceName":"1"}),"instanceName":"1"}),"instanceName":"1"}),"instanceName":"1"}),"instanceName":"1"}),"instanceName":"1"}),"instanceName":"1"}),"instanceName":"1"}),"instanceName":"1"}),"instanceName":"1"}),"instanceName":"1"}),"instanceName":"1"}),"instanceName":"1"}),"instanceName":"1"}),"instanceName":"1"}),"instanceName":"1"}),"instanceName":"1"});
            transform(context, id + "F74", {"entities" : qUnion([Q0]), "transformType" : TransformType.TRANSLATION_3D, "dx" : 3330 * mm, "dy" : 0 * mm, "dz" : 0 * mm, "makeCopy" : true});
        }
        {
            var Q0;
            Q0=makeQuery(id+"F41.opPattern","COPY",BODY,{"derivedFrom":makeQuery(id+"F38.opPattern","COPY",BODY,{"derivedFrom":makeQuery(id+"F37.opPattern","COPY",BODY,{"derivedFrom":makeQuery(id+"F36.opPattern","COPY",BODY,{"derivedFrom":makeQuery(id+"F35.opPattern","COPY",BODY,{"derivedFrom":makeQuery(id+"F34.opPattern","COPY",BODY,{"derivedFrom":makeQuery(id+"F33.opPattern","COPY",BODY,{"derivedFrom":makeQuery(id+"F32.opPattern","COPY",BODY,{"derivedFrom":makeQuery(id+"F31.opPattern","COPY",BODY,{"derivedFrom":makeQuery(id+"F30.opPattern","COPY",BODY,{"derivedFrom":makeQuery(id+"F29.opPattern","COPY",BODY,{"derivedFrom":makeQuery(id+"F28.opPattern","COPY",BODY,{"derivedFrom":makeQuery(id+"F27.opPattern","COPY",BODY,{"derivedFrom":makeQuery(id+"F26.opPattern","COPY",BODY,{"derivedFrom":makeQuery(id+"F25.opPattern","COPY",BODY,{"derivedFrom":makeQuery(id+"F24.opPattern","COPY",BODY,{"derivedFrom":makeQuery(id+"F23.opPattern","COPY",BODY,{"derivedFrom":makeQuery(id+"F22.opPattern","COPY",BODY,{"derivedFrom":makeQuery(id+"F21.opPattern","COPY",BODY,{"derivedFrom":makeQuery(id+"F20.opPattern","COPY",BODY,{"derivedFrom":makeQuery(id+"F19.opPattern","COPY",BODY,{"derivedFrom":makeQuery(id+"F18.opPattern","COPY",BODY,{"derivedFrom":makeQuery(id+"F1.opExtrude","SWEPT_BODY",BODY,{"disambiguationData":[OSD([sQuery(id+"F0.wireOp",EDGE,"E0")])]}),"instanceName":"1"}),"instanceName":"1"}),"instanceName":"1"}),"instanceName":"1"}),"instanceName":"1"}),"instanceName":"1"}),"instanceName":"1"}),"instanceName":"1"}),"instanceName":"1"}),"instanceName":"1"}),"instanceName":"1"}),"instanceName":"1"}),"instanceName":"1"}),"instanceName":"1"}),"instanceName":"1"}),"instanceName":"1"}),"instanceName":"1"}),"instanceName":"1"}),"instanceName":"1"}),"instanceName":"1"}),"instanceName":"1"}),"instanceName":"1"});
            transform(context, id + "F75", {"entities" : qUnion([Q0]), "transformType" : TransformType.TRANSLATION_3D, "dx" : 3330 * mm, "dy" : 0 * mm, "dz" : 0 * mm, "makeCopy" : true});
        }
        {
            var Q0;
            Q0=makeQuery(id+"F75.opPattern","COPY",BODY,{"derivedFrom":makeQuery(id+"F41.opPattern","COPY",BODY,{"derivedFrom":makeQuery(id+"F38.opPattern","COPY",BODY,{"derivedFrom":makeQuery(id+"F37.opPattern","COPY",BODY,{"derivedFrom":makeQuery(id+"F36.opPattern","COPY",BODY,{"derivedFrom":makeQuery(id+"F35.opPattern","COPY",BODY,{"derivedFrom":makeQuery(id+"F34.opPattern","COPY",BODY,{"derivedFrom":makeQuery(id+"F33.opPattern","COPY",BODY,{"derivedFrom":makeQuery(id+"F32.opPattern","COPY",BODY,{"derivedFrom":makeQuery(id+"F31.opPattern","COPY",BODY,{"derivedFrom":makeQuery(id+"F30.opPattern","COPY",BODY,{"derivedFrom":makeQuery(id+"F29.opPattern","COPY",BODY,{"derivedFrom":makeQuery(id+"F28.opPattern","COPY",BODY,{"derivedFrom":makeQuery(id+"F27.opPattern","COPY",BODY,{"derivedFrom":makeQuery(id+"F26.opPattern","COPY",BODY,{"derivedFrom":makeQuery(id+"F25.opPattern","COPY",BODY,{"derivedFrom":makeQuery(id+"F24.opPattern","COPY",BODY,{"derivedFrom":makeQuery(id+"F23.opPattern","COPY",BODY,{"derivedFrom":makeQuery(id+"F22.opPattern","COPY",BODY,{"derivedFrom":makeQuery(id+"F21.opPattern","COPY",BODY,{"derivedFrom":makeQuery(id+"F20.opPattern","COPY",BODY,{"derivedFrom":makeQuery(id+"F19.opPattern","COPY",BODY,{"derivedFrom":makeQuery(id+"F18.opPattern","COPY",BODY,{"derivedFrom":makeQuery(id+"F1.opExtrude","SWEPT_BODY",BODY,{"disambiguationData":[OSD([sQuery(id+"F0.wireOp",EDGE,"E0")])]}),"instanceName":"1"}),"instanceName":"1"}),"instanceName":"1"}),"instanceName":"1"}),"instanceName":"1"}),"instanceName":"1"}),"instanceName":"1"}),"instanceName":"1"}),"instanceName":"1"}),"instanceName":"1"}),"instanceName":"1"}),"instanceName":"1"}),"instanceName":"1"}),"instanceName":"1"}),"instanceName":"1"}),"instanceName":"1"}),"instanceName":"1"}),"instanceName":"1"}),"instanceName":"1"}),"instanceName":"1"}),"instanceName":"1"}),"instanceName":"1"}),"instanceName":"1"});
            transform(context, id + "F76", {"entities" : qUnion([Q0]), "transformType" : TransformType.TRANSLATION_3D, "dx" : 3330 * mm, "dy" : 0 * mm, "dz" : 0 * mm, "makeCopy" : true});
        }
        {
            var Q0;
            Q0=makeQuery(id+"F56.opPattern","COPY",BODY,{"derivedFrom":makeQuery(id+"F41.opPattern","COPY",BODY,{"derivedFrom":makeQuery(id+"F38.opPattern","COPY",BODY,{"derivedFrom":makeQuery(id+"F37.opPattern","COPY",BODY,{"derivedFrom":makeQuery(id+"F36.opPattern","COPY",BODY,{"derivedFrom":makeQuery(id+"F35.opPattern","COPY",BODY,{"derivedFrom":makeQuery(id+"F34.opPattern","COPY",BODY,{"derivedFrom":makeQuery(id+"F33.opPattern","COPY",BODY,{"derivedFrom":makeQuery(id+"F32.opPattern","COPY",BODY,{"derivedFrom":makeQuery(id+"F31.opPattern","COPY",BODY,{"derivedFrom":makeQuery(id+"F30.opPattern","COPY",BODY,{"derivedFrom":makeQuery(id+"F29.opPattern","COPY",BODY,{"derivedFrom":makeQuery(id+"F28.opPattern","COPY",BODY,{"derivedFrom":makeQuery(id+"F27.opPattern","COPY",BODY,{"derivedFrom":makeQuery(id+"F26.opPattern","COPY",BODY,{"derivedFrom":makeQuery(id+"F25.opPattern","COPY",BODY,{"derivedFrom":makeQuery(id+"F24.opPattern","COPY",BODY,{"derivedFrom":makeQuery(id+"F23.opPattern","COPY",BODY,{"derivedFrom":makeQuery(id+"F22.opPattern","COPY",BODY,{"derivedFrom":makeQuery(id+"F21.opPattern","COPY",BODY,{"derivedFrom":makeQuery(id+"F20.opPattern","COPY",BODY,{"derivedFrom":makeQuery(id+"F19.opPattern","COPY",BODY,{"derivedFrom":makeQuery(id+"F18.opPattern","COPY",BODY,{"derivedFrom":makeQuery(id+"F1.opExtrude","SWEPT_BODY",BODY,{"disambiguationData":[OSD([sQuery(id+"F0.wireOp",EDGE,"E0")])]}),"instanceName":"1"}),"instanceName":"1"}),"instanceName":"1"}),"instanceName":"1"}),"instanceName":"1"}),"instanceName":"1"}),"instanceName":"1"}),"instanceName":"1"}),"instanceName":"1"}),"instanceName":"1"}),"instanceName":"1"}),"instanceName":"1"}),"instanceName":"1"}),"instanceName":"1"}),"instanceName":"1"}),"instanceName":"1"}),"instanceName":"1"}),"instanceName":"1"}),"instanceName":"1"}),"instanceName":"1"}),"instanceName":"1"}),"instanceName":"1"}),"instanceName":"1"});
            deleteBodies(context, id + "F77", {"entities" : qUnion([Q0])});
        }
        {
            var Q0;
            Q0=makeQuery(id+"F57.opPattern","COPY",BODY,{"derivedFrom":makeQuery(id+"F56.opPattern","COPY",BODY,{"derivedFrom":makeQuery(id+"F41.opPattern","COPY",BODY,{"derivedFrom":makeQuery(id+"F38.opPattern","COPY",BODY,{"derivedFrom":makeQuery(id+"F37.opPattern","COPY",BODY,{"derivedFrom":makeQuery(id+"F36.opPattern","COPY",BODY,{"derivedFrom":makeQuery(id+"F35.opPattern","COPY",BODY,{"derivedFrom":makeQuery(id+"F34.opPattern","COPY",BODY,{"derivedFrom":makeQuery(id+"F33.opPattern","COPY",BODY,{"derivedFrom":makeQuery(id+"F32.opPattern","COPY",BODY,{"derivedFrom":makeQuery(id+"F31.opPattern","COPY",BODY,{"derivedFrom":makeQuery(id+"F30.opPattern","COPY",BODY,{"derivedFrom":makeQuery(id+"F29.opPattern","COPY",BODY,{"derivedFrom":makeQuery(id+"F28.opPattern","COPY",BODY,{"derivedFrom":makeQuery(id+"F27.opPattern","COPY",BODY,{"derivedFrom":makeQuery(id+"F26.opPattern","COPY",BODY,{"derivedFrom":makeQuery(id+"F25.opPattern","COPY",BODY,{"derivedFrom":makeQuery(id+"F24.opPattern","COPY",BODY,{"derivedFrom":makeQuery(id+"F23.opPattern","COPY",BODY,{"derivedFrom":makeQuery(id+"F22.opPattern","COPY",BODY,{"derivedFrom":makeQuery(id+"F21.opPattern","COPY",BODY,{"derivedFrom":makeQuery(id+"F20.opPattern","COPY",BODY,{"derivedFrom":makeQuery(id+"F19.opPattern","COPY",BODY,{"derivedFrom":makeQuery(id+"F18.opPattern","COPY",BODY,{"derivedFrom":makeQuery(id+"F1.opExtrude","SWEPT_BODY",BODY,{"disambiguationData":[OSD([sQuery(id+"F0.wireOp",EDGE,"E0")])]}),"instanceName":"1"}),"instanceName":"1"}),"instanceName":"1"}),"instanceName":"1"}),"instanceName":"1"}),"instanceName":"1"}),"instanceName":"1"}),"instanceName":"1"}),"instanceName":"1"}),"instanceName":"1"}),"instanceName":"1"}),"instanceName":"1"}),"instanceName":"1"}),"instanceName":"1"}),"instanceName":"1"}),"instanceName":"1"}),"instanceName":"1"}),"instanceName":"1"}),"instanceName":"1"}),"instanceName":"1"}),"instanceName":"1"}),"instanceName":"1"}),"instanceName":"1"}),"instanceName":"1"});
            var Q1;
            Q1=makeQuery(id+"F58.opPattern","COPY",BODY,{"derivedFrom":makeQuery(id+"F57.opPattern","COPY",BODY,{"derivedFrom":makeQuery(id+"F56.opPattern","COPY",BODY,{"derivedFrom":makeQuery(id+"F41.opPattern","COPY",BODY,{"derivedFrom":makeQuery(id+"F38.opPattern","COPY",BODY,{"derivedFrom":makeQuery(id+"F37.opPattern","COPY",BODY,{"derivedFrom":makeQuery(id+"F36.opPattern","COPY",BODY,{"derivedFrom":makeQuery(id+"F35.opPattern","COPY",BODY,{"derivedFrom":makeQuery(id+"F34.opPattern","COPY",BODY,{"derivedFrom":makeQuery(id+"F33.opPattern","COPY",BODY,{"derivedFrom":makeQuery(id+"F32.opPattern","COPY",BODY,{"derivedFrom":makeQuery(id+"F31.opPattern","COPY",BODY,{"derivedFrom":makeQuery(id+"F30.opPattern","COPY",BODY,{"derivedFrom":makeQuery(id+"F29.opPattern","COPY",BODY,{"derivedFrom":makeQuery(id+"F28.opPattern","COPY",BODY,{"derivedFrom":makeQuery(id+"F27.opPattern","COPY",BODY,{"derivedFrom":makeQuery(id+"F26.opPattern","COPY",BODY,{"derivedFrom":makeQuery(id+"F25.opPattern","COPY",BODY,{"derivedFrom":makeQuery(id+"F24.opPattern","COPY",BODY,{"derivedFrom":makeQuery(id+"F23.opPattern","COPY",BODY,{"derivedFrom":makeQuery(id+"F22.opPattern","COPY",BODY,{"derivedFrom":makeQuery(id+"F21.opPattern","COPY",BODY,{"derivedFrom":makeQuery(id+"F20.opPattern","COPY",BODY,{"derivedFrom":makeQuery(id+"F19.opPattern","COPY",BODY,{"derivedFrom":makeQuery(id+"F18.opPattern","COPY",BODY,{"derivedFrom":makeQuery(id+"F1.opExtrude","SWEPT_BODY",BODY,{"disambiguationData":[OSD([sQuery(id+"F0.wireOp",EDGE,"E0")])]}),"instanceName":"1"}),"instanceName":"1"}),"instanceName":"1"}),"instanceName":"1"}),"instanceName":"1"}),"instanceName":"1"}),"instanceName":"1"}),"instanceName":"1"}),"instanceName":"1"}),"instanceName":"1"}),"instanceName":"1"}),"instanceName":"1"}),"instanceName":"1"}),"instanceName":"1"}),"instanceName":"1"}),"instanceName":"1"}),"instanceName":"1"}),"instanceName":"1"}),"instanceName":"1"}),"instanceName":"1"}),"instanceName":"1"}),"instanceName":"1"}),"instanceName":"1"}),"instanceName":"1"}),"instanceName":"1"});
            var Q2;
            Q2=makeQuery(id+"F63.opPattern","COPY",BODY,{"derivedFrom":makeQuery(id+"F58.opPattern","COPY",BODY,{"derivedFrom":makeQuery(id+"F57.opPattern","COPY",BODY,{"derivedFrom":makeQuery(id+"F56.opPattern","COPY",BODY,{"derivedFrom":makeQuery(id+"F41.opPattern","COPY",BODY,{"derivedFrom":makeQuery(id+"F38.opPattern","COPY",BODY,{"derivedFrom":makeQuery(id+"F37.opPattern","COPY",BODY,{"derivedFrom":makeQuery(id+"F36.opPattern","COPY",BODY,{"derivedFrom":makeQuery(id+"F35.opPattern","COPY",BODY,{"derivedFrom":makeQuery(id+"F34.opPattern","COPY",BODY,{"derivedFrom":makeQuery(id+"F33.opPattern","COPY",BODY,{"derivedFrom":makeQuery(id+"F32.opPattern","COPY",BODY,{"derivedFrom":makeQuery(id+"F31.opPattern","COPY",BODY,{"derivedFrom":makeQuery(id+"F30.opPattern","COPY",BODY,{"derivedFrom":makeQuery(id+"F29.opPattern","COPY",BODY,{"derivedFrom":makeQuery(id+"F28.opPattern","COPY",BODY,{"derivedFrom":makeQuery(id+"F27.opPattern","COPY",BODY,{"derivedFrom":makeQuery(id+"F26.opPattern","COPY",BODY,{"derivedFrom":makeQuery(id+"F25.opPattern","COPY",BODY,{"derivedFrom":makeQuery(id+"F24.opPattern","COPY",BODY,{"derivedFrom":makeQuery(id+"F23.opPattern","COPY",BODY,{"derivedFrom":makeQuery(id+"F22.opPattern","COPY",BODY,{"derivedFrom":makeQuery(id+"F21.opPattern","COPY",BODY,{"derivedFrom":makeQuery(id+"F20.opPattern","COPY",BODY,{"derivedFrom":makeQuery(id+"F19.opPattern","COPY",BODY,{"derivedFrom":makeQuery(id+"F18.opPattern","COPY",BODY,{"derivedFrom":makeQuery(id+"F1.opExtrude","SWEPT_BODY",BODY,{"disambiguationData":[OSD([sQuery(id+"F0.wireOp",EDGE,"E0")])]}),"instanceName":"1"}),"instanceName":"1"}),"instanceName":"1"}),"instanceName":"1"}),"instanceName":"1"}),"instanceName":"1"}),"instanceName":"1"}),"instanceName":"1"}),"instanceName":"1"}),"instanceName":"1"}),"instanceName":"1"}),"instanceName":"1"}),"instanceName":"1"}),"instanceName":"1"}),"instanceName":"1"}),"instanceName":"1"}),"instanceName":"1"}),"instanceName":"1"}),"instanceName":"1"}),"instanceName":"1"}),"instanceName":"1"}),"instanceName":"1"}),"instanceName":"1"}),"instanceName":"1"}),"instanceName":"1"}),"instanceName":"1"});
            var Q3;
            Q3=makeQuery(id+"F64.opPattern","COPY",BODY,{"derivedFrom":makeQuery(id+"F63.opPattern","COPY",BODY,{"derivedFrom":makeQuery(id+"F58.opPattern","COPY",BODY,{"derivedFrom":makeQuery(id+"F57.opPattern","COPY",BODY,{"derivedFrom":makeQuery(id+"F56.opPattern","COPY",BODY,{"derivedFrom":makeQuery(id+"F41.opPattern","COPY",BODY,{"derivedFrom":makeQuery(id+"F38.opPattern","COPY",BODY,{"derivedFrom":makeQuery(id+"F37.opPattern","COPY",BODY,{"derivedFrom":makeQuery(id+"F36.opPattern","COPY",BODY,{"derivedFrom":makeQuery(id+"F35.opPattern","COPY",BODY,{"derivedFrom":makeQuery(id+"F34.opPattern","COPY",BODY,{"derivedFrom":makeQuery(id+"F33.opPattern","COPY",BODY,{"derivedFrom":makeQuery(id+"F32.opPattern","COPY",BODY,{"derivedFrom":makeQuery(id+"F31.opPattern","COPY",BODY,{"derivedFrom":makeQuery(id+"F30.opPattern","COPY",BODY,{"derivedFrom":makeQuery(id+"F29.opPattern","COPY",BODY,{"derivedFrom":makeQuery(id+"F28.opPattern","COPY",BODY,{"derivedFrom":makeQuery(id+"F27.opPattern","COPY",BODY,{"derivedFrom":makeQuery(id+"F26.opPattern","COPY",BODY,{"derivedFrom":makeQuery(id+"F25.opPattern","COPY",BODY,{"derivedFrom":makeQuery(id+"F24.opPattern","COPY",BODY,{"derivedFrom":makeQuery(id+"F23.opPattern","COPY",BODY,{"derivedFrom":makeQuery(id+"F22.opPattern","COPY",BODY,{"derivedFrom":makeQuery(id+"F21.opPattern","COPY",BODY,{"derivedFrom":makeQuery(id+"F20.opPattern","COPY",BODY,{"derivedFrom":makeQuery(id+"F19.opPattern","COPY",BODY,{"derivedFrom":makeQuery(id+"F18.opPattern","COPY",BODY,{"derivedFrom":makeQuery(id+"F1.opExtrude","SWEPT_BODY",BODY,{"disambiguationData":[OSD([sQuery(id+"F0.wireOp",EDGE,"E0")])]}),"instanceName":"1"}),"instanceName":"1"}),"instanceName":"1"}),"instanceName":"1"}),"instanceName":"1"}),"instanceName":"1"}),"instanceName":"1"}),"instanceName":"1"}),"instanceName":"1"}),"instanceName":"1"}),"instanceName":"1"}),"instanceName":"1"}),"instanceName":"1"}),"instanceName":"1"}),"instanceName":"1"}),"instanceName":"1"}),"instanceName":"1"}),"instanceName":"1"}),"instanceName":"1"}),"instanceName":"1"}),"instanceName":"1"}),"instanceName":"1"}),"instanceName":"1"}),"instanceName":"1"}),"instanceName":"1"}),"instanceName":"1"}),"instanceName":"1"});
            var Q4;
            Q4=makeQuery(id+"F65.opPattern","COPY",BODY,{"derivedFrom":makeQuery(id+"F64.opPattern","COPY",BODY,{"derivedFrom":makeQuery(id+"F63.opPattern","COPY",BODY,{"derivedFrom":makeQuery(id+"F58.opPattern","COPY",BODY,{"derivedFrom":makeQuery(id+"F57.opPattern","COPY",BODY,{"derivedFrom":makeQuery(id+"F56.opPattern","COPY",BODY,{"derivedFrom":makeQuery(id+"F41.opPattern","COPY",BODY,{"derivedFrom":makeQuery(id+"F38.opPattern","COPY",BODY,{"derivedFrom":makeQuery(id+"F37.opPattern","COPY",BODY,{"derivedFrom":makeQuery(id+"F36.opPattern","COPY",BODY,{"derivedFrom":makeQuery(id+"F35.opPattern","COPY",BODY,{"derivedFrom":makeQuery(id+"F34.opPattern","COPY",BODY,{"derivedFrom":makeQuery(id+"F33.opPattern","COPY",BODY,{"derivedFrom":makeQuery(id+"F32.opPattern","COPY",BODY,{"derivedFrom":makeQuery(id+"F31.opPattern","COPY",BODY,{"derivedFrom":makeQuery(id+"F30.opPattern","COPY",BODY,{"derivedFrom":makeQuery(id+"F29.opPattern","COPY",BODY,{"derivedFrom":makeQuery(id+"F28.opPattern","COPY",BODY,{"derivedFrom":makeQuery(id+"F27.opPattern","COPY",BODY,{"derivedFrom":makeQuery(id+"F26.opPattern","COPY",BODY,{"derivedFrom":makeQuery(id+"F25.opPattern","COPY",BODY,{"derivedFrom":makeQuery(id+"F24.opPattern","COPY",BODY,{"derivedFrom":makeQuery(id+"F23.opPattern","COPY",BODY,{"derivedFrom":makeQuery(id+"F22.opPattern","COPY",BODY,{"derivedFrom":makeQuery(id+"F21.opPattern","COPY",BODY,{"derivedFrom":makeQuery(id+"F20.opPattern","COPY",BODY,{"derivedFrom":makeQuery(id+"F19.opPattern","COPY",BODY,{"derivedFrom":makeQuery(id+"F18.opPattern","COPY",BODY,{"derivedFrom":makeQuery(id+"F1.opExtrude","SWEPT_BODY",BODY,{"disambiguationData":[OSD([sQuery(id+"F0.wireOp",EDGE,"E0")])]}),"instanceName":"1"}),"instanceName":"1"}),"instanceName":"1"}),"instanceName":"1"}),"instanceName":"1"}),"instanceName":"1"}),"instanceName":"1"}),"instanceName":"1"}),"instanceName":"1"}),"instanceName":"1"}),"instanceName":"1"}),"instanceName":"1"}),"instanceName":"1"}),"instanceName":"1"}),"instanceName":"1"}),"instanceName":"1"}),"instanceName":"1"}),"instanceName":"1"}),"instanceName":"1"}),"instanceName":"1"}),"instanceName":"1"}),"instanceName":"1"}),"instanceName":"1"}),"instanceName":"1"}),"instanceName":"1"}),"instanceName":"1"}),"instanceName":"1"}),"instanceName":"1"});
            deleteBodies(context, id + "F78", {"entities" : qUnion([Q0, Q1, Q2, Q3, Q4])});
        }
        {
            var Q0;
            Q0 = qSketchRegion(id + "F66", true);
            extrude(context, id + "F79", {"entities" : qUnion([Q0]), "depth" : 2.5 * mm});
        }
        {
            var Q0;
            Q0=makeQuery(id+"F79.opExtrude","SWEPT_BODY",BODY,{"disambiguationData":[OSD([sQuery(id+"F66.wireOp",EDGE,"E1.bottom"),sQuery(id+"F66.wireOp",EDGE,"E1.top"),sQuery(id+"F66.wireOp",EDGE,"E1.left"),sQuery(id+"F66.wireOp",EDGE,"E1.right")])]});
            transform(context, id + "F80", {"entities" : qUnion([Q0]), "transformType" : TransformType.TRANSLATION_3D, "dx" : 0 * mm, "dy" : 0 * mm, "dz" : -500 * mm, "makeCopy" : true});
        }
        {
            var Q0;
            Q0=makeQuery(id+"F79.opExtrude","SWEPT_BODY",BODY,{"disambiguationData":[OSD([sQuery(id+"F66.wireOp",EDGE,"E1.bottom"),sQuery(id+"F66.wireOp",EDGE,"E1.top"),sQuery(id+"F66.wireOp",EDGE,"E1.left"),sQuery(id+"F66.wireOp",EDGE,"E1.right")])]});
            transform(context, id + "F81", {"entities" : qUnion([Q0]), "transformType" : TransformType.TRANSLATION_3D, "dx" : 0 * mm, "dy" : 19980 * mm, "dz" : 0 * mm, "makeCopy" : true});
        }
        {
            var Q0;
            Q0=makeQuery(id+"F80.opPattern","COPY",BODY,{"derivedFrom":makeQuery(id+"F79.opExtrude","SWEPT_BODY",BODY,{"disambiguationData":[OSD([sQuery(id+"F66.wireOp",EDGE,"E1.bottom"),sQuery(id+"F66.wireOp",EDGE,"E1.top"),sQuery(id+"F66.wireOp",EDGE,"E1.left"),sQuery(id+"F66.wireOp",EDGE,"E1.right")])]}),"instanceName":"1"});
            transform(context, id + "F82", {"entities" : qUnion([Q0]), "transformType" : TransformType.TRANSLATION_3D, "dx" : 0 * mm, "dy" : 19980 * mm, "dz" : 0 * mm, "makeCopy" : true});
        }
        {
            var Q0;
            Q0=qCreatedBy(makeId("Right.planeOp"),FACE);
            var sketch = newSketch(context, id + "F83", { "sketchPlane" : qUnion([Q0])});
            skLineSegment(sketch, "E2.bottom", {"start": v(0, 1236.45) * mm, "end": v(20105, 1236.45) * mm});
            skLineSegment(sketch, "E2.top", {"start": v(0, 1116.45) * mm, "end": v(20105, 1116.45) * mm});
            skLineSegment(sketch, "E2.left", {"start": v(0, 1236.45) * mm, "end": v(0, 1116.45) * mm});
            skLineSegment(sketch, "E2.right", {"start": v(20105, 1236.45) * mm, "end": v(20105, 1116.45) * mm});
            skSolve(sketch);
        }
        {
            var Q0;
            Q0 = qSketchRegion(id + "F83", true);
            extrude(context, id + "F84", {"entities" : qUnion([Q0]), "depth" : 5 * mm});
        }
        {
            var Q0;
            Q0=makeQuery(id+"F84.opExtrude","SWEPT_BODY",BODY,{"disambiguationData":[OSD([sQuery(id+"F83.wireOp",EDGE,"E2.bottom"),sQuery(id+"F83.wireOp",EDGE,"E2.top"),sQuery(id+"F83.wireOp",EDGE,"E2.left"),sQuery(id+"F83.wireOp",EDGE,"E2.right")])]});
            transform(context, id + "F85", {"entities" : qUnion([Q0]), "transformType" : TransformType.TRANSLATION_3D, "dx" : 0 * mm, "dy" : 0 * mm, "dz" : -500 * mm, "makeCopy" : true});
        }
        {
            var Q0;
            Q0=qCreatedBy(makeId("Right.planeOp"),FACE);
            var sketch = newSketch(context, id + "F86", { "sketchPlane" : qUnion([Q0])});
            skLineSegment(sketch, "E3.bottom", {"start": v(0, 1277.46) * mm, "end": v(8795.4, 1277.46) * mm});
            skLineSegment(sketch, "E3.top", {"start": v(0, 1141.94) * mm, "end": v(8795.4, 1141.94) * mm});
            skLineSegment(sketch, "E3.left", {"start": v(0, 1277.46) * mm, "end": v(0, 1141.94) * mm});
            skLineSegment(sketch, "E3.right", {"start": v(8795.4, 1277.46) * mm, "end": v(8795.4, 1141.94) * mm});
            skSolve(sketch);
        }
        {
            var Q0;
            Q0 = qSketchRegion(id + "F86", true);
            extrude(context, id + "F87", {"entities" : qUnion([Q0]), "depth" : 5 * mm});
        }
        {
            var Q0;
            Q0=makeQuery(id+"F87.opExtrude","SWEPT_BODY",BODY,{"disambiguationData":[OSD([sQuery(id+"F86.wireOp",EDGE,"E3.bottom"),sQuery(id+"F86.wireOp",EDGE,"E3.top"),sQuery(id+"F86.wireOp",EDGE,"E3.left"),sQuery(id+"F86.wireOp",EDGE,"E3.right")])]});
            transform(context, id + "F88", {"entities" : qUnion([Q0]), "transformType" : TransformType.TRANSLATION_3D, "dx" : 59940 * mm, "dy" : 0 * mm, "dz" : 0 * mm, "makeCopy" : true});
        }
        {
            var Q0;
            Q0=makeQuery(id+"F87.opExtrude","SWEPT_BODY",BODY,{"disambiguationData":[OSD([sQuery(id+"F86.wireOp",EDGE,"E3.bottom"),sQuery(id+"F86.wireOp",EDGE,"E3.top"),sQuery(id+"F86.wireOp",EDGE,"E3.left"),sQuery(id+"F86.wireOp",EDGE,"E3.right")])]});
            deleteBodies(context, id + "F89", {"entities" : qUnion([Q0])});
        }
        {
            var Q0;
            Q0=makeQuery(id+"F88.opPattern","COPY",BODY,{"derivedFrom":makeQuery(id+"F87.opExtrude","SWEPT_BODY",BODY,{"disambiguationData":[OSD([sQuery(id+"F86.wireOp",EDGE,"E3.bottom"),sQuery(id+"F86.wireOp",EDGE,"E3.top"),sQuery(id+"F86.wireOp",EDGE,"E3.left"),sQuery(id+"F86.wireOp",EDGE,"E3.right")])]}),"instanceName":"1"});
            transform(context, id + "F90", {"entities" : qUnion([Q0]), "transformType" : TransformType.TRANSLATION_3D, "dx" : 0 * mm, "dy" : 0 * mm, "dz" : -500 * mm, "makeCopy" : true});
        }
        {
            var Q0;
            Q0=makeQuery(id+"F90.opPattern","COPY",BODY,{"derivedFrom":makeQuery(id+"F88.opPattern","COPY",BODY,{"derivedFrom":makeQuery(id+"F87.opExtrude","SWEPT_BODY",BODY,{"disambiguationData":[OSD([sQuery(id+"F86.wireOp",EDGE,"E3.bottom"),sQuery(id+"F86.wireOp",EDGE,"E3.top"),sQuery(id+"F86.wireOp",EDGE,"E3.left"),sQuery(id+"F86.wireOp",EDGE,"E3.right")])]}),"instanceName":"1"}),"instanceName":"1"});
            transform(context, id + "F91", {"entities" : qUnion([Q0]), "transformType" : TransformType.TRANSLATION_3D, "dx" : 0 * mm, "dy" : 11288 * mm, "dz" : 0 * mm, "makeCopy" : true});
        }
        {
            var Q0;
            Q0=makeQuery(id+"F91.opPattern","COPY",BODY,{"derivedFrom":makeQuery(id+"F90.opPattern","COPY",BODY,{"derivedFrom":makeQuery(id+"F88.opPattern","COPY",BODY,{"derivedFrom":makeQuery(id+"F87.opExtrude","SWEPT_BODY",BODY,{"disambiguationData":[OSD([sQuery(id+"F86.wireOp",EDGE,"E3.bottom"),sQuery(id+"F86.wireOp",EDGE,"E3.top"),sQuery(id+"F86.wireOp",EDGE,"E3.left"),sQuery(id+"F86.wireOp",EDGE,"E3.right")])]}),"instanceName":"1"}),"instanceName":"1"}),"instanceName":"1"});
            transform(context, id + "F92", {"entities" : qUnion([Q0]), "transformType" : TransformType.TRANSLATION_3D, "dx" : 0 * mm, "dy" : 0 * mm, "dz" : 500 * mm, "makeCopy" : true});
        }
    });
